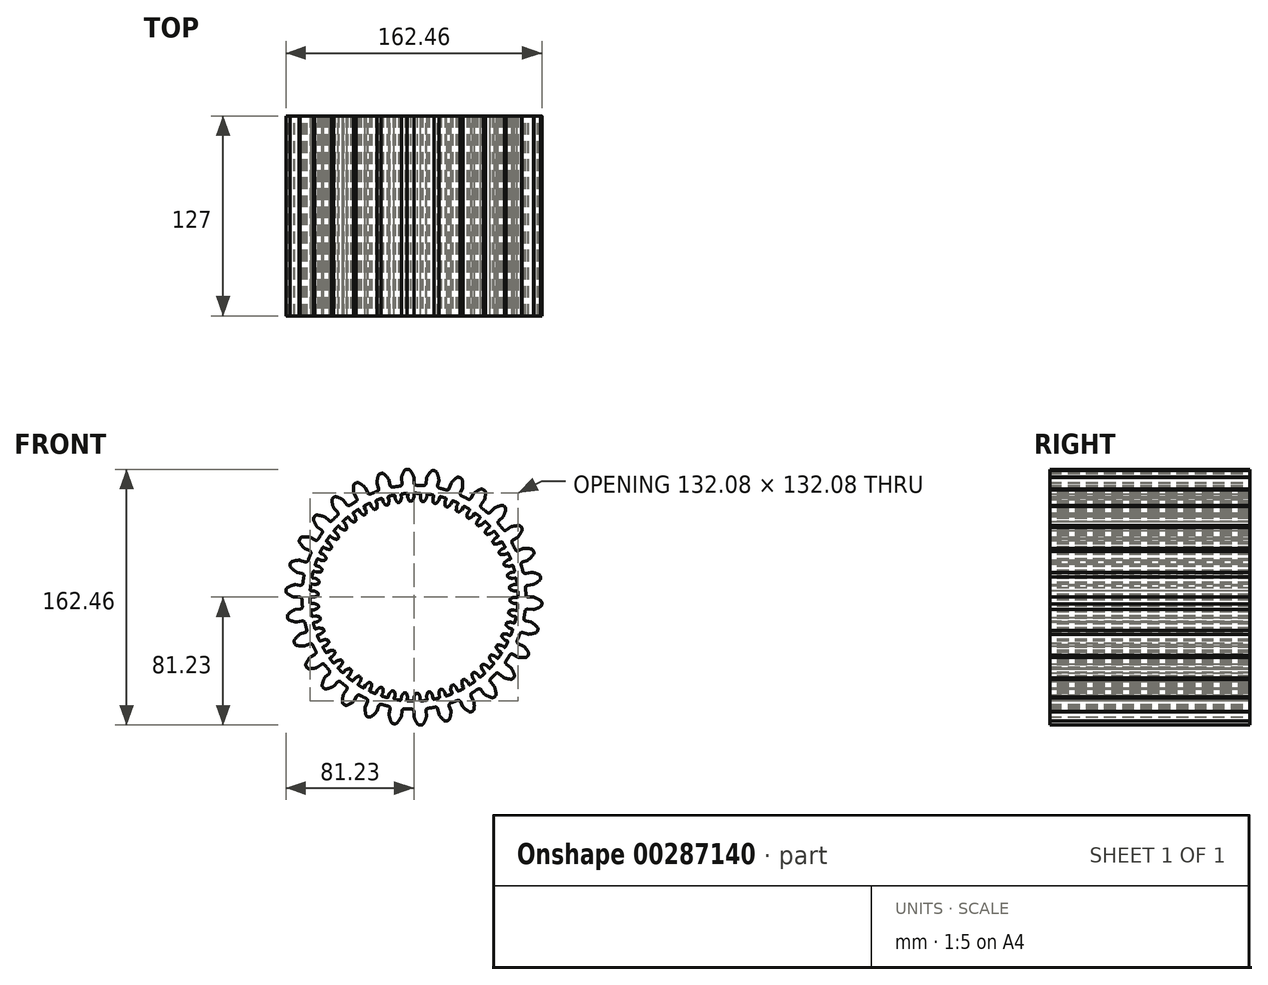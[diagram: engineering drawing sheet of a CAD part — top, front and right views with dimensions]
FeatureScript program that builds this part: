
annotation { "Feature Type Name" : "Feature", "Feature Type Description" : "" }
export const myFeature = defineFeature(function(context is Context, id is Id, definition is map)
    precondition{}
    {
        {
            var Q0;
            Q0=qCreatedBy(makeId("Front.planeOp"),FACE);
            var sketch = newSketch(context, id + "F0", { "sketchPlane" : qUnion([Q0])});
            skArc(sketch, "E0", {"start": v(-8.92, 70.56) * mm, "mid": v(-11.13, 70.24) * mm, "end": v(-13.32, 69.86) * mm});
            skPoint(sketch, "E1", {"position": v(0, 76.2) * mm});
            skArc(sketch, "E2.trimOffspring", {"start": v(-0.11, 76.48) * mm, "mid": v(-1.13, 78.61) * mm, "end": v(-2.4, 80.6) * mm});
            skLineSegment(sketch, "E3", {"start": v(-3.63, 81.23) * mm, "end": v(-4.26, 81.23) * mm});
            skLineSegment(sketch, "E4", {"start": v(0, 75.91) * mm, "end": v(0, 72.63) * mm});
            skLineSegment(sketch, "E5.MirrorCS", {"start": v(-4.88, 81.16) * mm, "end": v(-4.26, 81.23) * mm});
            skArc(sketch, "E6.MirrorCS", {"start": v(-7.88, 76.07) * mm, "mid": v(-7.1, 78.3) * mm, "end": v(-6.04, 80.41) * mm});
            skLineSegment(sketch, "E7.MirrorCS", {"start": v(-7.93, 75.5) * mm, "end": v(-7.6, 72.23) * mm});
            skPoint(sketch, "E8.orphan", {"position": v(0, 69.34) * mm});
            skPoint(sketch, "E9.visualSharp", {"position": v(-7.43, 70.73) * mm});
            skPoint(sketch, "E10.visualSharp", {"position": v(0, 71.12) * mm});
            skArc(sketch, "E10.filletArc", {"start": v(0, 72.63) * mm, "mid": v(0.44, 71.56) * mm, "end": v(1.5, 71.1) * mm});
            skArc(sketch, "E11.filletArc", {"start": v(-8.92, 70.56) * mm, "mid": v(-7.91, 71.12) * mm, "end": v(-7.6, 72.23) * mm});
            skPoint(sketch, "E12.visualSharp", {"position": v(-7.97, 75.78) * mm});
            skArc(sketch, "E12.filletArc", {"start": v(-7.88, 76.07) * mm, "mid": v(-7.94, 75.79) * mm, "end": v(-7.93, 75.5) * mm});
            skPoint(sketch, "E13.visualSharp", {"position": v(-5.63, 81.08) * mm});
            skArc(sketch, "E13.filletArc", {"start": v(-4.88, 81.16) * mm, "mid": v(-5.55, 80.93) * mm, "end": v(-6.04, 80.41) * mm});
            skPoint(sketch, "E14.visualSharp", {"position": v(-2.88, 81.23) * mm});
            skArc(sketch, "E14.filletArc", {"start": v(-2.4, 80.6) * mm, "mid": v(-2.94, 81.06) * mm, "end": v(-3.63, 81.23) * mm});
            skArc(sketch, "E15.filletArc", {"start": v(0, 75.91) * mm, "mid": v(-0.03, 76.2) * mm, "end": v(-0.11, 76.48) * mm});
            skArc(sketch, "E16.1.0", {"start": v(-23.4, 67.16) * mm, "mid": v(-22.53, 67.92) * mm, "end": v(-22.44, 69.07) * mm});
            skArc(sketch, "E16.1.1", {"start": v(-15.1, 71.04) * mm, "mid": v(-14.45, 70.09) * mm, "end": v(-13.32, 69.86) * mm});
            skLineSegment(sketch, "E16.1.2", {"start": v(-15.78, 74.25) * mm, "end": v(-15.1, 71.04) * mm});
            skLineSegment(sketch, "E16.1.3", {"start": v(-23.46, 72.2) * mm, "end": v(-22.44, 69.07) * mm});
            skLineSegment(sketch, "E16.1.4", {"start": v(-21.65, 78.38) * mm, "end": v(-21.05, 78.57) * mm});
            skPoint(sketch, "E16.1.5", {"position": v(-15.84, 74.53) * mm});
            skArc(sketch, "E16.1.6", {"start": v(-23.53, 72.77) * mm, "mid": v(-23.22, 75.11) * mm, "end": v(-22.62, 77.4) * mm});
            skArc(sketch, "E16.1.7", {"start": v(-16, 74.79) * mm, "mid": v(-17.45, 76.66) * mm, "end": v(-19.1, 78.34) * mm});
            skLineSegment(sketch, "E16.1.8", {"start": v(-20.44, 78.7) * mm, "end": v(-21.05, 78.57) * mm});
            skPoint(sketch, "E16.1.9", {"position": v(-19.7, 78.86) * mm});
            skArc(sketch, "E16.1.10", {"start": v(-19.1, 78.34) * mm, "mid": v(-19.73, 78.68) * mm, "end": v(-20.44, 78.7) * mm});
            skArc(sketch, "E16.1.11", {"start": v(-21.65, 78.38) * mm, "mid": v(-22.25, 78) * mm, "end": v(-22.62, 77.4) * mm});
            skPoint(sketch, "E16.1.12", {"position": v(-23.55, 72.47) * mm});
            skPoint(sketch, "E16.1.13", {"position": v(-22.36, 78.14) * mm});
            skArc(sketch, "E16.1.14", {"start": v(-23.53, 72.77) * mm, "mid": v(-23.52, 72.48) * mm, "end": v(-23.46, 72.2) * mm});
            skPoint(sketch, "E16.1.15", {"position": v(-15.84, 74.53) * mm});
            skArc(sketch, "E16.1.16", {"start": v(-15.78, 74.25) * mm, "mid": v(-15.87, 74.53) * mm, "end": v(-16, 74.79) * mm});
            skArc(sketch, "E16.2.0", {"start": v(-36.84, 60.83) * mm, "mid": v(-36.16, 61.76) * mm, "end": v(-36.31, 62.9) * mm});
            skArc(sketch, "E16.2.1", {"start": v(-29.54, 66.35) * mm, "mid": v(-28.7, 65.55) * mm, "end": v(-27.56, 65.56) * mm});
            skLineSegment(sketch, "E16.2.2", {"start": v(-30.88, 69.35) * mm, "end": v(-29.54, 66.35) * mm});
            skLineSegment(sketch, "E16.2.3", {"start": v(-37.96, 65.74) * mm, "end": v(-36.31, 62.9) * mm});
            skLineSegment(sketch, "E16.2.4", {"start": v(-37.47, 72.16) * mm, "end": v(-36.93, 72.47) * mm});
            skPoint(sketch, "E16.2.5", {"position": v(-31, 69.61) * mm});
            skArc(sketch, "E16.2.6", {"start": v(-38.14, 66.29) * mm, "mid": v(-38.33, 68.65) * mm, "end": v(-38.22, 71) * mm});
            skArc(sketch, "E16.2.7", {"start": v(-31.2, 69.82) * mm, "mid": v(-33, 71.36) * mm, "end": v(-34.98, 72.66) * mm});
            skLineSegment(sketch, "E16.2.8", {"start": v(-36.36, 72.73) * mm, "end": v(-36.93, 72.47) * mm});
            skPoint(sketch, "E16.2.9", {"position": v(-35.67, 73.04) * mm});
            skArc(sketch, "E16.2.10", {"start": v(-34.98, 72.66) * mm, "mid": v(-35.66, 72.86) * mm, "end": v(-36.36, 72.73) * mm});
            skArc(sketch, "E16.2.11", {"start": v(-37.47, 72.16) * mm, "mid": v(-37.98, 71.67) * mm, "end": v(-38.22, 71) * mm});
            skPoint(sketch, "E16.2.12", {"position": v(-38.1, 66) * mm});
            skPoint(sketch, "E16.2.13", {"position": v(-38.12, 71.79) * mm});
            skArc(sketch, "E16.2.14", {"start": v(-38.14, 66.29) * mm, "mid": v(-38.08, 66) * mm, "end": v(-37.96, 65.74) * mm});
            skPoint(sketch, "E16.2.15", {"position": v(-31, 69.61) * mm});
            skArc(sketch, "E16.2.16", {"start": v(-30.88, 69.35) * mm, "mid": v(-31.02, 69.6) * mm, "end": v(-31.2, 69.82) * mm});
            skArc(sketch, "E17.2.3.0", {"start": v(-48.69, 51.84) * mm, "mid": v(-48.2, 52.89) * mm, "end": v(-48.6, 53.97) * mm});
            skArc(sketch, "E17.4.3.0", {"start": v(-42.69, 58.76) * mm, "mid": v(-41.71, 58.15) * mm, "end": v(-40.59, 58.4) * mm});
            skLineSegment(sketch, "E17.8.3.0", {"start": v(-44.62, 61.41) * mm, "end": v(-42.69, 58.76) * mm});
            skLineSegment(sketch, "E17.11.3.0", {"start": v(-50.8, 56.41) * mm, "end": v(-48.6, 53.97) * mm});
            skLineSegment(sketch, "E17.14.3.0", {"start": v(-51.65, 62.8) * mm, "end": v(-51.19, 63.21) * mm});
            skPoint(sketch, "E17.17.3.0", {"position": v(-44.79, 61.65) * mm});
            skArc(sketch, "E17.18.3.0", {"start": v(-51.1, 56.9) * mm, "mid": v(-51.76, 59.18) * mm, "end": v(-52.15, 61.5) * mm});
            skArc(sketch, "E17.22.3.0", {"start": v(-45.04, 61.8) * mm, "mid": v(-47.12, 62.94) * mm, "end": v(-49.32, 63.8) * mm});
            skLineSegment(sketch, "E17.26.3.0", {"start": v(-50.68, 63.58) * mm, "end": v(-51.19, 63.21) * mm});
            skPoint(sketch, "E17.29.3.0", {"position": v(-50.07, 64.02) * mm});
            skArc(sketch, "E17.30.3.0", {"start": v(-49.32, 63.8) * mm, "mid": v(-50.03, 63.85) * mm, "end": v(-50.68, 63.58) * mm});
            skArc(sketch, "E17.34.3.0", {"start": v(-51.65, 62.8) * mm, "mid": v(-52.06, 62.21) * mm, "end": v(-52.15, 61.5) * mm});
            skPoint(sketch, "E17.38.3.0", {"position": v(-50.99, 56.63) * mm});
            skPoint(sketch, "E17.39.3.0", {"position": v(-52.21, 62.3) * mm});
            skArc(sketch, "E17.40.3.0", {"start": v(-51.1, 56.9) * mm, "mid": v(-50.97, 56.65) * mm, "end": v(-50.8, 56.41) * mm});
            skPoint(sketch, "E17.44.3.0", {"position": v(-44.79, 61.65) * mm});
            skArc(sketch, "E17.45.3.0", {"start": v(-44.62, 61.41) * mm, "mid": v(-44.81, 61.63) * mm, "end": v(-45.04, 61.8) * mm});
            skArc(sketch, "E17.2.4.0", {"start": v(-58.4, 40.59) * mm, "mid": v(-58.15, 41.71) * mm, "end": v(-58.76, 42.69) * mm});
            skArc(sketch, "E17.4.4.0", {"start": v(-53.97, 48.6) * mm, "mid": v(-52.89, 48.2) * mm, "end": v(-51.84, 48.69) * mm});
            skLineSegment(sketch, "E17.8.4.0", {"start": v(-56.41, 50.8) * mm, "end": v(-53.97, 48.6) * mm});
            skLineSegment(sketch, "E17.11.4.0", {"start": v(-61.41, 44.62) * mm, "end": v(-58.76, 42.69) * mm});
            skLineSegment(sketch, "E17.14.4.0", {"start": v(-63.58, 50.68) * mm, "end": v(-63.21, 51.19) * mm});
            skPoint(sketch, "E17.17.4.0", {"position": v(-56.63, 50.99) * mm});
            skArc(sketch, "E17.18.4.0", {"start": v(-61.8, 45.04) * mm, "mid": v(-62.94, 47.12) * mm, "end": v(-63.8, 49.32) * mm});
            skArc(sketch, "E17.22.4.0", {"start": v(-56.9, 51.1) * mm, "mid": v(-59.18, 51.76) * mm, "end": v(-61.5, 52.15) * mm});
            skLineSegment(sketch, "E17.26.4.0", {"start": v(-62.8, 51.65) * mm, "end": v(-63.21, 51.19) * mm});
            skPoint(sketch, "E17.29.4.0", {"position": v(-62.3, 52.21) * mm});
            skArc(sketch, "E17.30.4.0", {"start": v(-61.5, 52.15) * mm, "mid": v(-62.21, 52.06) * mm, "end": v(-62.8, 51.65) * mm});
            skArc(sketch, "E17.34.4.0", {"start": v(-63.58, 50.68) * mm, "mid": v(-63.85, 50.03) * mm, "end": v(-63.8, 49.32) * mm});
            skPoint(sketch, "E17.38.4.0", {"position": v(-61.65, 44.79) * mm});
            skPoint(sketch, "E17.39.4.0", {"position": v(-64.02, 50.07) * mm});
            skArc(sketch, "E17.40.4.0", {"start": v(-61.8, 45.04) * mm, "mid": v(-61.63, 44.81) * mm, "end": v(-61.41, 44.62) * mm});
            skPoint(sketch, "E17.44.4.0", {"position": v(-56.63, 50.99) * mm});
            skArc(sketch, "E17.45.4.0", {"start": v(-56.41, 50.8) * mm, "mid": v(-56.65, 50.97) * mm, "end": v(-56.9, 51.1) * mm});
            skArc(sketch, "E17.2.5.0", {"start": v(-65.56, 27.56) * mm, "mid": v(-65.55, 28.7) * mm, "end": v(-66.35, 29.54) * mm});
            skArc(sketch, "E17.4.5.0", {"start": v(-62.9, 36.31) * mm, "mid": v(-61.76, 36.16) * mm, "end": v(-60.83, 36.84) * mm});
            skLineSegment(sketch, "E17.8.5.0", {"start": v(-65.74, 37.96) * mm, "end": v(-62.9, 36.31) * mm});
            skLineSegment(sketch, "E17.11.5.0", {"start": v(-69.35, 30.88) * mm, "end": v(-66.35, 29.54) * mm});
            skLineSegment(sketch, "E17.14.5.0", {"start": v(-72.73, 36.36) * mm, "end": v(-72.47, 36.93) * mm});
            skPoint(sketch, "E17.17.5.0", {"position": v(-66, 38.1) * mm});
            skArc(sketch, "E17.18.5.0", {"start": v(-69.82, 31.2) * mm, "mid": v(-71.36, 33) * mm, "end": v(-72.66, 34.98) * mm});
            skArc(sketch, "E17.22.5.0", {"start": v(-66.29, 38.14) * mm, "mid": v(-68.65, 38.33) * mm, "end": v(-71, 38.22) * mm});
            skLineSegment(sketch, "E17.26.5.0", {"start": v(-72.16, 37.47) * mm, "end": v(-72.47, 36.93) * mm});
            skPoint(sketch, "E17.29.5.0", {"position": v(-71.79, 38.12) * mm});
            skArc(sketch, "E17.30.5.0", {"start": v(-71, 38.22) * mm, "mid": v(-71.67, 37.98) * mm, "end": v(-72.16, 37.47) * mm});
            skArc(sketch, "E17.34.5.0", {"start": v(-72.73, 36.36) * mm, "mid": v(-72.86, 35.66) * mm, "end": v(-72.66, 34.98) * mm});
            skPoint(sketch, "E17.38.5.0", {"position": v(-69.61, 31) * mm});
            skPoint(sketch, "E17.39.5.0", {"position": v(-73.04, 35.67) * mm});
            skArc(sketch, "E17.40.5.0", {"start": v(-69.82, 31.2) * mm, "mid": v(-69.6, 31.02) * mm, "end": v(-69.35, 30.88) * mm});
            skPoint(sketch, "E17.44.5.0", {"position": v(-66, 38.1) * mm});
            skArc(sketch, "E17.45.5.0", {"start": v(-65.74, 37.96) * mm, "mid": v(-66, 38.08) * mm, "end": v(-66.29, 38.14) * mm});
            skArc(sketch, "E17.2.6.0", {"start": v(-69.86, 13.32) * mm, "mid": v(-70.09, 14.45) * mm, "end": v(-71.04, 15.1) * mm});
            skArc(sketch, "E17.4.6.0", {"start": v(-69.07, 22.44) * mm, "mid": v(-67.92, 22.53) * mm, "end": v(-67.16, 23.4) * mm});
            skLineSegment(sketch, "E17.8.6.0", {"start": v(-72.2, 23.46) * mm, "end": v(-69.07, 22.44) * mm});
            skLineSegment(sketch, "E17.11.6.0", {"start": v(-74.25, 15.78) * mm, "end": v(-71.04, 15.1) * mm});
            skLineSegment(sketch, "E17.14.6.0", {"start": v(-78.7, 20.44) * mm, "end": v(-78.57, 21.05) * mm});
            skPoint(sketch, "E17.17.6.0", {"position": v(-72.47, 23.55) * mm});
            skArc(sketch, "E17.18.6.0", {"start": v(-74.79, 16) * mm, "mid": v(-76.66, 17.45) * mm, "end": v(-78.34, 19.1) * mm});
            skArc(sketch, "E17.22.6.0", {"start": v(-72.77, 23.53) * mm, "mid": v(-75.11, 23.22) * mm, "end": v(-77.4, 22.62) * mm});
            skLineSegment(sketch, "E17.26.6.0", {"start": v(-78.38, 21.65) * mm, "end": v(-78.57, 21.05) * mm});
            skPoint(sketch, "E17.29.6.0", {"position": v(-78.14, 22.36) * mm});
            skArc(sketch, "E17.30.6.0", {"start": v(-77.4, 22.62) * mm, "mid": v(-78, 22.25) * mm, "end": v(-78.38, 21.65) * mm});
            skArc(sketch, "E17.34.6.0", {"start": v(-78.7, 20.44) * mm, "mid": v(-78.68, 19.73) * mm, "end": v(-78.34, 19.1) * mm});
            skPoint(sketch, "E17.38.6.0", {"position": v(-74.53, 15.84) * mm});
            skPoint(sketch, "E17.39.6.0", {"position": v(-78.86, 19.7) * mm});
            skArc(sketch, "E17.40.6.0", {"start": v(-74.79, 16) * mm, "mid": v(-74.53, 15.87) * mm, "end": v(-74.25, 15.78) * mm});
            skPoint(sketch, "E17.44.6.0", {"position": v(-72.47, 23.55) * mm});
            skArc(sketch, "E17.45.6.0", {"start": v(-72.2, 23.46) * mm, "mid": v(-72.48, 23.52) * mm, "end": v(-72.77, 23.53) * mm});
            skArc(sketch, "E17.2.7.0", {"start": v(-71.1, -1.5) * mm, "mid": v(-71.56, -0.44) * mm, "end": v(-72.63, 0) * mm});
            skArc(sketch, "E17.4.7.0", {"start": v(-72.23, 7.6) * mm, "mid": v(-71.12, 7.91) * mm, "end": v(-70.56, 8.92) * mm});
            skLineSegment(sketch, "E17.8.7.0", {"start": v(-75.5, 7.93) * mm, "end": v(-72.23, 7.6) * mm});
            skLineSegment(sketch, "E17.11.7.0", {"start": v(-75.91, 0) * mm, "end": v(-72.63, 0) * mm});
            skLineSegment(sketch, "E17.14.7.0", {"start": v(-81.23, 3.63) * mm, "end": v(-81.23, 4.26) * mm});
            skPoint(sketch, "E17.17.7.0", {"position": v(-75.78, 7.97) * mm});
            skArc(sketch, "E17.18.7.0", {"start": v(-76.48, 0.11) * mm, "mid": v(-78.61, 1.13) * mm, "end": v(-80.6, 2.4) * mm});
            skArc(sketch, "E17.22.7.0", {"start": v(-76.07, 7.88) * mm, "mid": v(-78.3, 7.1) * mm, "end": v(-80.41, 6.04) * mm});
            skLineSegment(sketch, "E17.26.7.0", {"start": v(-81.16, 4.88) * mm, "end": v(-81.23, 4.26) * mm});
            skPoint(sketch, "E17.29.7.0", {"position": v(-81.08, 5.63) * mm});
            skArc(sketch, "E17.30.7.0", {"start": v(-80.41, 6.04) * mm, "mid": v(-80.93, 5.55) * mm, "end": v(-81.16, 4.88) * mm});
            skArc(sketch, "E17.34.7.0", {"start": v(-81.23, 3.63) * mm, "mid": v(-81.06, 2.94) * mm, "end": v(-80.6, 2.4) * mm});
            skPoint(sketch, "E17.38.7.0", {"position": v(-76.2, 0) * mm});
            skPoint(sketch, "E17.39.7.0", {"position": v(-81.23, 2.88) * mm});
            skArc(sketch, "E17.40.7.0", {"start": v(-76.48, 0.11) * mm, "mid": v(-76.2, 0.03) * mm, "end": v(-75.91, 0) * mm});
            skPoint(sketch, "E17.44.7.0", {"position": v(-75.78, 7.97) * mm});
            skArc(sketch, "E17.45.7.0", {"start": v(-75.5, 7.93) * mm, "mid": v(-75.79, 7.94) * mm, "end": v(-76.07, 7.88) * mm});
            skArc(sketch, "E17.2.8.0", {"start": v(-69.24, -16.24) * mm, "mid": v(-69.9, -15.3) * mm, "end": v(-71.04, -15.1) * mm});
            skArc(sketch, "E17.4.8.0", {"start": v(-72.23, -7.6) * mm, "mid": v(-71.22, -7.05) * mm, "end": v(-70.87, -5.95) * mm});
            skLineSegment(sketch, "E17.8.8.0", {"start": v(-75.5, -7.93) * mm, "end": v(-72.23, -7.6) * mm});
            skLineSegment(sketch, "E17.11.8.0", {"start": v(-74.25, -15.78) * mm, "end": v(-71.04, -15.1) * mm});
            skLineSegment(sketch, "E17.14.8.0", {"start": v(-80.2, -13.34) * mm, "end": v(-80.34, -12.72) * mm});
            skPoint(sketch, "E17.17.8.0", {"position": v(-75.78, -7.97) * mm});
            skArc(sketch, "E17.18.8.0", {"start": v(-74.83, -15.8) * mm, "mid": v(-77.13, -15.24) * mm, "end": v(-79.34, -14.4) * mm});
            skArc(sketch, "E17.22.8.0", {"start": v(-76.05, -8.1) * mm, "mid": v(-78.07, -9.34) * mm, "end": v(-79.91, -10.81) * mm});
            skLineSegment(sketch, "E17.26.8.0", {"start": v(-80.4, -12.1) * mm, "end": v(-80.34, -12.72) * mm});
            skPoint(sketch, "E17.29.8.0", {"position": v(-80.48, -11.35) * mm});
            skArc(sketch, "E17.30.8.0", {"start": v(-79.91, -10.81) * mm, "mid": v(-80.31, -11.4) * mm, "end": v(-80.4, -12.1) * mm});
            skArc(sketch, "E17.34.8.0", {"start": v(-80.2, -13.34) * mm, "mid": v(-79.9, -13.98) * mm, "end": v(-79.34, -14.4) * mm});
            skPoint(sketch, "E17.38.8.0", {"position": v(-74.53, -15.84) * mm});
            skPoint(sketch, "E17.39.8.0", {"position": v(-80.05, -14.07) * mm});
            skArc(sketch, "E17.40.8.0", {"start": v(-74.83, -15.8) * mm, "mid": v(-74.54, -15.82) * mm, "end": v(-74.25, -15.78) * mm});
            skPoint(sketch, "E17.44.8.0", {"position": v(-75.78, -7.97) * mm});
            skArc(sketch, "E17.45.8.0", {"start": v(-75.5, -7.93) * mm, "mid": v(-75.78, -8) * mm, "end": v(-76.05, -8.1) * mm});
            skArc(sketch, "E17.2.9.0", {"start": v(-64.35, -30.28) * mm, "mid": v(-65.2, -29.5) * mm, "end": v(-66.35, -29.54) * mm});
            skArc(sketch, "E17.4.9.0", {"start": v(-69.07, -22.44) * mm, "mid": v(-68.2, -21.7) * mm, "end": v(-68.09, -20.55) * mm});
            skLineSegment(sketch, "E17.8.9.0", {"start": v(-72.2, -23.46) * mm, "end": v(-69.07, -22.44) * mm});
            skLineSegment(sketch, "E17.11.9.0", {"start": v(-69.35, -30.88) * mm, "end": v(-66.35, -29.54) * mm});
            skLineSegment(sketch, "E17.14.9.0", {"start": v(-75.68, -29.72) * mm, "end": v(-75.94, -29.15) * mm});
            skPoint(sketch, "E17.17.9.0", {"position": v(-72.47, -23.55) * mm});
            skArc(sketch, "E17.18.9.0", {"start": v(-69.91, -31) * mm, "mid": v(-72.28, -30.94) * mm, "end": v(-74.61, -30.6) * mm});
            skArc(sketch, "E17.22.9.0", {"start": v(-72.7, -23.74) * mm, "mid": v(-74.42, -25.37) * mm, "end": v(-75.92, -27.2) * mm});
            skLineSegment(sketch, "E17.26.9.0", {"start": v(-76.13, -28.56) * mm, "end": v(-75.94, -29.15) * mm});
            skPoint(sketch, "E17.29.9.0", {"position": v(-76.36, -27.84) * mm});
            skArc(sketch, "E17.30.9.0", {"start": v(-75.92, -27.2) * mm, "mid": v(-76.19, -27.85) * mm, "end": v(-76.13, -28.56) * mm});
            skArc(sketch, "E17.34.9.0", {"start": v(-75.68, -29.72) * mm, "mid": v(-75.25, -30.28) * mm, "end": v(-74.61, -30.6) * mm});
            skPoint(sketch, "E17.38.9.0", {"position": v(-69.61, -31) * mm});
            skPoint(sketch, "E17.39.9.0", {"position": v(-75.38, -30.4) * mm});
            skArc(sketch, "E17.40.9.0", {"start": v(-69.91, -31) * mm, "mid": v(-69.62, -30.97) * mm, "end": v(-69.35, -30.88) * mm});
            skPoint(sketch, "E17.44.9.0", {"position": v(-72.47, -23.55) * mm});
            skArc(sketch, "E17.45.9.0", {"start": v(-72.2, -23.46) * mm, "mid": v(-72.46, -23.57) * mm, "end": v(-72.7, -23.74) * mm});
            skArc(sketch, "E17.2.10.0", {"start": v(-56.65, -43) * mm, "mid": v(-57.64, -42.41) * mm, "end": v(-58.76, -42.69) * mm});
            skArc(sketch, "E17.4.10.0", {"start": v(-62.9, -36.31) * mm, "mid": v(-62.2, -35.4) * mm, "end": v(-62.32, -34.26) * mm});
            skLineSegment(sketch, "E17.8.10.0", {"start": v(-65.74, -37.96) * mm, "end": v(-62.9, -36.31) * mm});
            skLineSegment(sketch, "E17.11.10.0", {"start": v(-61.41, -44.62) * mm, "end": v(-58.76, -42.69) * mm});
            skLineSegment(sketch, "E17.14.10.0", {"start": v(-67.85, -44.8) * mm, "end": v(-68.22, -44.3) * mm});
            skPoint(sketch, "E17.17.10.0", {"position": v(-66, -38.1) * mm});
            skArc(sketch, "E17.18.10.0", {"start": v(-61.94, -44.86) * mm, "mid": v(-64.26, -45.3) * mm, "end": v(-66.62, -45.44) * mm});
            skArc(sketch, "E17.22.10.0", {"start": v(-66.18, -38.34) * mm, "mid": v(-67.52, -40.28) * mm, "end": v(-68.6, -42.38) * mm});
            skLineSegment(sketch, "E17.26.10.0", {"start": v(-68.53, -43.76) * mm, "end": v(-68.22, -44.3) * mm});
            skPoint(sketch, "E17.29.10.0", {"position": v(-68.9, -43.1) * mm});
            skArc(sketch, "E17.30.10.0", {"start": v(-68.6, -42.38) * mm, "mid": v(-68.73, -43.08) * mm, "end": v(-68.53, -43.76) * mm});
            skArc(sketch, "E17.34.10.0", {"start": v(-67.85, -44.8) * mm, "mid": v(-67.31, -45.27) * mm, "end": v(-66.62, -45.44) * mm});
            skPoint(sketch, "E17.38.10.0", {"position": v(-61.65, -44.79) * mm});
            skPoint(sketch, "E17.39.10.0", {"position": v(-67.4, -45.42) * mm});
            skArc(sketch, "E17.40.10.0", {"start": v(-61.94, -44.86) * mm, "mid": v(-61.66, -44.77) * mm, "end": v(-61.41, -44.62) * mm});
            skPoint(sketch, "E17.44.10.0", {"position": v(-66, -38.1) * mm});
            skArc(sketch, "E17.45.10.0", {"start": v(-65.74, -37.96) * mm, "mid": v(-65.98, -38.12) * mm, "end": v(-66.18, -38.34) * mm});
            skArc(sketch, "E17.2.11.0", {"start": v(-46.47, -53.84) * mm, "mid": v(-47.56, -53.47) * mm, "end": v(-48.6, -53.97) * mm});
            skArc(sketch, "E17.4.11.0", {"start": v(-53.97, -48.6) * mm, "mid": v(-53.47, -47.56) * mm, "end": v(-53.84, -46.47) * mm});
            skLineSegment(sketch, "E17.8.11.0", {"start": v(-56.41, -50.8) * mm, "end": v(-53.97, -48.6) * mm});
            skLineSegment(sketch, "E17.11.11.0", {"start": v(-50.8, -56.41) * mm, "end": v(-48.6, -53.97) * mm});
            skLineSegment(sketch, "E17.14.11.0", {"start": v(-57.05, -57.93) * mm, "end": v(-57.52, -57.52) * mm});
            skPoint(sketch, "E17.17.11.0", {"position": v(-56.63, -50.99) * mm});
            skArc(sketch, "E17.18.11.0", {"start": v(-51.26, -56.76) * mm, "mid": v(-53.44, -57.67) * mm, "end": v(-55.72, -58.3) * mm});
            skArc(sketch, "E17.22.11.0", {"start": v(-56.76, -51.26) * mm, "mid": v(-57.67, -53.44) * mm, "end": v(-58.3, -55.72) * mm});
            skLineSegment(sketch, "E17.26.11.0", {"start": v(-57.93, -57.05) * mm, "end": v(-57.52, -57.52) * mm});
            skPoint(sketch, "E17.29.11.0", {"position": v(-58.44, -56.5) * mm});
            skArc(sketch, "E17.30.11.0", {"start": v(-58.3, -55.72) * mm, "mid": v(-58.27, -56.43) * mm, "end": v(-57.93, -57.05) * mm});
            skArc(sketch, "E17.34.11.0", {"start": v(-57.05, -57.93) * mm, "mid": v(-56.43, -58.27) * mm, "end": v(-55.72, -58.3) * mm});
            skPoint(sketch, "E17.38.11.0", {"position": v(-50.99, -56.63) * mm});
            skPoint(sketch, "E17.39.11.0", {"position": v(-56.5, -58.44) * mm});
            skArc(sketch, "E17.40.11.0", {"start": v(-51.26, -56.76) * mm, "mid": v(-51, -56.6) * mm, "end": v(-50.8, -56.41) * mm});
            skPoint(sketch, "E17.44.11.0", {"position": v(-56.63, -50.99) * mm});
            skArc(sketch, "E17.45.11.0", {"start": v(-56.41, -50.8) * mm, "mid": v(-56.6, -51) * mm, "end": v(-56.76, -51.26) * mm});
            skArc(sketch, "E17.2.12.0", {"start": v(-34.26, -62.32) * mm, "mid": v(-35.4, -62.2) * mm, "end": v(-36.31, -62.9) * mm});
            skArc(sketch, "E17.4.12.0", {"start": v(-42.69, -58.76) * mm, "mid": v(-42.41, -57.64) * mm, "end": v(-43, -56.65) * mm});
            skLineSegment(sketch, "E17.8.12.0", {"start": v(-44.62, -61.41) * mm, "end": v(-42.69, -58.76) * mm});
            skLineSegment(sketch, "E17.11.12.0", {"start": v(-37.96, -65.74) * mm, "end": v(-36.31, -62.9) * mm});
            skLineSegment(sketch, "E17.14.12.0", {"start": v(-43.76, -68.53) * mm, "end": v(-44.3, -68.22) * mm});
            skPoint(sketch, "E17.17.12.0", {"position": v(-44.79, -61.65) * mm});
            skArc(sketch, "E17.18.12.0", {"start": v(-38.34, -66.18) * mm, "mid": v(-40.28, -67.52) * mm, "end": v(-42.38, -68.6) * mm});
            skArc(sketch, "E17.22.12.0", {"start": v(-44.86, -61.94) * mm, "mid": v(-45.3, -64.26) * mm, "end": v(-45.44, -66.62) * mm});
            skLineSegment(sketch, "E17.26.12.0", {"start": v(-44.8, -67.85) * mm, "end": v(-44.3, -68.22) * mm});
            skPoint(sketch, "E17.29.12.0", {"position": v(-45.42, -67.4) * mm});
            skArc(sketch, "E17.30.12.0", {"start": v(-45.44, -66.62) * mm, "mid": v(-45.27, -67.31) * mm, "end": v(-44.8, -67.85) * mm});
            skArc(sketch, "E17.34.12.0", {"start": v(-43.76, -68.53) * mm, "mid": v(-43.08, -68.73) * mm, "end": v(-42.38, -68.6) * mm});
            skPoint(sketch, "E17.38.12.0", {"position": v(-38.1, -66) * mm});
            skPoint(sketch, "E17.39.12.0", {"position": v(-43.1, -68.9) * mm});
            skArc(sketch, "E17.40.12.0", {"start": v(-38.34, -66.18) * mm, "mid": v(-38.12, -65.98) * mm, "end": v(-37.96, -65.74) * mm});
            skPoint(sketch, "E17.44.12.0", {"position": v(-44.79, -61.65) * mm});
            skArc(sketch, "E17.45.12.0", {"start": v(-44.62, -61.41) * mm, "mid": v(-44.77, -61.66) * mm, "end": v(-44.86, -61.94) * mm});
            skArc(sketch, "E17.2.13.0", {"start": v(-20.55, -68.09) * mm, "mid": v(-21.7, -68.2) * mm, "end": v(-22.44, -69.07) * mm});
            skArc(sketch, "E17.4.13.0", {"start": v(-29.54, -66.35) * mm, "mid": v(-29.5, -65.2) * mm, "end": v(-30.28, -64.35) * mm});
            skLineSegment(sketch, "E17.8.13.0", {"start": v(-30.88, -69.35) * mm, "end": v(-29.54, -66.35) * mm});
            skLineSegment(sketch, "E17.11.13.0", {"start": v(-23.46, -72.2) * mm, "end": v(-22.44, -69.07) * mm});
            skLineSegment(sketch, "E17.14.13.0", {"start": v(-28.56, -76.13) * mm, "end": v(-29.15, -75.94) * mm});
            skPoint(sketch, "E17.17.13.0", {"position": v(-31, -69.61) * mm});
            skArc(sketch, "E17.18.13.0", {"start": v(-23.74, -72.7) * mm, "mid": v(-25.37, -74.42) * mm, "end": v(-27.2, -75.92) * mm});
            skArc(sketch, "E17.22.13.0", {"start": v(-31, -69.91) * mm, "mid": v(-30.94, -72.28) * mm, "end": v(-30.6, -74.61) * mm});
            skLineSegment(sketch, "E17.26.13.0", {"start": v(-29.72, -75.68) * mm, "end": v(-29.15, -75.94) * mm});
            skPoint(sketch, "E17.29.13.0", {"position": v(-30.4, -75.38) * mm});
            skArc(sketch, "E17.30.13.0", {"start": v(-30.6, -74.61) * mm, "mid": v(-30.28, -75.25) * mm, "end": v(-29.72, -75.68) * mm});
            skArc(sketch, "E17.34.13.0", {"start": v(-28.56, -76.13) * mm, "mid": v(-27.85, -76.19) * mm, "end": v(-27.2, -75.92) * mm});
            skPoint(sketch, "E17.38.13.0", {"position": v(-23.55, -72.47) * mm});
            skPoint(sketch, "E17.39.13.0", {"position": v(-27.84, -76.36) * mm});
            skArc(sketch, "E17.40.13.0", {"start": v(-23.74, -72.7) * mm, "mid": v(-23.57, -72.46) * mm, "end": v(-23.46, -72.2) * mm});
            skPoint(sketch, "E17.44.13.0", {"position": v(-31, -69.61) * mm});
            skArc(sketch, "E17.45.13.0", {"start": v(-30.88, -69.35) * mm, "mid": v(-30.97, -69.62) * mm, "end": v(-31, -69.91) * mm});
            skArc(sketch, "E17.2.14.0", {"start": v(-5.95, -70.87) * mm, "mid": v(-7.05, -71.22) * mm, "end": v(-7.6, -72.23) * mm});
            skArc(sketch, "E17.4.14.0", {"start": v(-15.1, -71.04) * mm, "mid": v(-15.3, -69.9) * mm, "end": v(-16.24, -69.24) * mm});
            skLineSegment(sketch, "E17.8.14.0", {"start": v(-15.78, -74.25) * mm, "end": v(-15.1, -71.04) * mm});
            skLineSegment(sketch, "E17.11.14.0", {"start": v(-7.93, -75.5) * mm, "end": v(-7.6, -72.23) * mm});
            skLineSegment(sketch, "E17.14.14.0", {"start": v(-12.1, -80.4) * mm, "end": v(-12.72, -80.34) * mm});
            skPoint(sketch, "E17.17.14.0", {"position": v(-15.84, -74.53) * mm});
            skArc(sketch, "E17.18.14.0", {"start": v(-8.1, -76.05) * mm, "mid": v(-9.34, -78.07) * mm, "end": v(-10.81, -79.91) * mm});
            skArc(sketch, "E17.22.14.0", {"start": v(-15.8, -74.83) * mm, "mid": v(-15.24, -77.13) * mm, "end": v(-14.4, -79.34) * mm});
            skLineSegment(sketch, "E17.26.14.0", {"start": v(-13.34, -80.2) * mm, "end": v(-12.72, -80.34) * mm});
            skPoint(sketch, "E17.29.14.0", {"position": v(-14.07, -80.05) * mm});
            skArc(sketch, "E17.30.14.0", {"start": v(-14.4, -79.34) * mm, "mid": v(-13.98, -79.9) * mm, "end": v(-13.34, -80.2) * mm});
            skArc(sketch, "E17.34.14.0", {"start": v(-12.1, -80.4) * mm, "mid": v(-11.4, -80.31) * mm, "end": v(-10.81, -79.91) * mm});
            skPoint(sketch, "E17.38.14.0", {"position": v(-7.97, -75.78) * mm});
            skPoint(sketch, "E17.39.14.0", {"position": v(-11.35, -80.48) * mm});
            skArc(sketch, "E17.40.14.0", {"start": v(-8.1, -76.05) * mm, "mid": v(-8, -75.78) * mm, "end": v(-7.93, -75.5) * mm});
            skPoint(sketch, "E17.44.14.0", {"position": v(-15.84, -74.53) * mm});
            skArc(sketch, "E17.45.14.0", {"start": v(-15.78, -74.25) * mm, "mid": v(-15.82, -74.54) * mm, "end": v(-15.8, -74.83) * mm});
            skArc(sketch, "E17.2.15.0", {"start": v(8.92, -70.56) * mm, "mid": v(7.91, -71.12) * mm, "end": v(7.6, -72.23) * mm});
            skArc(sketch, "E17.4.15.0", {"start": v(0, -72.63) * mm, "mid": v(-0.44, -71.56) * mm, "end": v(-1.5, -71.1) * mm});
            skLineSegment(sketch, "E17.8.15.0", {"start": v(0, -75.91) * mm, "end": v(0, -72.63) * mm});
            skLineSegment(sketch, "E17.11.15.0", {"start": v(7.93, -75.5) * mm, "end": v(7.6, -72.23) * mm});
            skLineSegment(sketch, "E17.14.15.0", {"start": v(4.88, -81.16) * mm, "end": v(4.26, -81.23) * mm});
            skPoint(sketch, "E17.17.15.0", {"position": v(0, -76.2) * mm});
            skArc(sketch, "E17.18.15.0", {"start": v(7.88, -76.07) * mm, "mid": v(7.1, -78.3) * mm, "end": v(6.04, -80.41) * mm});
            skArc(sketch, "E17.22.15.0", {"start": v(0.11, -76.48) * mm, "mid": v(1.13, -78.61) * mm, "end": v(2.4, -80.6) * mm});
            skLineSegment(sketch, "E17.26.15.0", {"start": v(3.63, -81.23) * mm, "end": v(4.26, -81.23) * mm});
            skPoint(sketch, "E17.29.15.0", {"position": v(2.88, -81.23) * mm});
            skArc(sketch, "E17.30.15.0", {"start": v(2.4, -80.6) * mm, "mid": v(2.94, -81.06) * mm, "end": v(3.63, -81.23) * mm});
            skArc(sketch, "E17.34.15.0", {"start": v(4.88, -81.16) * mm, "mid": v(5.55, -80.93) * mm, "end": v(6.04, -80.41) * mm});
            skPoint(sketch, "E17.38.15.0", {"position": v(7.97, -75.78) * mm});
            skPoint(sketch, "E17.39.15.0", {"position": v(5.63, -81.08) * mm});
            skArc(sketch, "E17.40.15.0", {"start": v(7.88, -76.07) * mm, "mid": v(7.94, -75.79) * mm, "end": v(7.93, -75.5) * mm});
            skPoint(sketch, "E17.44.15.0", {"position": v(0, -76.2) * mm});
            skArc(sketch, "E17.45.15.0", {"start": v(0, -75.91) * mm, "mid": v(0.03, -76.2) * mm, "end": v(0.11, -76.48) * mm});
            skArc(sketch, "E17.2.16.0", {"start": v(23.4, -67.16) * mm, "mid": v(22.53, -67.92) * mm, "end": v(22.44, -69.07) * mm});
            skArc(sketch, "E17.4.16.0", {"start": v(15.1, -71.04) * mm, "mid": v(14.45, -70.09) * mm, "end": v(13.32, -69.86) * mm});
            skLineSegment(sketch, "E17.8.16.0", {"start": v(15.78, -74.25) * mm, "end": v(15.1, -71.04) * mm});
            skLineSegment(sketch, "E17.11.16.0", {"start": v(23.46, -72.2) * mm, "end": v(22.44, -69.07) * mm});
            skLineSegment(sketch, "E17.14.16.0", {"start": v(21.65, -78.38) * mm, "end": v(21.05, -78.57) * mm});
            skPoint(sketch, "E17.17.16.0", {"position": v(15.84, -74.53) * mm});
            skArc(sketch, "E17.18.16.0", {"start": v(23.53, -72.77) * mm, "mid": v(23.22, -75.11) * mm, "end": v(22.62, -77.4) * mm});
            skArc(sketch, "E17.22.16.0", {"start": v(16, -74.79) * mm, "mid": v(17.45, -76.66) * mm, "end": v(19.1, -78.34) * mm});
            skLineSegment(sketch, "E17.26.16.0", {"start": v(20.44, -78.7) * mm, "end": v(21.05, -78.57) * mm});
            skPoint(sketch, "E17.29.16.0", {"position": v(19.7, -78.86) * mm});
            skArc(sketch, "E17.30.16.0", {"start": v(19.1, -78.34) * mm, "mid": v(19.73, -78.68) * mm, "end": v(20.44, -78.7) * mm});
            skArc(sketch, "E17.34.16.0", {"start": v(21.65, -78.38) * mm, "mid": v(22.25, -78) * mm, "end": v(22.62, -77.4) * mm});
            skPoint(sketch, "E17.38.16.0", {"position": v(23.55, -72.47) * mm});
            skPoint(sketch, "E17.39.16.0", {"position": v(22.36, -78.14) * mm});
            skArc(sketch, "E17.40.16.0", {"start": v(23.53, -72.77) * mm, "mid": v(23.52, -72.48) * mm, "end": v(23.46, -72.2) * mm});
            skPoint(sketch, "E17.44.16.0", {"position": v(15.84, -74.53) * mm});
            skArc(sketch, "E17.45.16.0", {"start": v(15.78, -74.25) * mm, "mid": v(15.87, -74.53) * mm, "end": v(16, -74.79) * mm});
            skArc(sketch, "E17.2.17.0", {"start": v(36.84, -60.83) * mm, "mid": v(36.16, -61.76) * mm, "end": v(36.31, -62.9) * mm});
            skArc(sketch, "E17.4.17.0", {"start": v(29.54, -66.35) * mm, "mid": v(28.7, -65.55) * mm, "end": v(27.56, -65.56) * mm});
            skLineSegment(sketch, "E17.8.17.0", {"start": v(30.88, -69.35) * mm, "end": v(29.54, -66.35) * mm});
            skLineSegment(sketch, "E17.11.17.0", {"start": v(37.96, -65.74) * mm, "end": v(36.31, -62.9) * mm});
            skLineSegment(sketch, "E17.14.17.0", {"start": v(37.47, -72.16) * mm, "end": v(36.93, -72.47) * mm});
            skPoint(sketch, "E17.17.17.0", {"position": v(31, -69.61) * mm});
            skArc(sketch, "E17.18.17.0", {"start": v(38.14, -66.29) * mm, "mid": v(38.33, -68.65) * mm, "end": v(38.22, -71) * mm});
            skArc(sketch, "E17.22.17.0", {"start": v(31.2, -69.82) * mm, "mid": v(33, -71.36) * mm, "end": v(34.98, -72.66) * mm});
            skLineSegment(sketch, "E17.26.17.0", {"start": v(36.36, -72.73) * mm, "end": v(36.93, -72.47) * mm});
            skPoint(sketch, "E17.29.17.0", {"position": v(35.67, -73.04) * mm});
            skArc(sketch, "E17.30.17.0", {"start": v(34.98, -72.66) * mm, "mid": v(35.66, -72.86) * mm, "end": v(36.36, -72.73) * mm});
            skArc(sketch, "E17.34.17.0", {"start": v(37.47, -72.16) * mm, "mid": v(37.98, -71.67) * mm, "end": v(38.22, -71) * mm});
            skPoint(sketch, "E17.38.17.0", {"position": v(38.1, -66) * mm});
            skPoint(sketch, "E17.39.17.0", {"position": v(38.12, -71.79) * mm});
            skArc(sketch, "E17.40.17.0", {"start": v(38.14, -66.29) * mm, "mid": v(38.08, -66) * mm, "end": v(37.96, -65.74) * mm});
            skPoint(sketch, "E17.44.17.0", {"position": v(31, -69.61) * mm});
            skArc(sketch, "E17.45.17.0", {"start": v(30.88, -69.35) * mm, "mid": v(31.02, -69.6) * mm, "end": v(31.2, -69.82) * mm});
            skArc(sketch, "E17.2.18.0", {"start": v(48.69, -51.84) * mm, "mid": v(48.2, -52.89) * mm, "end": v(48.6, -53.97) * mm});
            skArc(sketch, "E17.4.18.0", {"start": v(42.69, -58.76) * mm, "mid": v(41.71, -58.15) * mm, "end": v(40.59, -58.4) * mm});
            skLineSegment(sketch, "E17.8.18.0", {"start": v(44.62, -61.41) * mm, "end": v(42.69, -58.76) * mm});
            skLineSegment(sketch, "E17.11.18.0", {"start": v(50.8, -56.41) * mm, "end": v(48.6, -53.97) * mm});
            skLineSegment(sketch, "E17.14.18.0", {"start": v(51.65, -62.8) * mm, "end": v(51.19, -63.21) * mm});
            skPoint(sketch, "E17.17.18.0", {"position": v(44.79, -61.65) * mm});
            skArc(sketch, "E17.18.18.0", {"start": v(51.1, -56.9) * mm, "mid": v(51.76, -59.18) * mm, "end": v(52.15, -61.5) * mm});
            skArc(sketch, "E17.22.18.0", {"start": v(45.04, -61.8) * mm, "mid": v(47.12, -62.94) * mm, "end": v(49.32, -63.8) * mm});
            skLineSegment(sketch, "E17.26.18.0", {"start": v(50.68, -63.58) * mm, "end": v(51.19, -63.21) * mm});
            skPoint(sketch, "E17.29.18.0", {"position": v(50.07, -64.02) * mm});
            skArc(sketch, "E17.30.18.0", {"start": v(49.32, -63.8) * mm, "mid": v(50.03, -63.85) * mm, "end": v(50.68, -63.58) * mm});
            skArc(sketch, "E17.34.18.0", {"start": v(51.65, -62.8) * mm, "mid": v(52.06, -62.21) * mm, "end": v(52.15, -61.5) * mm});
            skPoint(sketch, "E17.38.18.0", {"position": v(50.99, -56.63) * mm});
            skPoint(sketch, "E17.39.18.0", {"position": v(52.21, -62.3) * mm});
            skArc(sketch, "E17.40.18.0", {"start": v(51.1, -56.9) * mm, "mid": v(50.97, -56.65) * mm, "end": v(50.8, -56.41) * mm});
            skPoint(sketch, "E17.44.18.0", {"position": v(44.79, -61.65) * mm});
            skArc(sketch, "E17.45.18.0", {"start": v(44.62, -61.41) * mm, "mid": v(44.81, -61.63) * mm, "end": v(45.04, -61.8) * mm});
            skArc(sketch, "E17.2.19.0", {"start": v(58.4, -40.59) * mm, "mid": v(58.15, -41.71) * mm, "end": v(58.76, -42.69) * mm});
            skArc(sketch, "E17.4.19.0", {"start": v(53.97, -48.6) * mm, "mid": v(52.89, -48.2) * mm, "end": v(51.84, -48.69) * mm});
            skLineSegment(sketch, "E17.8.19.0", {"start": v(56.41, -50.8) * mm, "end": v(53.97, -48.6) * mm});
            skLineSegment(sketch, "E17.11.19.0", {"start": v(61.41, -44.62) * mm, "end": v(58.76, -42.69) * mm});
            skLineSegment(sketch, "E17.14.19.0", {"start": v(63.58, -50.68) * mm, "end": v(63.21, -51.19) * mm});
            skPoint(sketch, "E17.17.19.0", {"position": v(56.63, -50.99) * mm});
            skArc(sketch, "E17.18.19.0", {"start": v(61.8, -45.04) * mm, "mid": v(62.94, -47.12) * mm, "end": v(63.8, -49.32) * mm});
            skArc(sketch, "E17.22.19.0", {"start": v(56.9, -51.1) * mm, "mid": v(59.18, -51.76) * mm, "end": v(61.5, -52.15) * mm});
            skLineSegment(sketch, "E17.26.19.0", {"start": v(62.8, -51.65) * mm, "end": v(63.21, -51.19) * mm});
            skPoint(sketch, "E17.29.19.0", {"position": v(62.3, -52.21) * mm});
            skArc(sketch, "E17.30.19.0", {"start": v(61.5, -52.15) * mm, "mid": v(62.21, -52.06) * mm, "end": v(62.8, -51.65) * mm});
            skArc(sketch, "E17.34.19.0", {"start": v(63.58, -50.68) * mm, "mid": v(63.85, -50.03) * mm, "end": v(63.8, -49.32) * mm});
            skPoint(sketch, "E17.38.19.0", {"position": v(61.65, -44.79) * mm});
            skPoint(sketch, "E17.39.19.0", {"position": v(64.02, -50.07) * mm});
            skArc(sketch, "E17.40.19.0", {"start": v(61.8, -45.04) * mm, "mid": v(61.63, -44.81) * mm, "end": v(61.41, -44.62) * mm});
            skPoint(sketch, "E17.44.19.0", {"position": v(56.63, -50.99) * mm});
            skArc(sketch, "E17.45.19.0", {"start": v(56.41, -50.8) * mm, "mid": v(56.65, -50.97) * mm, "end": v(56.9, -51.1) * mm});
            skArc(sketch, "E17.2.20.0", {"start": v(65.56, -27.56) * mm, "mid": v(65.55, -28.7) * mm, "end": v(66.35, -29.54) * mm});
            skArc(sketch, "E17.4.20.0", {"start": v(62.9, -36.31) * mm, "mid": v(61.76, -36.16) * mm, "end": v(60.83, -36.84) * mm});
            skLineSegment(sketch, "E17.8.20.0", {"start": v(65.74, -37.96) * mm, "end": v(62.9, -36.31) * mm});
            skLineSegment(sketch, "E17.11.20.0", {"start": v(69.35, -30.88) * mm, "end": v(66.35, -29.54) * mm});
            skLineSegment(sketch, "E17.14.20.0", {"start": v(72.73, -36.36) * mm, "end": v(72.47, -36.93) * mm});
            skPoint(sketch, "E17.17.20.0", {"position": v(66, -38.1) * mm});
            skArc(sketch, "E17.18.20.0", {"start": v(69.82, -31.2) * mm, "mid": v(71.36, -33) * mm, "end": v(72.66, -34.98) * mm});
            skArc(sketch, "E17.22.20.0", {"start": v(66.29, -38.14) * mm, "mid": v(68.65, -38.33) * mm, "end": v(71, -38.22) * mm});
            skLineSegment(sketch, "E17.26.20.0", {"start": v(72.16, -37.47) * mm, "end": v(72.47, -36.93) * mm});
            skPoint(sketch, "E17.29.20.0", {"position": v(71.79, -38.12) * mm});
            skArc(sketch, "E17.30.20.0", {"start": v(71, -38.22) * mm, "mid": v(71.67, -37.98) * mm, "end": v(72.16, -37.47) * mm});
            skArc(sketch, "E17.34.20.0", {"start": v(72.73, -36.36) * mm, "mid": v(72.86, -35.66) * mm, "end": v(72.66, -34.98) * mm});
            skPoint(sketch, "E17.38.20.0", {"position": v(69.61, -31) * mm});
            skPoint(sketch, "E17.39.20.0", {"position": v(73.04, -35.67) * mm});
            skArc(sketch, "E17.40.20.0", {"start": v(69.82, -31.2) * mm, "mid": v(69.6, -31.02) * mm, "end": v(69.35, -30.88) * mm});
            skPoint(sketch, "E17.44.20.0", {"position": v(66, -38.1) * mm});
            skArc(sketch, "E17.45.20.0", {"start": v(65.74, -37.96) * mm, "mid": v(66, -38.08) * mm, "end": v(66.29, -38.14) * mm});
            skArc(sketch, "E17.2.21.0", {"start": v(69.86, -13.32) * mm, "mid": v(70.09, -14.45) * mm, "end": v(71.04, -15.1) * mm});
            skArc(sketch, "E17.4.21.0", {"start": v(69.07, -22.44) * mm, "mid": v(67.92, -22.53) * mm, "end": v(67.16, -23.4) * mm});
            skLineSegment(sketch, "E17.8.21.0", {"start": v(72.2, -23.46) * mm, "end": v(69.07, -22.44) * mm});
            skLineSegment(sketch, "E17.11.21.0", {"start": v(74.25, -15.78) * mm, "end": v(71.04, -15.1) * mm});
            skLineSegment(sketch, "E17.14.21.0", {"start": v(78.7, -20.44) * mm, "end": v(78.57, -21.05) * mm});
            skPoint(sketch, "E17.17.21.0", {"position": v(72.47, -23.55) * mm});
            skArc(sketch, "E17.18.21.0", {"start": v(74.79, -16) * mm, "mid": v(76.66, -17.45) * mm, "end": v(78.34, -19.1) * mm});
            skArc(sketch, "E17.22.21.0", {"start": v(72.77, -23.53) * mm, "mid": v(75.11, -23.22) * mm, "end": v(77.4, -22.62) * mm});
            skLineSegment(sketch, "E17.26.21.0", {"start": v(78.38, -21.65) * mm, "end": v(78.57, -21.05) * mm});
            skPoint(sketch, "E17.29.21.0", {"position": v(78.14, -22.36) * mm});
            skArc(sketch, "E17.30.21.0", {"start": v(77.4, -22.62) * mm, "mid": v(78, -22.25) * mm, "end": v(78.38, -21.65) * mm});
            skArc(sketch, "E17.34.21.0", {"start": v(78.7, -20.44) * mm, "mid": v(78.68, -19.73) * mm, "end": v(78.34, -19.1) * mm});
            skPoint(sketch, "E17.38.21.0", {"position": v(74.53, -15.84) * mm});
            skPoint(sketch, "E17.39.21.0", {"position": v(78.86, -19.7) * mm});
            skArc(sketch, "E17.40.21.0", {"start": v(74.79, -16) * mm, "mid": v(74.53, -15.87) * mm, "end": v(74.25, -15.78) * mm});
            skPoint(sketch, "E17.44.21.0", {"position": v(72.47, -23.55) * mm});
            skArc(sketch, "E17.45.21.0", {"start": v(72.2, -23.46) * mm, "mid": v(72.48, -23.52) * mm, "end": v(72.77, -23.53) * mm});
            skArc(sketch, "E17.2.22.0", {"start": v(71.1, 1.5) * mm, "mid": v(71.56, 0.44) * mm, "end": v(72.63, 0) * mm});
            skArc(sketch, "E17.4.22.0", {"start": v(72.23, -7.6) * mm, "mid": v(71.12, -7.91) * mm, "end": v(70.56, -8.92) * mm});
            skLineSegment(sketch, "E17.8.22.0", {"start": v(75.5, -7.93) * mm, "end": v(72.23, -7.6) * mm});
            skLineSegment(sketch, "E17.11.22.0", {"start": v(75.91, 0) * mm, "end": v(72.63, 0) * mm});
            skLineSegment(sketch, "E17.14.22.0", {"start": v(81.23, -3.63) * mm, "end": v(81.23, -4.26) * mm});
            skPoint(sketch, "E17.17.22.0", {"position": v(75.78, -7.97) * mm});
            skArc(sketch, "E17.18.22.0", {"start": v(76.48, -0.11) * mm, "mid": v(78.61, -1.13) * mm, "end": v(80.6, -2.4) * mm});
            skArc(sketch, "E17.22.22.0", {"start": v(76.07, -7.88) * mm, "mid": v(78.3, -7.1) * mm, "end": v(80.41, -6.04) * mm});
            skLineSegment(sketch, "E17.26.22.0", {"start": v(81.16, -4.88) * mm, "end": v(81.23, -4.26) * mm});
            skPoint(sketch, "E17.29.22.0", {"position": v(81.08, -5.63) * mm});
            skArc(sketch, "E17.30.22.0", {"start": v(80.41, -6.04) * mm, "mid": v(80.93, -5.55) * mm, "end": v(81.16, -4.88) * mm});
            skArc(sketch, "E17.34.22.0", {"start": v(81.23, -3.63) * mm, "mid": v(81.06, -2.94) * mm, "end": v(80.6, -2.4) * mm});
            skPoint(sketch, "E17.38.22.0", {"position": v(76.2, 0) * mm});
            skPoint(sketch, "E17.39.22.0", {"position": v(81.23, -2.88) * mm});
            skArc(sketch, "E17.40.22.0", {"start": v(76.48, -0.11) * mm, "mid": v(76.2, -0.03) * mm, "end": v(75.91, 0) * mm});
            skPoint(sketch, "E17.44.22.0", {"position": v(75.78, -7.97) * mm});
            skArc(sketch, "E17.45.22.0", {"start": v(75.5, -7.93) * mm, "mid": v(75.79, -7.94) * mm, "end": v(76.07, -7.88) * mm});
            skArc(sketch, "E17.2.23.0", {"start": v(69.24, 16.24) * mm, "mid": v(69.9, 15.3) * mm, "end": v(71.04, 15.1) * mm});
            skArc(sketch, "E17.4.23.0", {"start": v(72.23, 7.6) * mm, "mid": v(71.22, 7.05) * mm, "end": v(70.87, 5.95) * mm});
            skLineSegment(sketch, "E17.8.23.0", {"start": v(75.5, 7.93) * mm, "end": v(72.23, 7.6) * mm});
            skLineSegment(sketch, "E17.11.23.0", {"start": v(74.25, 15.78) * mm, "end": v(71.04, 15.1) * mm});
            skLineSegment(sketch, "E17.14.23.0", {"start": v(80.2, 13.34) * mm, "end": v(80.34, 12.72) * mm});
            skPoint(sketch, "E17.17.23.0", {"position": v(75.78, 7.97) * mm});
            skArc(sketch, "E17.18.23.0", {"start": v(74.83, 15.8) * mm, "mid": v(77.13, 15.24) * mm, "end": v(79.34, 14.4) * mm});
            skArc(sketch, "E17.22.23.0", {"start": v(76.05, 8.1) * mm, "mid": v(78.07, 9.34) * mm, "end": v(79.91, 10.81) * mm});
            skLineSegment(sketch, "E17.26.23.0", {"start": v(80.4, 12.1) * mm, "end": v(80.34, 12.72) * mm});
            skPoint(sketch, "E17.29.23.0", {"position": v(80.48, 11.35) * mm});
            skArc(sketch, "E17.30.23.0", {"start": v(79.91, 10.81) * mm, "mid": v(80.31, 11.4) * mm, "end": v(80.4, 12.1) * mm});
            skArc(sketch, "E17.34.23.0", {"start": v(80.2, 13.34) * mm, "mid": v(79.9, 13.98) * mm, "end": v(79.34, 14.4) * mm});
            skPoint(sketch, "E17.38.23.0", {"position": v(74.53, 15.84) * mm});
            skPoint(sketch, "E17.39.23.0", {"position": v(80.05, 14.07) * mm});
            skArc(sketch, "E17.40.23.0", {"start": v(74.83, 15.8) * mm, "mid": v(74.54, 15.82) * mm, "end": v(74.25, 15.78) * mm});
            skPoint(sketch, "E17.44.23.0", {"position": v(75.78, 7.97) * mm});
            skArc(sketch, "E17.45.23.0", {"start": v(75.5, 7.93) * mm, "mid": v(75.78, 8) * mm, "end": v(76.05, 8.1) * mm});
            skArc(sketch, "E17.2.24.0", {"start": v(64.35, 30.28) * mm, "mid": v(65.2, 29.5) * mm, "end": v(66.35, 29.54) * mm});
            skArc(sketch, "E17.4.24.0", {"start": v(69.07, 22.44) * mm, "mid": v(68.2, 21.7) * mm, "end": v(68.09, 20.55) * mm});
            skLineSegment(sketch, "E17.8.24.0", {"start": v(72.2, 23.46) * mm, "end": v(69.07, 22.44) * mm});
            skLineSegment(sketch, "E17.11.24.0", {"start": v(69.35, 30.88) * mm, "end": v(66.35, 29.54) * mm});
            skLineSegment(sketch, "E17.14.24.0", {"start": v(75.68, 29.72) * mm, "end": v(75.94, 29.15) * mm});
            skPoint(sketch, "E17.17.24.0", {"position": v(72.47, 23.55) * mm});
            skArc(sketch, "E17.18.24.0", {"start": v(69.91, 31) * mm, "mid": v(72.28, 30.94) * mm, "end": v(74.61, 30.6) * mm});
            skArc(sketch, "E17.22.24.0", {"start": v(72.7, 23.74) * mm, "mid": v(74.42, 25.37) * mm, "end": v(75.92, 27.2) * mm});
            skLineSegment(sketch, "E17.26.24.0", {"start": v(76.13, 28.56) * mm, "end": v(75.94, 29.15) * mm});
            skPoint(sketch, "E17.29.24.0", {"position": v(76.36, 27.84) * mm});
            skArc(sketch, "E17.30.24.0", {"start": v(75.92, 27.2) * mm, "mid": v(76.19, 27.85) * mm, "end": v(76.13, 28.56) * mm});
            skArc(sketch, "E17.34.24.0", {"start": v(75.68, 29.72) * mm, "mid": v(75.25, 30.28) * mm, "end": v(74.61, 30.6) * mm});
            skPoint(sketch, "E17.38.24.0", {"position": v(69.61, 31) * mm});
            skPoint(sketch, "E17.39.24.0", {"position": v(75.38, 30.4) * mm});
            skArc(sketch, "E17.40.24.0", {"start": v(69.91, 31) * mm, "mid": v(69.62, 30.97) * mm, "end": v(69.35, 30.88) * mm});
            skPoint(sketch, "E17.44.24.0", {"position": v(72.47, 23.55) * mm});
            skArc(sketch, "E17.45.24.0", {"start": v(72.2, 23.46) * mm, "mid": v(72.46, 23.57) * mm, "end": v(72.7, 23.74) * mm});
            skArc(sketch, "E17.2.25.0", {"start": v(56.65, 43) * mm, "mid": v(57.64, 42.41) * mm, "end": v(58.76, 42.69) * mm});
            skArc(sketch, "E17.4.25.0", {"start": v(62.9, 36.31) * mm, "mid": v(62.2, 35.4) * mm, "end": v(62.32, 34.26) * mm});
            skLineSegment(sketch, "E17.8.25.0", {"start": v(65.74, 37.96) * mm, "end": v(62.9, 36.31) * mm});
            skLineSegment(sketch, "E17.11.25.0", {"start": v(61.41, 44.62) * mm, "end": v(58.76, 42.69) * mm});
            skLineSegment(sketch, "E17.14.25.0", {"start": v(67.85, 44.8) * mm, "end": v(68.22, 44.3) * mm});
            skPoint(sketch, "E17.17.25.0", {"position": v(66, 38.1) * mm});
            skArc(sketch, "E17.18.25.0", {"start": v(61.94, 44.86) * mm, "mid": v(64.26, 45.3) * mm, "end": v(66.62, 45.44) * mm});
            skArc(sketch, "E17.22.25.0", {"start": v(66.18, 38.34) * mm, "mid": v(67.52, 40.28) * mm, "end": v(68.6, 42.38) * mm});
            skLineSegment(sketch, "E17.26.25.0", {"start": v(68.53, 43.76) * mm, "end": v(68.22, 44.3) * mm});
            skPoint(sketch, "E17.29.25.0", {"position": v(68.9, 43.1) * mm});
            skArc(sketch, "E17.30.25.0", {"start": v(68.6, 42.38) * mm, "mid": v(68.73, 43.08) * mm, "end": v(68.53, 43.76) * mm});
            skArc(sketch, "E17.34.25.0", {"start": v(67.85, 44.8) * mm, "mid": v(67.31, 45.27) * mm, "end": v(66.62, 45.44) * mm});
            skPoint(sketch, "E17.38.25.0", {"position": v(61.65, 44.79) * mm});
            skPoint(sketch, "E17.39.25.0", {"position": v(67.4, 45.42) * mm});
            skArc(sketch, "E17.40.25.0", {"start": v(61.94, 44.86) * mm, "mid": v(61.66, 44.77) * mm, "end": v(61.41, 44.62) * mm});
            skPoint(sketch, "E17.44.25.0", {"position": v(66, 38.1) * mm});
            skArc(sketch, "E17.45.25.0", {"start": v(65.74, 37.96) * mm, "mid": v(65.98, 38.12) * mm, "end": v(66.18, 38.34) * mm});
            skArc(sketch, "E17.2.26.0", {"start": v(46.47, 53.84) * mm, "mid": v(47.56, 53.47) * mm, "end": v(48.6, 53.97) * mm});
            skArc(sketch, "E17.4.26.0", {"start": v(53.97, 48.6) * mm, "mid": v(53.47, 47.56) * mm, "end": v(53.84, 46.47) * mm});
            skLineSegment(sketch, "E17.8.26.0", {"start": v(56.41, 50.8) * mm, "end": v(53.97, 48.6) * mm});
            skLineSegment(sketch, "E17.11.26.0", {"start": v(50.8, 56.41) * mm, "end": v(48.6, 53.97) * mm});
            skLineSegment(sketch, "E17.14.26.0", {"start": v(57.05, 57.93) * mm, "end": v(57.52, 57.52) * mm});
            skPoint(sketch, "E17.17.26.0", {"position": v(56.63, 50.99) * mm});
            skArc(sketch, "E17.18.26.0", {"start": v(51.26, 56.76) * mm, "mid": v(53.44, 57.67) * mm, "end": v(55.72, 58.3) * mm});
            skArc(sketch, "E17.22.26.0", {"start": v(56.76, 51.26) * mm, "mid": v(57.67, 53.44) * mm, "end": v(58.3, 55.72) * mm});
            skLineSegment(sketch, "E17.26.26.0", {"start": v(57.93, 57.05) * mm, "end": v(57.52, 57.52) * mm});
            skPoint(sketch, "E17.29.26.0", {"position": v(58.44, 56.5) * mm});
            skArc(sketch, "E17.30.26.0", {"start": v(58.3, 55.72) * mm, "mid": v(58.27, 56.43) * mm, "end": v(57.93, 57.05) * mm});
            skArc(sketch, "E17.34.26.0", {"start": v(57.05, 57.93) * mm, "mid": v(56.43, 58.27) * mm, "end": v(55.72, 58.3) * mm});
            skPoint(sketch, "E17.38.26.0", {"position": v(50.99, 56.63) * mm});
            skPoint(sketch, "E17.39.26.0", {"position": v(56.5, 58.44) * mm});
            skArc(sketch, "E17.40.26.0", {"start": v(51.26, 56.76) * mm, "mid": v(51, 56.6) * mm, "end": v(50.8, 56.41) * mm});
            skPoint(sketch, "E17.44.26.0", {"position": v(56.63, 50.99) * mm});
            skArc(sketch, "E17.45.26.0", {"start": v(56.41, 50.8) * mm, "mid": v(56.6, 51) * mm, "end": v(56.76, 51.26) * mm});
            skArc(sketch, "E17.2.27.0", {"start": v(34.26, 62.32) * mm, "mid": v(35.4, 62.2) * mm, "end": v(36.31, 62.9) * mm});
            skArc(sketch, "E17.4.27.0", {"start": v(42.69, 58.76) * mm, "mid": v(42.41, 57.64) * mm, "end": v(43, 56.65) * mm});
            skLineSegment(sketch, "E17.8.27.0", {"start": v(44.62, 61.41) * mm, "end": v(42.69, 58.76) * mm});
            skLineSegment(sketch, "E17.11.27.0", {"start": v(37.96, 65.74) * mm, "end": v(36.31, 62.9) * mm});
            skLineSegment(sketch, "E17.14.27.0", {"start": v(43.76, 68.53) * mm, "end": v(44.3, 68.22) * mm});
            skPoint(sketch, "E17.17.27.0", {"position": v(44.79, 61.65) * mm});
            skArc(sketch, "E17.18.27.0", {"start": v(38.34, 66.18) * mm, "mid": v(40.28, 67.52) * mm, "end": v(42.38, 68.6) * mm});
            skArc(sketch, "E17.22.27.0", {"start": v(44.86, 61.94) * mm, "mid": v(45.3, 64.26) * mm, "end": v(45.44, 66.62) * mm});
            skLineSegment(sketch, "E17.26.27.0", {"start": v(44.8, 67.85) * mm, "end": v(44.3, 68.22) * mm});
            skPoint(sketch, "E17.29.27.0", {"position": v(45.42, 67.4) * mm});
            skArc(sketch, "E17.30.27.0", {"start": v(45.44, 66.62) * mm, "mid": v(45.27, 67.31) * mm, "end": v(44.8, 67.85) * mm});
            skArc(sketch, "E17.34.27.0", {"start": v(43.76, 68.53) * mm, "mid": v(43.08, 68.73) * mm, "end": v(42.38, 68.6) * mm});
            skPoint(sketch, "E17.38.27.0", {"position": v(38.1, 66) * mm});
            skPoint(sketch, "E17.39.27.0", {"position": v(43.1, 68.9) * mm});
            skArc(sketch, "E17.40.27.0", {"start": v(38.34, 66.18) * mm, "mid": v(38.12, 65.98) * mm, "end": v(37.96, 65.74) * mm});
            skPoint(sketch, "E17.44.27.0", {"position": v(44.79, 61.65) * mm});
            skArc(sketch, "E17.45.27.0", {"start": v(44.62, 61.41) * mm, "mid": v(44.77, 61.66) * mm, "end": v(44.86, 61.94) * mm});
            skArc(sketch, "E17.2.28.0", {"start": v(20.55, 68.09) * mm, "mid": v(21.7, 68.2) * mm, "end": v(22.44, 69.07) * mm});
            skArc(sketch, "E17.4.28.0", {"start": v(29.54, 66.35) * mm, "mid": v(29.5, 65.2) * mm, "end": v(30.28, 64.35) * mm});
            skLineSegment(sketch, "E17.8.28.0", {"start": v(30.88, 69.35) * mm, "end": v(29.54, 66.35) * mm});
            skLineSegment(sketch, "E17.11.28.0", {"start": v(23.46, 72.2) * mm, "end": v(22.44, 69.07) * mm});
            skLineSegment(sketch, "E17.14.28.0", {"start": v(28.56, 76.13) * mm, "end": v(29.15, 75.94) * mm});
            skPoint(sketch, "E17.17.28.0", {"position": v(31, 69.61) * mm});
            skArc(sketch, "E17.18.28.0", {"start": v(23.74, 72.7) * mm, "mid": v(25.37, 74.42) * mm, "end": v(27.2, 75.92) * mm});
            skArc(sketch, "E17.22.28.0", {"start": v(31, 69.91) * mm, "mid": v(30.94, 72.28) * mm, "end": v(30.6, 74.61) * mm});
            skLineSegment(sketch, "E17.26.28.0", {"start": v(29.72, 75.68) * mm, "end": v(29.15, 75.94) * mm});
            skPoint(sketch, "E17.29.28.0", {"position": v(30.4, 75.38) * mm});
            skArc(sketch, "E17.30.28.0", {"start": v(30.6, 74.61) * mm, "mid": v(30.28, 75.25) * mm, "end": v(29.72, 75.68) * mm});
            skArc(sketch, "E17.34.28.0", {"start": v(28.56, 76.13) * mm, "mid": v(27.85, 76.19) * mm, "end": v(27.2, 75.92) * mm});
            skPoint(sketch, "E17.38.28.0", {"position": v(23.55, 72.47) * mm});
            skPoint(sketch, "E17.39.28.0", {"position": v(27.84, 76.36) * mm});
            skArc(sketch, "E17.40.28.0", {"start": v(23.74, 72.7) * mm, "mid": v(23.57, 72.46) * mm, "end": v(23.46, 72.2) * mm});
            skPoint(sketch, "E17.44.28.0", {"position": v(31, 69.61) * mm});
            skArc(sketch, "E17.45.28.0", {"start": v(30.88, 69.35) * mm, "mid": v(30.97, 69.62) * mm, "end": v(31, 69.91) * mm});
            skArc(sketch, "E17.2.29.0", {"start": v(5.95, 70.87) * mm, "mid": v(7.05, 71.22) * mm, "end": v(7.6, 72.23) * mm});
            skArc(sketch, "E17.4.29.0", {"start": v(15.1, 71.04) * mm, "mid": v(15.3, 69.9) * mm, "end": v(16.24, 69.24) * mm});
            skLineSegment(sketch, "E17.8.29.0", {"start": v(15.78, 74.25) * mm, "end": v(15.1, 71.04) * mm});
            skLineSegment(sketch, "E17.11.29.0", {"start": v(7.93, 75.5) * mm, "end": v(7.6, 72.23) * mm});
            skLineSegment(sketch, "E17.14.29.0", {"start": v(12.1, 80.4) * mm, "end": v(12.72, 80.34) * mm});
            skPoint(sketch, "E17.17.29.0", {"position": v(15.84, 74.53) * mm});
            skArc(sketch, "E17.18.29.0", {"start": v(8.1, 76.05) * mm, "mid": v(9.34, 78.07) * mm, "end": v(10.81, 79.91) * mm});
            skArc(sketch, "E17.22.29.0", {"start": v(15.8, 74.83) * mm, "mid": v(15.24, 77.13) * mm, "end": v(14.4, 79.34) * mm});
            skLineSegment(sketch, "E17.26.29.0", {"start": v(13.34, 80.2) * mm, "end": v(12.72, 80.34) * mm});
            skPoint(sketch, "E17.29.29.0", {"position": v(14.07, 80.05) * mm});
            skArc(sketch, "E17.30.29.0", {"start": v(14.4, 79.34) * mm, "mid": v(13.98, 79.9) * mm, "end": v(13.34, 80.2) * mm});
            skArc(sketch, "E17.34.29.0", {"start": v(12.1, 80.4) * mm, "mid": v(11.4, 80.31) * mm, "end": v(10.81, 79.91) * mm});
            skPoint(sketch, "E17.38.29.0", {"position": v(7.97, 75.78) * mm});
            skPoint(sketch, "E17.39.29.0", {"position": v(11.35, 80.48) * mm});
            skArc(sketch, "E17.40.29.0", {"start": v(8.1, 76.05) * mm, "mid": v(8, 75.78) * mm, "end": v(7.93, 75.5) * mm});
            skPoint(sketch, "E17.44.29.0", {"position": v(15.84, 74.53) * mm});
            skArc(sketch, "E17.45.29.0", {"start": v(15.78, 74.25) * mm, "mid": v(15.82, 74.54) * mm, "end": v(15.8, 74.83) * mm});
            skArc(sketch, "E18.trimOffspring", {"start": v(-23.4, 67.16) * mm, "mid": v(-25.49, 66.4) * mm, "end": v(-27.56, 65.56) * mm});
            skArc(sketch, "E19.trimOffspring", {"start": v(5.95, 70.87) * mm, "mid": v(3.72, 71.02) * mm, "end": v(1.5, 71.1) * mm});
            skArc(sketch, "E20.trimOffspring", {"start": v(20.55, 68.09) * mm, "mid": v(18.4, 68.7) * mm, "end": v(16.24, 69.24) * mm});
            skArc(sketch, "E21.trimOffspring", {"start": v(34.26, 62.32) * mm, "mid": v(32.29, 63.37) * mm, "end": v(30.28, 64.35) * mm});
            skArc(sketch, "E22.trimOffspring", {"start": v(46.47, 53.84) * mm, "mid": v(44.76, 55.27) * mm, "end": v(43, 56.65) * mm});
            skArc(sketch, "E23.trimOffspring", {"start": v(-36.84, 60.83) * mm, "mid": v(-38.73, 59.65) * mm, "end": v(-40.59, 58.4) * mm});
            skArc(sketch, "E24.trimOffspring", {"start": v(-48.69, 51.84) * mm, "mid": v(-50.29, 50.29) * mm, "end": v(-51.84, 48.69) * mm});
            skArc(sketch, "E25.trimOffspring", {"start": v(-58.4, 40.59) * mm, "mid": v(-59.65, 38.73) * mm, "end": v(-60.83, 36.84) * mm});
            skArc(sketch, "E26.trimOffspring", {"start": v(56.65, 43) * mm, "mid": v(55.27, 44.76) * mm, "end": v(53.84, 46.47) * mm});
            skArc(sketch, "E27.trimOffspring", {"start": v(-65.56, 27.56) * mm, "mid": v(-66.4, 25.49) * mm, "end": v(-67.16, 23.4) * mm});
            skArc(sketch, "E28.trimOffspring", {"start": v(64.35, 30.28) * mm, "mid": v(63.37, 32.29) * mm, "end": v(62.32, 34.26) * mm});
            skArc(sketch, "E29.trimOffspring", {"start": v(69.24, 16.24) * mm, "mid": v(68.7, 18.4) * mm, "end": v(68.09, 20.55) * mm});
            skArc(sketch, "E30.trimOffspring", {"start": v(71.1, 1.5) * mm, "mid": v(71.02, 3.72) * mm, "end": v(70.87, 5.95) * mm});
            skArc(sketch, "E31.trimOffspring", {"start": v(-69.86, 13.32) * mm, "mid": v(-70.24, 11.13) * mm, "end": v(-70.56, 8.92) * mm});
            skArc(sketch, "E32.trimOffspring", {"start": v(-71.1, -1.5) * mm, "mid": v(-71.02, -3.72) * mm, "end": v(-70.87, -5.95) * mm});
            skArc(sketch, "E33.trimOffspring", {"start": v(69.86, -13.32) * mm, "mid": v(70.24, -11.13) * mm, "end": v(70.56, -8.92) * mm});
            skArc(sketch, "E34.trimOffspring", {"start": v(-69.24, -16.24) * mm, "mid": v(-68.7, -18.4) * mm, "end": v(-68.09, -20.55) * mm});
            skArc(sketch, "E35.trimOffspring", {"start": v(65.56, -27.56) * mm, "mid": v(66.4, -25.49) * mm, "end": v(67.16, -23.4) * mm});
            skArc(sketch, "E36.trimOffspring", {"start": v(58.4, -40.59) * mm, "mid": v(59.65, -38.73) * mm, "end": v(60.83, -36.84) * mm});
            skArc(sketch, "E37.trimOffspring", {"start": v(48.69, -51.84) * mm, "mid": v(50.29, -50.29) * mm, "end": v(51.84, -48.69) * mm});
            skArc(sketch, "E38.trimOffspring", {"start": v(36.84, -60.83) * mm, "mid": v(38.73, -59.65) * mm, "end": v(40.59, -58.4) * mm});
            skArc(sketch, "E39.trimOffspring", {"start": v(23.4, -67.16) * mm, "mid": v(25.49, -66.4) * mm, "end": v(27.56, -65.56) * mm});
            skArc(sketch, "E40.trimOffspring", {"start": v(-64.35, -30.28) * mm, "mid": v(-63.37, -32.29) * mm, "end": v(-62.32, -34.26) * mm});
            skArc(sketch, "E41.trimOffspring", {"start": v(-56.65, -43) * mm, "mid": v(-55.27, -44.76) * mm, "end": v(-53.84, -46.47) * mm});
            skArc(sketch, "E42.trimOffspring", {"start": v(8.92, -70.56) * mm, "mid": v(11.13, -70.24) * mm, "end": v(13.32, -69.86) * mm});
            skArc(sketch, "E43.trimOffspring", {"start": v(-20.55, -68.09) * mm, "mid": v(-18.4, -68.7) * mm, "end": v(-16.24, -69.24) * mm});
            skArc(sketch, "E44.trimOffspring", {"start": v(-5.95, -70.87) * mm, "mid": v(-3.72, -71.02) * mm, "end": v(-1.5, -71.1) * mm});
            skArc(sketch, "E45.trimOffspring", {"start": v(-34.26, -62.32) * mm, "mid": v(-32.29, -63.37) * mm, "end": v(-30.28, -64.35) * mm});
            skArc(sketch, "E46.trimOffspring", {"start": v(-46.47, -53.84) * mm, "mid": v(-44.76, -55.27) * mm, "end": v(-43, -56.65) * mm});
            skCircle(sketch, "E47", {"center": v(0, 0) * mm, "radius": 66.04 * mm});
            skSolve(sketch);
        }
        {
            var Q0;
            Q0=qSketchRegion(id+"F0",true);
            extrude(context, id + "F1", {"entities" : qUnion([Q0]), "depth" : 127 * mm});
        }
        {
            var Q0;
            Q0=makeQuery(id+"F1.opExtrude","CAP_FACE",FACE,{"disambiguationData":[OSD([sQuery(id+"F0.wireOp",EDGE,"E0"),sQuery(id+"F0.wireOp",EDGE,"E2.trimOffspring"),sQuery(id+"F0.wireOp",EDGE,"E3"),sQuery(id+"F0.wireOp",EDGE,"E4"),sQuery(id+"F0.wireOp",EDGE,"E5.MirrorCS"),sQuery(id+"F0.wireOp",EDGE,"E6.MirrorCS"),sQuery(id+"F0.wireOp",EDGE,"E7.MirrorCS"),sQuery(id+"F0.wireOp",EDGE,"E10.filletArc"),sQuery(id+"F0.wireOp",EDGE,"E11.filletArc"),sQuery(id+"F0.wireOp",EDGE,"E12.filletArc"),sQuery(id+"F0.wireOp",EDGE,"E13.filletArc"),sQuery(id+"F0.wireOp",EDGE,"E14.filletArc"),sQuery(id+"F0.wireOp",EDGE,"E15.filletArc"),sQuery(id+"F0.wireOp",EDGE,"E16.1.0"),sQuery(id+"F0.wireOp",EDGE,"E16.1.1"),sQuery(id+"F0.wireOp",EDGE,"E16.1.2"),sQuery(id+"F0.wireOp",EDGE,"E16.1.3"),sQuery(id+"F0.wireOp",EDGE,"E16.1.4"),sQuery(id+"F0.wireOp",EDGE,"E16.1.6"),sQuery(id+"F0.wireOp",EDGE,"E16.1.7"),sQuery(id+"F0.wireOp",EDGE,"E16.1.8"),sQuery(id+"F0.wireOp",EDGE,"E16.1.10"),sQuery(id+"F0.wireOp",EDGE,"E16.1.11"),sQuery(id+"F0.wireOp",EDGE,"E16.1.14"),sQuery(id+"F0.wireOp",EDGE,"E16.1.16"),sQuery(id+"F0.wireOp",EDGE,"E16.2.0"),sQuery(id+"F0.wireOp",EDGE,"E16.2.1"),sQuery(id+"F0.wireOp",EDGE,"E16.2.2"),sQuery(id+"F0.wireOp",EDGE,"E16.2.3"),sQuery(id+"F0.wireOp",EDGE,"E16.2.4"),sQuery(id+"F0.wireOp",EDGE,"E16.2.6"),sQuery(id+"F0.wireOp",EDGE,"E16.2.7"),sQuery(id+"F0.wireOp",EDGE,"E16.2.8"),sQuery(id+"F0.wireOp",EDGE,"E16.2.10"),sQuery(id+"F0.wireOp",EDGE,"E16.2.11"),sQuery(id+"F0.wireOp",EDGE,"E16.2.14"),sQuery(id+"F0.wireOp",EDGE,"E16.2.16"),sQuery(id+"F0.wireOp",EDGE,"E17.2.3.0"),sQuery(id+"F0.wireOp",EDGE,"E17.4.3.0"),sQuery(id+"F0.wireOp",EDGE,"E17.8.3.0"),sQuery(id+"F0.wireOp",EDGE,"E17.11.3.0"),sQuery(id+"F0.wireOp",EDGE,"E17.14.3.0"),sQuery(id+"F0.wireOp",EDGE,"E17.18.3.0"),sQuery(id+"F0.wireOp",EDGE,"E17.22.3.0"),sQuery(id+"F0.wireOp",EDGE,"E17.26.3.0"),sQuery(id+"F0.wireOp",EDGE,"E17.30.3.0"),sQuery(id+"F0.wireOp",EDGE,"E17.34.3.0"),sQuery(id+"F0.wireOp",EDGE,"E17.40.3.0"),sQuery(id+"F0.wireOp",EDGE,"E17.45.3.0"),sQuery(id+"F0.wireOp",EDGE,"E17.2.4.0"),sQuery(id+"F0.wireOp",EDGE,"E17.4.4.0"),sQuery(id+"F0.wireOp",EDGE,"E17.8.4.0"),sQuery(id+"F0.wireOp",EDGE,"E17.11.4.0"),sQuery(id+"F0.wireOp",EDGE,"E17.14.4.0"),sQuery(id+"F0.wireOp",EDGE,"E17.18.4.0"),sQuery(id+"F0.wireOp",EDGE,"E17.22.4.0"),sQuery(id+"F0.wireOp",EDGE,"E17.26.4.0"),sQuery(id+"F0.wireOp",EDGE,"E17.30.4.0"),sQuery(id+"F0.wireOp",EDGE,"E17.34.4.0"),sQuery(id+"F0.wireOp",EDGE,"E17.40.4.0"),sQuery(id+"F0.wireOp",EDGE,"E17.45.4.0"),sQuery(id+"F0.wireOp",EDGE,"E17.2.5.0"),sQuery(id+"F0.wireOp",EDGE,"E17.4.5.0"),sQuery(id+"F0.wireOp",EDGE,"E17.8.5.0"),sQuery(id+"F0.wireOp",EDGE,"E17.11.5.0"),sQuery(id+"F0.wireOp",EDGE,"E17.14.5.0"),sQuery(id+"F0.wireOp",EDGE,"E17.18.5.0"),sQuery(id+"F0.wireOp",EDGE,"E17.22.5.0"),sQuery(id+"F0.wireOp",EDGE,"E17.26.5.0"),sQuery(id+"F0.wireOp",EDGE,"E17.30.5.0"),sQuery(id+"F0.wireOp",EDGE,"E17.34.5.0"),sQuery(id+"F0.wireOp",EDGE,"E17.40.5.0"),sQuery(id+"F0.wireOp",EDGE,"E17.45.5.0"),sQuery(id+"F0.wireOp",EDGE,"E17.2.6.0"),sQuery(id+"F0.wireOp",EDGE,"E17.4.6.0"),sQuery(id+"F0.wireOp",EDGE,"E17.8.6.0"),sQuery(id+"F0.wireOp",EDGE,"E17.11.6.0"),sQuery(id+"F0.wireOp",EDGE,"E17.14.6.0"),sQuery(id+"F0.wireOp",EDGE,"E17.18.6.0"),sQuery(id+"F0.wireOp",EDGE,"E17.22.6.0"),sQuery(id+"F0.wireOp",EDGE,"E17.26.6.0"),sQuery(id+"F0.wireOp",EDGE,"E17.30.6.0"),sQuery(id+"F0.wireOp",EDGE,"E17.34.6.0"),sQuery(id+"F0.wireOp",EDGE,"E17.40.6.0"),sQuery(id+"F0.wireOp",EDGE,"E17.45.6.0"),sQuery(id+"F0.wireOp",EDGE,"E17.2.7.0"),sQuery(id+"F0.wireOp",EDGE,"E17.4.7.0"),sQuery(id+"F0.wireOp",EDGE,"E17.8.7.0"),sQuery(id+"F0.wireOp",EDGE,"E17.11.7.0"),sQuery(id+"F0.wireOp",EDGE,"E17.14.7.0"),sQuery(id+"F0.wireOp",EDGE,"E17.18.7.0"),sQuery(id+"F0.wireOp",EDGE,"E17.22.7.0"),sQuery(id+"F0.wireOp",EDGE,"E17.26.7.0"),sQuery(id+"F0.wireOp",EDGE,"E17.30.7.0"),sQuery(id+"F0.wireOp",EDGE,"E17.34.7.0"),sQuery(id+"F0.wireOp",EDGE,"E17.40.7.0"),sQuery(id+"F0.wireOp",EDGE,"E17.45.7.0"),sQuery(id+"F0.wireOp",EDGE,"E17.2.8.0"),sQuery(id+"F0.wireOp",EDGE,"E17.4.8.0"),sQuery(id+"F0.wireOp",EDGE,"E17.8.8.0"),sQuery(id+"F0.wireOp",EDGE,"E17.11.8.0"),sQuery(id+"F0.wireOp",EDGE,"E17.14.8.0"),sQuery(id+"F0.wireOp",EDGE,"E17.18.8.0"),sQuery(id+"F0.wireOp",EDGE,"E17.22.8.0"),sQuery(id+"F0.wireOp",EDGE,"E17.26.8.0"),sQuery(id+"F0.wireOp",EDGE,"E17.30.8.0"),sQuery(id+"F0.wireOp",EDGE,"E17.34.8.0"),sQuery(id+"F0.wireOp",EDGE,"E17.40.8.0"),sQuery(id+"F0.wireOp",EDGE,"E17.45.8.0"),sQuery(id+"F0.wireOp",EDGE,"E17.2.9.0"),sQuery(id+"F0.wireOp",EDGE,"E17.4.9.0"),sQuery(id+"F0.wireOp",EDGE,"E17.8.9.0"),sQuery(id+"F0.wireOp",EDGE,"E17.11.9.0"),sQuery(id+"F0.wireOp",EDGE,"E17.14.9.0"),sQuery(id+"F0.wireOp",EDGE,"E17.18.9.0"),sQuery(id+"F0.wireOp",EDGE,"E17.22.9.0"),sQuery(id+"F0.wireOp",EDGE,"E17.26.9.0"),sQuery(id+"F0.wireOp",EDGE,"E17.30.9.0"),sQuery(id+"F0.wireOp",EDGE,"E17.34.9.0"),sQuery(id+"F0.wireOp",EDGE,"E17.40.9.0"),sQuery(id+"F0.wireOp",EDGE,"E17.45.9.0"),sQuery(id+"F0.wireOp",EDGE,"E17.2.10.0"),sQuery(id+"F0.wireOp",EDGE,"E17.4.10.0"),sQuery(id+"F0.wireOp",EDGE,"E17.8.10.0"),sQuery(id+"F0.wireOp",EDGE,"E17.11.10.0"),sQuery(id+"F0.wireOp",EDGE,"E17.14.10.0"),sQuery(id+"F0.wireOp",EDGE,"E17.18.10.0"),sQuery(id+"F0.wireOp",EDGE,"E17.22.10.0"),sQuery(id+"F0.wireOp",EDGE,"E17.26.10.0"),sQuery(id+"F0.wireOp",EDGE,"E17.30.10.0"),sQuery(id+"F0.wireOp",EDGE,"E17.34.10.0"),sQuery(id+"F0.wireOp",EDGE,"E17.40.10.0"),sQuery(id+"F0.wireOp",EDGE,"E17.45.10.0"),sQuery(id+"F0.wireOp",EDGE,"E17.2.11.0"),sQuery(id+"F0.wireOp",EDGE,"E17.4.11.0"),sQuery(id+"F0.wireOp",EDGE,"E17.8.11.0"),sQuery(id+"F0.wireOp",EDGE,"E17.11.11.0"),sQuery(id+"F0.wireOp",EDGE,"E17.14.11.0"),sQuery(id+"F0.wireOp",EDGE,"E17.18.11.0"),sQuery(id+"F0.wireOp",EDGE,"E17.22.11.0"),sQuery(id+"F0.wireOp",EDGE,"E17.26.11.0"),sQuery(id+"F0.wireOp",EDGE,"E17.30.11.0"),sQuery(id+"F0.wireOp",EDGE,"E17.34.11.0"),sQuery(id+"F0.wireOp",EDGE,"E17.40.11.0"),sQuery(id+"F0.wireOp",EDGE,"E17.45.11.0"),sQuery(id+"F0.wireOp",EDGE,"E17.2.12.0"),sQuery(id+"F0.wireOp",EDGE,"E17.4.12.0"),sQuery(id+"F0.wireOp",EDGE,"E17.8.12.0"),sQuery(id+"F0.wireOp",EDGE,"E17.11.12.0"),sQuery(id+"F0.wireOp",EDGE,"E17.14.12.0"),sQuery(id+"F0.wireOp",EDGE,"E17.18.12.0"),sQuery(id+"F0.wireOp",EDGE,"E17.22.12.0"),sQuery(id+"F0.wireOp",EDGE,"E17.26.12.0"),sQuery(id+"F0.wireOp",EDGE,"E17.30.12.0"),sQuery(id+"F0.wireOp",EDGE,"E17.34.12.0"),sQuery(id+"F0.wireOp",EDGE,"E17.40.12.0"),sQuery(id+"F0.wireOp",EDGE,"E17.45.12.0"),sQuery(id+"F0.wireOp",EDGE,"E17.2.13.0"),sQuery(id+"F0.wireOp",EDGE,"E17.4.13.0"),sQuery(id+"F0.wireOp",EDGE,"E17.8.13.0"),sQuery(id+"F0.wireOp",EDGE,"E17.11.13.0"),sQuery(id+"F0.wireOp",EDGE,"E17.14.13.0"),sQuery(id+"F0.wireOp",EDGE,"E17.18.13.0"),sQuery(id+"F0.wireOp",EDGE,"E17.22.13.0"),sQuery(id+"F0.wireOp",EDGE,"E17.26.13.0"),sQuery(id+"F0.wireOp",EDGE,"E17.30.13.0"),sQuery(id+"F0.wireOp",EDGE,"E17.34.13.0"),sQuery(id+"F0.wireOp",EDGE,"E17.40.13.0"),sQuery(id+"F0.wireOp",EDGE,"E17.45.13.0"),sQuery(id+"F0.wireOp",EDGE,"E17.2.14.0"),sQuery(id+"F0.wireOp",EDGE,"E17.4.14.0"),sQuery(id+"F0.wireOp",EDGE,"E17.8.14.0"),sQuery(id+"F0.wireOp",EDGE,"E17.11.14.0"),sQuery(id+"F0.wireOp",EDGE,"E17.14.14.0"),sQuery(id+"F0.wireOp",EDGE,"E17.18.14.0"),sQuery(id+"F0.wireOp",EDGE,"E17.22.14.0"),sQuery(id+"F0.wireOp",EDGE,"E17.26.14.0"),sQuery(id+"F0.wireOp",EDGE,"E17.30.14.0"),sQuery(id+"F0.wireOp",EDGE,"E17.34.14.0"),sQuery(id+"F0.wireOp",EDGE,"E17.40.14.0"),sQuery(id+"F0.wireOp",EDGE,"E17.45.14.0"),sQuery(id+"F0.wireOp",EDGE,"E17.2.15.0"),sQuery(id+"F0.wireOp",EDGE,"E17.4.15.0"),sQuery(id+"F0.wireOp",EDGE,"E17.8.15.0"),sQuery(id+"F0.wireOp",EDGE,"E17.11.15.0"),sQuery(id+"F0.wireOp",EDGE,"E17.14.15.0"),sQuery(id+"F0.wireOp",EDGE,"E17.18.15.0"),sQuery(id+"F0.wireOp",EDGE,"E17.22.15.0"),sQuery(id+"F0.wireOp",EDGE,"E17.26.15.0"),sQuery(id+"F0.wireOp",EDGE,"E17.30.15.0"),sQuery(id+"F0.wireOp",EDGE,"E17.34.15.0"),sQuery(id+"F0.wireOp",EDGE,"E17.40.15.0"),sQuery(id+"F0.wireOp",EDGE,"E17.45.15.0"),sQuery(id+"F0.wireOp",EDGE,"E17.2.16.0"),sQuery(id+"F0.wireOp",EDGE,"E17.4.16.0"),sQuery(id+"F0.wireOp",EDGE,"E17.8.16.0"),sQuery(id+"F0.wireOp",EDGE,"E17.11.16.0"),sQuery(id+"F0.wireOp",EDGE,"E17.14.16.0"),sQuery(id+"F0.wireOp",EDGE,"E17.18.16.0"),sQuery(id+"F0.wireOp",EDGE,"E17.22.16.0"),sQuery(id+"F0.wireOp",EDGE,"E17.26.16.0"),sQuery(id+"F0.wireOp",EDGE,"E17.30.16.0"),sQuery(id+"F0.wireOp",EDGE,"E17.34.16.0"),sQuery(id+"F0.wireOp",EDGE,"E17.40.16.0"),sQuery(id+"F0.wireOp",EDGE,"E17.45.16.0"),sQuery(id+"F0.wireOp",EDGE,"E17.2.17.0"),sQuery(id+"F0.wireOp",EDGE,"E17.4.17.0"),sQuery(id+"F0.wireOp",EDGE,"E17.8.17.0"),sQuery(id+"F0.wireOp",EDGE,"E17.11.17.0"),sQuery(id+"F0.wireOp",EDGE,"E17.14.17.0"),sQuery(id+"F0.wireOp",EDGE,"E17.18.17.0"),sQuery(id+"F0.wireOp",EDGE,"E17.22.17.0"),sQuery(id+"F0.wireOp",EDGE,"E17.26.17.0"),sQuery(id+"F0.wireOp",EDGE,"E17.30.17.0"),sQuery(id+"F0.wireOp",EDGE,"E17.34.17.0"),sQuery(id+"F0.wireOp",EDGE,"E17.40.17.0"),sQuery(id+"F0.wireOp",EDGE,"E17.45.17.0"),sQuery(id+"F0.wireOp",EDGE,"E17.2.18.0"),sQuery(id+"F0.wireOp",EDGE,"E17.4.18.0"),sQuery(id+"F0.wireOp",EDGE,"E17.8.18.0"),sQuery(id+"F0.wireOp",EDGE,"E17.11.18.0"),sQuery(id+"F0.wireOp",EDGE,"E17.14.18.0"),sQuery(id+"F0.wireOp",EDGE,"E17.18.18.0"),sQuery(id+"F0.wireOp",EDGE,"E17.22.18.0"),sQuery(id+"F0.wireOp",EDGE,"E17.26.18.0"),sQuery(id+"F0.wireOp",EDGE,"E17.30.18.0"),sQuery(id+"F0.wireOp",EDGE,"E17.34.18.0"),sQuery(id+"F0.wireOp",EDGE,"E17.40.18.0"),sQuery(id+"F0.wireOp",EDGE,"E17.45.18.0"),sQuery(id+"F0.wireOp",EDGE,"E17.2.19.0"),sQuery(id+"F0.wireOp",EDGE,"E17.4.19.0"),sQuery(id+"F0.wireOp",EDGE,"E17.8.19.0"),sQuery(id+"F0.wireOp",EDGE,"E17.11.19.0"),sQuery(id+"F0.wireOp",EDGE,"E17.14.19.0"),sQuery(id+"F0.wireOp",EDGE,"E17.18.19.0"),sQuery(id+"F0.wireOp",EDGE,"E17.22.19.0"),sQuery(id+"F0.wireOp",EDGE,"E17.26.19.0"),sQuery(id+"F0.wireOp",EDGE,"E17.30.19.0"),sQuery(id+"F0.wireOp",EDGE,"E17.34.19.0"),sQuery(id+"F0.wireOp",EDGE,"E17.40.19.0"),sQuery(id+"F0.wireOp",EDGE,"E17.45.19.0"),sQuery(id+"F0.wireOp",EDGE,"E17.2.20.0"),sQuery(id+"F0.wireOp",EDGE,"E17.4.20.0"),sQuery(id+"F0.wireOp",EDGE,"E17.8.20.0"),sQuery(id+"F0.wireOp",EDGE,"E17.11.20.0"),sQuery(id+"F0.wireOp",EDGE,"E17.14.20.0"),sQuery(id+"F0.wireOp",EDGE,"E17.18.20.0"),sQuery(id+"F0.wireOp",EDGE,"E17.22.20.0"),sQuery(id+"F0.wireOp",EDGE,"E17.26.20.0"),sQuery(id+"F0.wireOp",EDGE,"E17.30.20.0"),sQuery(id+"F0.wireOp",EDGE,"E17.34.20.0"),sQuery(id+"F0.wireOp",EDGE,"E17.40.20.0"),sQuery(id+"F0.wireOp",EDGE,"E17.45.20.0"),sQuery(id+"F0.wireOp",EDGE,"E17.2.21.0"),sQuery(id+"F0.wireOp",EDGE,"E17.4.21.0"),sQuery(id+"F0.wireOp",EDGE,"E17.8.21.0"),sQuery(id+"F0.wireOp",EDGE,"E17.11.21.0"),sQuery(id+"F0.wireOp",EDGE,"E17.14.21.0"),sQuery(id+"F0.wireOp",EDGE,"E17.18.21.0"),sQuery(id+"F0.wireOp",EDGE,"E17.22.21.0"),sQuery(id+"F0.wireOp",EDGE,"E17.26.21.0"),sQuery(id+"F0.wireOp",EDGE,"E17.30.21.0"),sQuery(id+"F0.wireOp",EDGE,"E17.34.21.0"),sQuery(id+"F0.wireOp",EDGE,"E17.40.21.0"),sQuery(id+"F0.wireOp",EDGE,"E17.45.21.0"),sQuery(id+"F0.wireOp",EDGE,"E17.2.22.0"),sQuery(id+"F0.wireOp",EDGE,"E17.4.22.0"),sQuery(id+"F0.wireOp",EDGE,"E17.8.22.0"),sQuery(id+"F0.wireOp",EDGE,"E17.11.22.0"),sQuery(id+"F0.wireOp",EDGE,"E17.14.22.0"),sQuery(id+"F0.wireOp",EDGE,"E17.18.22.0"),sQuery(id+"F0.wireOp",EDGE,"E17.22.22.0"),sQuery(id+"F0.wireOp",EDGE,"E17.26.22.0"),sQuery(id+"F0.wireOp",EDGE,"E17.30.22.0"),sQuery(id+"F0.wireOp",EDGE,"E17.34.22.0"),sQuery(id+"F0.wireOp",EDGE,"E17.40.22.0"),sQuery(id+"F0.wireOp",EDGE,"E17.45.22.0"),sQuery(id+"F0.wireOp",EDGE,"E17.2.23.0"),sQuery(id+"F0.wireOp",EDGE,"E17.4.23.0"),sQuery(id+"F0.wireOp",EDGE,"E17.8.23.0"),sQuery(id+"F0.wireOp",EDGE,"E17.11.23.0"),sQuery(id+"F0.wireOp",EDGE,"E17.14.23.0"),sQuery(id+"F0.wireOp",EDGE,"E17.18.23.0"),sQuery(id+"F0.wireOp",EDGE,"E17.22.23.0"),sQuery(id+"F0.wireOp",EDGE,"E17.26.23.0"),sQuery(id+"F0.wireOp",EDGE,"E17.30.23.0"),sQuery(id+"F0.wireOp",EDGE,"E17.34.23.0"),sQuery(id+"F0.wireOp",EDGE,"E17.40.23.0"),sQuery(id+"F0.wireOp",EDGE,"E17.45.23.0"),sQuery(id+"F0.wireOp",EDGE,"E17.2.24.0"),sQuery(id+"F0.wireOp",EDGE,"E17.4.24.0"),sQuery(id+"F0.wireOp",EDGE,"E17.8.24.0"),sQuery(id+"F0.wireOp",EDGE,"E17.11.24.0"),sQuery(id+"F0.wireOp",EDGE,"E17.14.24.0"),sQuery(id+"F0.wireOp",EDGE,"E17.18.24.0"),sQuery(id+"F0.wireOp",EDGE,"E17.22.24.0"),sQuery(id+"F0.wireOp",EDGE,"E17.26.24.0"),sQuery(id+"F0.wireOp",EDGE,"E17.30.24.0"),sQuery(id+"F0.wireOp",EDGE,"E17.34.24.0"),sQuery(id+"F0.wireOp",EDGE,"E17.40.24.0"),sQuery(id+"F0.wireOp",EDGE,"E17.45.24.0"),sQuery(id+"F0.wireOp",EDGE,"E17.2.25.0"),sQuery(id+"F0.wireOp",EDGE,"E17.4.25.0"),sQuery(id+"F0.wireOp",EDGE,"E17.8.25.0"),sQuery(id+"F0.wireOp",EDGE,"E17.11.25.0"),sQuery(id+"F0.wireOp",EDGE,"E17.14.25.0"),sQuery(id+"F0.wireOp",EDGE,"E17.18.25.0"),sQuery(id+"F0.wireOp",EDGE,"E17.22.25.0"),sQuery(id+"F0.wireOp",EDGE,"E17.26.25.0"),sQuery(id+"F0.wireOp",EDGE,"E17.30.25.0"),sQuery(id+"F0.wireOp",EDGE,"E17.34.25.0"),sQuery(id+"F0.wireOp",EDGE,"E17.40.25.0"),sQuery(id+"F0.wireOp",EDGE,"E17.45.25.0"),sQuery(id+"F0.wireOp",EDGE,"E17.2.26.0"),sQuery(id+"F0.wireOp",EDGE,"E17.4.26.0"),sQuery(id+"F0.wireOp",EDGE,"E17.8.26.0"),sQuery(id+"F0.wireOp",EDGE,"E17.11.26.0"),sQuery(id+"F0.wireOp",EDGE,"E17.14.26.0"),sQuery(id+"F0.wireOp",EDGE,"E17.18.26.0"),sQuery(id+"F0.wireOp",EDGE,"E17.22.26.0"),sQuery(id+"F0.wireOp",EDGE,"E17.26.26.0"),sQuery(id+"F0.wireOp",EDGE,"E17.30.26.0"),sQuery(id+"F0.wireOp",EDGE,"E17.34.26.0"),sQuery(id+"F0.wireOp",EDGE,"E17.40.26.0"),sQuery(id+"F0.wireOp",EDGE,"E17.45.26.0"),sQuery(id+"F0.wireOp",EDGE,"E17.2.27.0"),sQuery(id+"F0.wireOp",EDGE,"E17.4.27.0"),sQuery(id+"F0.wireOp",EDGE,"E17.8.27.0"),sQuery(id+"F0.wireOp",EDGE,"E17.11.27.0"),sQuery(id+"F0.wireOp",EDGE,"E17.14.27.0"),sQuery(id+"F0.wireOp",EDGE,"E17.18.27.0"),sQuery(id+"F0.wireOp",EDGE,"E17.22.27.0"),sQuery(id+"F0.wireOp",EDGE,"E17.26.27.0"),sQuery(id+"F0.wireOp",EDGE,"E17.30.27.0"),sQuery(id+"F0.wireOp",EDGE,"E17.34.27.0"),sQuery(id+"F0.wireOp",EDGE,"E17.40.27.0"),sQuery(id+"F0.wireOp",EDGE,"E17.45.27.0"),sQuery(id+"F0.wireOp",EDGE,"E17.2.28.0"),sQuery(id+"F0.wireOp",EDGE,"E17.4.28.0"),sQuery(id+"F0.wireOp",EDGE,"E17.8.28.0"),sQuery(id+"F0.wireOp",EDGE,"E17.11.28.0"),sQuery(id+"F0.wireOp",EDGE,"E17.14.28.0"),sQuery(id+"F0.wireOp",EDGE,"E17.18.28.0"),sQuery(id+"F0.wireOp",EDGE,"E17.22.28.0"),sQuery(id+"F0.wireOp",EDGE,"E17.26.28.0"),sQuery(id+"F0.wireOp",EDGE,"E17.30.28.0"),sQuery(id+"F0.wireOp",EDGE,"E17.34.28.0"),sQuery(id+"F0.wireOp",EDGE,"E17.40.28.0"),sQuery(id+"F0.wireOp",EDGE,"E17.45.28.0"),sQuery(id+"F0.wireOp",EDGE,"E17.2.29.0"),sQuery(id+"F0.wireOp",EDGE,"E17.4.29.0"),sQuery(id+"F0.wireOp",EDGE,"E17.8.29.0"),sQuery(id+"F0.wireOp",EDGE,"E17.11.29.0"),sQuery(id+"F0.wireOp",EDGE,"E17.14.29.0"),sQuery(id+"F0.wireOp",EDGE,"E17.18.29.0"),sQuery(id+"F0.wireOp",EDGE,"E17.22.29.0"),sQuery(id+"F0.wireOp",EDGE,"E17.26.29.0"),sQuery(id+"F0.wireOp",EDGE,"E17.30.29.0"),sQuery(id+"F0.wireOp",EDGE,"E17.34.29.0"),sQuery(id+"F0.wireOp",EDGE,"E17.40.29.0"),sQuery(id+"F0.wireOp",EDGE,"E17.45.29.0"),sQuery(id+"F0.wireOp",EDGE,"E18.trimOffspring"),sQuery(id+"F0.wireOp",EDGE,"E19.trimOffspring"),sQuery(id+"F0.wireOp",EDGE,"E20.trimOffspring"),sQuery(id+"F0.wireOp",EDGE,"E21.trimOffspring"),sQuery(id+"F0.wireOp",EDGE,"E22.trimOffspring"),sQuery(id+"F0.wireOp",EDGE,"E23.trimOffspring"),sQuery(id+"F0.wireOp",EDGE,"E24.trimOffspring"),sQuery(id+"F0.wireOp",EDGE,"E25.trimOffspring"),sQuery(id+"F0.wireOp",EDGE,"E26.trimOffspring"),sQuery(id+"F0.wireOp",EDGE,"E27.trimOffspring"),sQuery(id+"F0.wireOp",EDGE,"E28.trimOffspring"),sQuery(id+"F0.wireOp",EDGE,"E29.trimOffspring"),sQuery(id+"F0.wireOp",EDGE,"E30.trimOffspring"),sQuery(id+"F0.wireOp",EDGE,"E31.trimOffspring"),sQuery(id+"F0.wireOp",EDGE,"E32.trimOffspring"),sQuery(id+"F0.wireOp",EDGE,"E33.trimOffspring"),sQuery(id+"F0.wireOp",EDGE,"E34.trimOffspring"),sQuery(id+"F0.wireOp",EDGE,"E35.trimOffspring"),sQuery(id+"F0.wireOp",EDGE,"E36.trimOffspring"),sQuery(id+"F0.wireOp",EDGE,"E37.trimOffspring"),sQuery(id+"F0.wireOp",EDGE,"E38.trimOffspring"),sQuery(id+"F0.wireOp",EDGE,"E39.trimOffspring"),sQuery(id+"F0.wireOp",EDGE,"E40.trimOffspring"),sQuery(id+"F0.wireOp",EDGE,"E41.trimOffspring"),sQuery(id+"F0.wireOp",EDGE,"E42.trimOffspring"),sQuery(id+"F0.wireOp",EDGE,"E43.trimOffspring"),sQuery(id+"F0.wireOp",EDGE,"E44.trimOffspring"),sQuery(id+"F0.wireOp",EDGE,"E45.trimOffspring"),sQuery(id+"F0.wireOp",EDGE,"E46.trimOffspring"),sQuery(id+"F0.wireOp",EDGE,"E47")])],"isStart":false});
            var sketch = newSketch(context, id + "F2", { "sketchPlane" : qUnion([Q0])});
            skLineSegment(sketch, "E48.MirrorCS", {"start": v(-3.99, 63.74) * mm, "end": v(-3.89, 65.35) * mm});
            skLineSegment(sketch, "E49.MirrorCS", {"start": v(0, 63.6) * mm, "end": v(0, 65.53) * mm});
            skArc(sketch, "E50.MirrorCS", {"start": v(-3.96, 63.55) * mm, "mid": v(-3.55, 62.4) * mm, "end": v(-3.05, 61.3) * mm});
            skArc(sketch, "E51.MirrorCS", {"start": v(-0.03, 63.4) * mm, "mid": v(-0.52, 62.3) * mm, "end": v(-1.09, 61.23) * mm});
            skLineSegment(sketch, "E52.MirrorCS", {"start": v(-1.54, 60.98) * mm, "end": v(-2.07, 60.99) * mm});
            skLineSegment(sketch, "E53.MirrorCS", {"start": v(-2.61, 61.01) * mm, "end": v(-2.07, 60.99) * mm});
            skPoint(sketch, "E54.visualSharp", {"position": v(-3.85, 65.93) * mm});
            skArc(sketch, "E54.filletArc", {"start": v(-3.89, 65.35) * mm, "mid": v(-4.04, 65.74) * mm, "end": v(-4.43, 65.9) * mm});
            skPoint(sketch, "E55.visualSharp", {"position": v(0, 66.04) * mm});
            skArc(sketch, "E55.filletArc", {"start": v(0.51, 66.04) * mm, "mid": v(0.15, 65.9) * mm, "end": v(0, 65.53) * mm});
            skPoint(sketch, "E56.visualSharp", {"position": v(0, 63.5) * mm});
            skArc(sketch, "E56.filletArc", {"start": v(-0.03, 63.4) * mm, "mid": v(0, 63.5) * mm, "end": v(0, 63.6) * mm});
            skPoint(sketch, "E57.visualSharp", {"position": v(-1.24, 60.97) * mm});
            skArc(sketch, "E57.filletArc", {"start": v(-1.54, 60.98) * mm, "mid": v(-1.28, 61.04) * mm, "end": v(-1.09, 61.23) * mm});
            skPoint(sketch, "E58.visualSharp", {"position": v(-2.9, 61.02) * mm});
            skArc(sketch, "E58.filletArc", {"start": v(-3.05, 61.3) * mm, "mid": v(-2.87, 61.1) * mm, "end": v(-2.61, 61.01) * mm});
            skArc(sketch, "E59.filletArc", {"start": v(-3.99, 63.74) * mm, "mid": v(-3.99, 63.65) * mm, "end": v(-3.96, 63.55) * mm});
            skArc(sketch, "E60", {"start": v(-3.85, 65.93) * mm, "mid": v(-6.07, 65.76) * mm, "end": v(-8.28, 65.52) * mm});
            skPoint(sketch, "E61.1.0", {"position": v(-12.08, 64.93) * mm});
            skArc(sketch, "E61.1.1", {"start": v(-11.9, 62.56) * mm, "mid": v(-11.34, 61.47) * mm, "end": v(-10.7, 60.43) * mm});
            skLineSegment(sketch, "E61.1.2", {"start": v(-7.97, 63.1) * mm, "end": v(-8.21, 65.01) * mm});
            skArc(sketch, "E61.1.3", {"start": v(-7.98, 62.9) * mm, "mid": v(-8.32, 61.74) * mm, "end": v(-8.75, 60.61) * mm});
            skLineSegment(sketch, "E61.1.4", {"start": v(-11.95, 62.74) * mm, "end": v(-12.05, 64.35) * mm});
            skPoint(sketch, "E61.1.5", {"position": v(-10.53, 60.18) * mm});
            skPoint(sketch, "E61.1.6", {"position": v(-7.96, 63) * mm});
            skPoint(sketch, "E61.1.7", {"position": v(-8.87, 60.34) * mm});
            skPoint(sketch, "E61.1.8", {"position": v(-8.28, 65.52) * mm});
            skLineSegment(sketch, "E61.1.9", {"start": v(-9.17, 60.3) * mm, "end": v(-9.7, 60.25) * mm});
            skLineSegment(sketch, "E61.1.10", {"start": v(-10.24, 60.2) * mm, "end": v(-9.7, 60.25) * mm});
            skArc(sketch, "E61.1.11", {"start": v(-10.7, 60.43) * mm, "mid": v(-10.5, 60.25) * mm, "end": v(-10.24, 60.2) * mm});
            skArc(sketch, "E61.1.12", {"start": v(-7.77, 65.58) * mm, "mid": v(-8.1, 65.39) * mm, "end": v(-8.21, 65.01) * mm});
            skArc(sketch, "E61.1.13", {"start": v(-12.05, 64.35) * mm, "mid": v(-12.24, 64.72) * mm, "end": v(-12.65, 64.82) * mm});
            skArc(sketch, "E61.1.14", {"start": v(-7.98, 62.9) * mm, "mid": v(-7.97, 63) * mm, "end": v(-7.97, 63.1) * mm});
            skArc(sketch, "E61.1.15", {"start": v(-9.17, 60.3) * mm, "mid": v(-8.92, 60.4) * mm, "end": v(-8.75, 60.61) * mm});
            skArc(sketch, "E61.1.16", {"start": v(-11.95, 62.74) * mm, "mid": v(-11.93, 62.65) * mm, "end": v(-11.9, 62.56) * mm});
            skPoint(sketch, "E61.2.0", {"position": v(-20.12, 62.9) * mm});
            skArc(sketch, "E61.2.1", {"start": v(-19.65, 60.57) * mm, "mid": v(-18.96, 59.56) * mm, "end": v(-18.2, 58.6) * mm});
            skLineSegment(sketch, "E61.2.2", {"start": v(-15.82, 61.6) * mm, "end": v(-16.3, 63.47) * mm});
            skArc(sketch, "E61.2.3", {"start": v(-15.8, 61.4) * mm, "mid": v(-16, 60.21) * mm, "end": v(-16.28, 59.04) * mm});
            skLineSegment(sketch, "E61.2.4", {"start": v(-19.71, 60.75) * mm, "end": v(-20.02, 62.33) * mm});
            skPoint(sketch, "E61.2.5", {"position": v(-18, 58.38) * mm});
            skPoint(sketch, "E61.2.6", {"position": v(-15.8, 61.5) * mm});
            skPoint(sketch, "E61.2.7", {"position": v(-16.36, 58.75) * mm});
            skPoint(sketch, "E61.2.8", {"position": v(-16.42, 63.97) * mm});
            skLineSegment(sketch, "E61.2.9", {"start": v(-16.65, 58.68) * mm, "end": v(-17.18, 58.56) * mm});
            skLineSegment(sketch, "E61.2.10", {"start": v(-17.7, 58.44) * mm, "end": v(-17.18, 58.56) * mm});
            skArc(sketch, "E61.2.11", {"start": v(-18.2, 58.6) * mm, "mid": v(-17.97, 58.46) * mm, "end": v(-17.7, 58.44) * mm});
            skArc(sketch, "E61.2.12", {"start": v(-15.93, 64.1) * mm, "mid": v(-16.24, 63.86) * mm, "end": v(-16.3, 63.47) * mm});
            skArc(sketch, "E61.2.13", {"start": v(-20.02, 62.33) * mm, "mid": v(-20.26, 62.68) * mm, "end": v(-20.68, 62.72) * mm});
            skArc(sketch, "E61.2.14", {"start": v(-15.8, 61.4) * mm, "mid": v(-15.8, 61.5) * mm, "end": v(-15.82, 61.6) * mm});
            skArc(sketch, "E61.2.15", {"start": v(-16.65, 58.68) * mm, "mid": v(-16.42, 58.8) * mm, "end": v(-16.28, 59.04) * mm});
            skArc(sketch, "E61.2.16", {"start": v(-19.71, 60.75) * mm, "mid": v(-19.69, 60.66) * mm, "end": v(-19.65, 60.57) * mm});
            skArc(sketch, "E62.1.3.0", {"start": v(-27.08, 57.63) * mm, "mid": v(-26.27, 56.72) * mm, "end": v(-25.4, 55.87) * mm});
            skLineSegment(sketch, "E62.5.3.0", {"start": v(-23.41, 59.13) * mm, "end": v(-24.12, 60.93) * mm});
            skArc(sketch, "E62.8.3.0", {"start": v(-23.38, 58.94) * mm, "mid": v(-23.42, 57.73) * mm, "end": v(-23.55, 56.53) * mm});
            skPoint(sketch, "E62.9.3.0", {"position": v(-27.85, 59.88) * mm});
            skLineSegment(sketch, "E62.12.3.0", {"start": v(-27.17, 57.8) * mm, "end": v(-27.67, 59.33) * mm});
            skPoint(sketch, "E62.15.3.0", {"position": v(-25.17, 55.67) * mm});
            skPoint(sketch, "E62.16.3.0", {"position": v(-23.38, 59.04) * mm});
            skPoint(sketch, "E62.17.3.0", {"position": v(-23.6, 56.23) * mm});
            skPoint(sketch, "E62.18.3.0", {"position": v(-24.31, 61.4) * mm});
            skLineSegment(sketch, "E62.19.3.0", {"start": v(-23.87, 56.13) * mm, "end": v(-24.38, 55.94) * mm});
            skLineSegment(sketch, "E62.22.3.0", {"start": v(-24.89, 55.76) * mm, "end": v(-24.38, 55.94) * mm});
            skArc(sketch, "E62.25.3.0", {"start": v(-25.4, 55.87) * mm, "mid": v(-25.16, 55.75) * mm, "end": v(-24.89, 55.76) * mm});
            skArc(sketch, "E62.29.3.0", {"start": v(-23.83, 61.59) * mm, "mid": v(-24.12, 61.32) * mm, "end": v(-24.12, 60.93) * mm});
            skArc(sketch, "E62.33.3.0", {"start": v(-27.67, 59.33) * mm, "mid": v(-27.95, 59.64) * mm, "end": v(-28.37, 59.63) * mm});
            skArc(sketch, "E62.37.3.0", {"start": v(-23.38, 58.94) * mm, "mid": v(-23.38, 59.04) * mm, "end": v(-23.41, 59.13) * mm});
            skArc(sketch, "E62.41.3.0", {"start": v(-23.87, 56.13) * mm, "mid": v(-23.66, 56.29) * mm, "end": v(-23.55, 56.53) * mm});
            skArc(sketch, "E62.45.3.0", {"start": v(-27.17, 57.8) * mm, "mid": v(-27.14, 57.71) * mm, "end": v(-27.08, 57.63) * mm});
            skArc(sketch, "E62.1.4.0", {"start": v(-34.1, 53.78) * mm, "mid": v(-33.17, 52.98) * mm, "end": v(-32.2, 52.24) * mm});
            skLineSegment(sketch, "E62.5.4.0", {"start": v(-30.64, 55.73) * mm, "end": v(-31.57, 57.42) * mm});
            skArc(sketch, "E62.8.4.0", {"start": v(-30.58, 55.55) * mm, "mid": v(-30.47, 54.34) * mm, "end": v(-30.45, 53.13) * mm});
            skPoint(sketch, "E62.9.4.0", {"position": v(-35.14, 55.92) * mm});
            skLineSegment(sketch, "E62.12.4.0", {"start": v(-34.2, 53.94) * mm, "end": v(-34.89, 55.4) * mm});
            skPoint(sketch, "E62.15.4.0", {"position": v(-31.95, 52.07) * mm});
            skPoint(sketch, "E62.16.4.0", {"position": v(-30.6, 55.65) * mm});
            skPoint(sketch, "E62.17.4.0", {"position": v(-30.46, 52.83) * mm});
            skPoint(sketch, "E62.18.4.0", {"position": v(-31.82, 57.87) * mm});
            skLineSegment(sketch, "E62.19.4.0", {"start": v(-30.72, 52.7) * mm, "end": v(-31.2, 52.44) * mm});
            skLineSegment(sketch, "E62.22.4.0", {"start": v(-31.68, 52.2) * mm, "end": v(-31.2, 52.44) * mm});
            skArc(sketch, "E62.25.4.0", {"start": v(-32.2, 52.24) * mm, "mid": v(-31.94, 52.15) * mm, "end": v(-31.68, 52.2) * mm});
            skArc(sketch, "E62.29.4.0", {"start": v(-31.37, 58.12) * mm, "mid": v(-31.61, 57.81) * mm, "end": v(-31.57, 57.42) * mm});
            skArc(sketch, "E62.33.4.0", {"start": v(-34.89, 55.4) * mm, "mid": v(-35.2, 55.67) * mm, "end": v(-35.62, 55.6) * mm});
            skArc(sketch, "E62.37.4.0", {"start": v(-30.58, 55.55) * mm, "mid": v(-30.6, 55.64) * mm, "end": v(-30.64, 55.73) * mm});
            skArc(sketch, "E62.41.4.0", {"start": v(-30.72, 52.7) * mm, "mid": v(-30.53, 52.88) * mm, "end": v(-30.45, 53.13) * mm});
            skArc(sketch, "E62.45.4.0", {"start": v(-34.2, 53.94) * mm, "mid": v(-34.15, 53.85) * mm, "end": v(-34.1, 53.78) * mm});
            skArc(sketch, "E62.1.5.0", {"start": v(-40.56, 49.09) * mm, "mid": v(-39.55, 48.4) * mm, "end": v(-38.49, 47.8) * mm});
            skLineSegment(sketch, "E62.5.5.0", {"start": v(-37.38, 51.45) * mm, "end": v(-38.52, 53.01) * mm});
            skArc(sketch, "E62.8.5.0", {"start": v(-37.3, 51.28) * mm, "mid": v(-37.04, 50.1) * mm, "end": v(-36.87, 48.9) * mm});
            skPoint(sketch, "E62.9.5.0", {"position": v(-41.87, 51.07) * mm});
            skLineSegment(sketch, "E62.12.5.0", {"start": v(-40.7, 49.22) * mm, "end": v(-41.56, 50.59) * mm});
            skPoint(sketch, "E62.15.5.0", {"position": v(-38.22, 47.66) * mm});
            skPoint(sketch, "E62.16.5.0", {"position": v(-37.32, 51.37) * mm});
            skPoint(sketch, "E62.17.5.0", {"position": v(-36.84, 48.6) * mm});
            skPoint(sketch, "E62.18.5.0", {"position": v(-38.82, 53.43) * mm});
            skLineSegment(sketch, "E62.19.5.0", {"start": v(-37.08, 48.43) * mm, "end": v(-37.53, 48.12) * mm});
            skLineSegment(sketch, "E62.22.5.0", {"start": v(-37.98, 47.82) * mm, "end": v(-37.53, 48.12) * mm});
            skArc(sketch, "E62.25.5.0", {"start": v(-38.49, 47.8) * mm, "mid": v(-38.23, 47.74) * mm, "end": v(-37.98, 47.82) * mm});
            skArc(sketch, "E62.29.5.0", {"start": v(-38.4, 53.73) * mm, "mid": v(-38.6, 53.4) * mm, "end": v(-38.52, 53.01) * mm});
            skArc(sketch, "E62.33.5.0", {"start": v(-41.56, 50.59) * mm, "mid": v(-41.9, 50.82) * mm, "end": v(-42.31, 50.7) * mm});
            skArc(sketch, "E62.37.5.0", {"start": v(-37.3, 51.28) * mm, "mid": v(-37.33, 51.37) * mm, "end": v(-37.38, 51.45) * mm});
            skArc(sketch, "E62.41.5.0", {"start": v(-37.08, 48.43) * mm, "mid": v(-36.91, 48.63) * mm, "end": v(-36.87, 48.9) * mm});
            skArc(sketch, "E62.45.5.0", {"start": v(-40.7, 49.22) * mm, "mid": v(-40.63, 49.15) * mm, "end": v(-40.56, 49.09) * mm});
            skArc(sketch, "E62.1.6.0", {"start": v(-46.4, 43.62) * mm, "mid": v(-45.3, 43.06) * mm, "end": v(-44.18, 42.6) * mm});
            skLineSegment(sketch, "E62.5.6.0", {"start": v(-43.53, 46.36) * mm, "end": v(-44.86, 47.77) * mm});
            skArc(sketch, "E62.8.6.0", {"start": v(-43.43, 46.2) * mm, "mid": v(-43.03, 45.06) * mm, "end": v(-42.7, 43.9) * mm});
            skPoint(sketch, "E62.9.6.0", {"position": v(-47.94, 45.42) * mm});
            skLineSegment(sketch, "E62.12.6.0", {"start": v(-46.54, 43.74) * mm, "end": v(-47.57, 44.98) * mm});
            skPoint(sketch, "E62.15.6.0", {"position": v(-43.9, 42.5) * mm});
            skPoint(sketch, "E62.16.6.0", {"position": v(-43.47, 46.29) * mm});
            skPoint(sketch, "E62.17.6.0", {"position": v(-42.64, 43.6) * mm});
            skPoint(sketch, "E62.18.6.0", {"position": v(-45.2, 48.14) * mm});
            skLineSegment(sketch, "E62.19.6.0", {"start": v(-42.86, 43.4) * mm, "end": v(-43.26, 43.04) * mm});
            skLineSegment(sketch, "E62.22.6.0", {"start": v(-43.67, 42.69) * mm, "end": v(-43.26, 43.04) * mm});
            skArc(sketch, "E62.25.6.0", {"start": v(-44.18, 42.6) * mm, "mid": v(-43.91, 42.57) * mm, "end": v(-43.67, 42.69) * mm});
            skArc(sketch, "E62.29.6.0", {"start": v(-44.83, 48.5) * mm, "mid": v(-45, 48.14) * mm, "end": v(-44.86, 47.77) * mm});
            skArc(sketch, "E62.33.6.0", {"start": v(-47.57, 44.98) * mm, "mid": v(-47.95, 45.16) * mm, "end": v(-48.33, 45) * mm});
            skArc(sketch, "E62.37.6.0", {"start": v(-43.43, 46.2) * mm, "mid": v(-43.48, 46.28) * mm, "end": v(-43.53, 46.36) * mm});
            skArc(sketch, "E62.41.6.0", {"start": v(-42.86, 43.4) * mm, "mid": v(-42.72, 43.62) * mm, "end": v(-42.7, 43.9) * mm});
            skArc(sketch, "E62.45.6.0", {"start": v(-46.54, 43.74) * mm, "mid": v(-46.47, 43.67) * mm, "end": v(-46.4, 43.62) * mm});
            skArc(sketch, "E62.1.7.0", {"start": v(-51.5, 37.46) * mm, "mid": v(-50.35, 37.04) * mm, "end": v(-49.17, 36.72) * mm});
            skLineSegment(sketch, "E62.5.7.0", {"start": v(-49, 40.54) * mm, "end": v(-50.5, 41.77) * mm});
            skArc(sketch, "E62.8.7.0", {"start": v(-48.88, 40.4) * mm, "mid": v(-48.33, 39.31) * mm, "end": v(-47.87, 38.2) * mm});
            skPoint(sketch, "E62.9.7.0", {"position": v(-53.25, 39.06) * mm});
            skLineSegment(sketch, "E62.12.7.0", {"start": v(-51.66, 37.56) * mm, "end": v(-52.83, 38.66) * mm});
            skPoint(sketch, "E62.15.7.0", {"position": v(-48.87, 36.66) * mm});
            skPoint(sketch, "E62.16.7.0", {"position": v(-48.93, 40.48) * mm});
            skPoint(sketch, "E62.17.7.0", {"position": v(-47.77, 37.9) * mm});
            skPoint(sketch, "E62.18.7.0", {"position": v(-50.88, 42.1) * mm});
            skLineSegment(sketch, "E62.19.7.0", {"start": v(-47.96, 37.69) * mm, "end": v(-48.31, 37.28) * mm});
            skLineSegment(sketch, "E62.22.7.0", {"start": v(-48.68, 36.88) * mm, "end": v(-48.31, 37.28) * mm});
            skArc(sketch, "E62.25.7.0", {"start": v(-49.17, 36.72) * mm, "mid": v(-48.9, 36.73) * mm, "end": v(-48.68, 36.88) * mm});
            skArc(sketch, "E62.29.7.0", {"start": v(-50.56, 42.49) * mm, "mid": v(-50.67, 42.12) * mm, "end": v(-50.5, 41.77) * mm});
            skArc(sketch, "E62.33.7.0", {"start": v(-52.83, 38.66) * mm, "mid": v(-53.23, 38.8) * mm, "end": v(-53.6, 38.59) * mm});
            skArc(sketch, "E62.37.7.0", {"start": v(-48.88, 40.4) * mm, "mid": v(-48.93, 40.47) * mm, "end": v(-49, 40.54) * mm});
            skArc(sketch, "E62.41.7.0", {"start": v(-47.96, 37.69) * mm, "mid": v(-47.85, 37.93) * mm, "end": v(-47.87, 38.2) * mm});
            skArc(sketch, "E62.45.7.0", {"start": v(-51.66, 37.56) * mm, "mid": v(-51.58, 37.5) * mm, "end": v(-51.5, 37.46) * mm});
            skArc(sketch, "E62.1.8.0", {"start": v(-55.79, 30.7) * mm, "mid": v(-54.6, 30.44) * mm, "end": v(-53.38, 30.27) * mm});
            skLineSegment(sketch, "E62.5.8.0", {"start": v(-53.7, 34.08) * mm, "end": v(-55.33, 35.11) * mm});
            skArc(sketch, "E62.8.8.0", {"start": v(-53.56, 33.95) * mm, "mid": v(-52.88, 32.94) * mm, "end": v(-52.28, 31.9) * mm});
            skPoint(sketch, "E62.9.8.0", {"position": v(-57.73, 32.07) * mm});
            skLineSegment(sketch, "E62.12.8.0", {"start": v(-55.96, 30.79) * mm, "end": v(-57.26, 31.74) * mm});
            skPoint(sketch, "E62.15.8.0", {"position": v(-53.08, 30.24) * mm});
            skPoint(sketch, "E62.16.8.0", {"position": v(-53.61, 34.03) * mm});
            skPoint(sketch, "E62.17.8.0", {"position": v(-52.14, 31.62) * mm});
            skPoint(sketch, "E62.18.8.0", {"position": v(-55.76, 35.39) * mm});
            skLineSegment(sketch, "E62.19.8.0", {"start": v(-52.3, 31.38) * mm, "end": v(-52.6, 30.93) * mm});
            skLineSegment(sketch, "E62.22.8.0", {"start": v(-52.91, 30.49) * mm, "end": v(-52.6, 30.93) * mm});
            skArc(sketch, "E62.25.8.0", {"start": v(-53.38, 30.27) * mm, "mid": v(-53.12, 30.31) * mm, "end": v(-52.91, 30.49) * mm});
            skArc(sketch, "E62.29.8.0", {"start": v(-55.48, 35.82) * mm, "mid": v(-55.55, 35.43) * mm, "end": v(-55.33, 35.11) * mm});
            skArc(sketch, "E62.33.8.0", {"start": v(-57.26, 31.74) * mm, "mid": v(-57.67, 31.82) * mm, "end": v(-58, 31.57) * mm});
            skArc(sketch, "E62.37.8.0", {"start": v(-53.56, 33.95) * mm, "mid": v(-53.62, 34.02) * mm, "end": v(-53.7, 34.08) * mm});
            skArc(sketch, "E62.41.8.0", {"start": v(-52.3, 31.38) * mm, "mid": v(-52.22, 31.63) * mm, "end": v(-52.28, 31.9) * mm});
            skArc(sketch, "E62.45.8.0", {"start": v(-55.96, 30.79) * mm, "mid": v(-55.87, 30.74) * mm, "end": v(-55.79, 30.7) * mm});
            skArc(sketch, "E62.1.9.0", {"start": v(-59.2, 23.47) * mm, "mid": v(-57.98, 23.36) * mm, "end": v(-56.75, 23.34) * mm});
            skLineSegment(sketch, "E62.5.9.0", {"start": v(-57.54, 27.08) * mm, "end": v(-59.3, 27.9) * mm});
            skArc(sketch, "E62.8.9.0", {"start": v(-57.39, 26.97) * mm, "mid": v(-56.6, 26.06) * mm, "end": v(-55.87, 25.09) * mm});
            skPoint(sketch, "E62.9.9.0", {"position": v(-61.3, 24.59) * mm});
            skLineSegment(sketch, "E62.12.9.0", {"start": v(-59.37, 23.53) * mm, "end": v(-60.79, 24.3) * mm});
            skPoint(sketch, "E62.15.9.0", {"position": v(-56.45, 23.35) * mm});
            skPoint(sketch, "E62.16.9.0", {"position": v(-57.46, 27.04) * mm});
            skPoint(sketch, "E62.17.9.0", {"position": v(-55.7, 24.84) * mm});
            skPoint(sketch, "E62.18.9.0", {"position": v(-59.75, 28.12) * mm});
            skLineSegment(sketch, "E62.19.9.0", {"start": v(-55.83, 24.57) * mm, "end": v(-56.07, 24.1) * mm});
            skLineSegment(sketch, "E62.22.9.0", {"start": v(-56.32, 23.61) * mm, "end": v(-56.07, 24.1) * mm});
            skArc(sketch, "E62.25.9.0", {"start": v(-56.75, 23.34) * mm, "mid": v(-56.5, 23.42) * mm, "end": v(-56.32, 23.61) * mm});
            skArc(sketch, "E62.29.9.0", {"start": v(-59.54, 28.58) * mm, "mid": v(-59.56, 28.2) * mm, "end": v(-59.3, 27.9) * mm});
            skArc(sketch, "E62.33.9.0", {"start": v(-60.79, 24.3) * mm, "mid": v(-61.2, 24.34) * mm, "end": v(-61.5, 24.05) * mm});
            skArc(sketch, "E62.37.9.0", {"start": v(-57.39, 26.97) * mm, "mid": v(-57.46, 27.03) * mm, "end": v(-57.54, 27.08) * mm});
            skArc(sketch, "E62.41.9.0", {"start": v(-55.83, 24.57) * mm, "mid": v(-55.78, 24.84) * mm, "end": v(-55.87, 25.09) * mm});
            skArc(sketch, "E62.45.9.0", {"start": v(-59.37, 23.53) * mm, "mid": v(-59.29, 23.5) * mm, "end": v(-59.2, 23.47) * mm});
            skArc(sketch, "E62.1.10.0", {"start": v(-61.67, 15.87) * mm, "mid": v(-60.45, 15.9) * mm, "end": v(-59.23, 16.04) * mm});
            skLineSegment(sketch, "E62.5.10.0", {"start": v(-60.48, 19.65) * mm, "end": v(-62.32, 20.25) * mm});
            skArc(sketch, "E62.8.10.0", {"start": v(-60.32, 19.56) * mm, "mid": v(-59.41, 18.76) * mm, "end": v(-58.57, 17.89) * mm});
            skPoint(sketch, "E62.9.10.0", {"position": v(-63.9, 16.71) * mm});
            skLineSegment(sketch, "E62.12.10.0", {"start": v(-61.85, 15.9) * mm, "end": v(-63.36, 16.5) * mm});
            skPoint(sketch, "E62.15.10.0", {"position": v(-58.94, 16.1) * mm});
            skPoint(sketch, "E62.16.10.0", {"position": v(-60.4, 19.62) * mm});
            skPoint(sketch, "E62.17.10.0", {"position": v(-58.37, 17.66) * mm});
            skPoint(sketch, "E62.18.10.0", {"position": v(-62.8, 20.4) * mm});
            skLineSegment(sketch, "E62.19.10.0", {"start": v(-58.47, 17.38) * mm, "end": v(-58.64, 16.87) * mm});
            skLineSegment(sketch, "E62.22.10.0", {"start": v(-58.83, 16.37) * mm, "end": v(-58.64, 16.87) * mm});
            skArc(sketch, "E62.25.10.0", {"start": v(-59.23, 16.04) * mm, "mid": v(-58.99, 16.15) * mm, "end": v(-58.83, 16.37) * mm});
            skArc(sketch, "E62.29.10.0", {"start": v(-62.65, 20.9) * mm, "mid": v(-62.62, 20.5) * mm, "end": v(-62.32, 20.25) * mm});
            skArc(sketch, "E62.33.10.0", {"start": v(-63.36, 16.5) * mm, "mid": v(-63.77, 16.48) * mm, "end": v(-64.03, 16.15) * mm});
            skArc(sketch, "E62.37.10.0", {"start": v(-60.32, 19.56) * mm, "mid": v(-60.4, 19.61) * mm, "end": v(-60.48, 19.65) * mm});
            skArc(sketch, "E62.41.10.0", {"start": v(-58.47, 17.38) * mm, "mid": v(-58.45, 17.65) * mm, "end": v(-58.57, 17.89) * mm});
            skArc(sketch, "E62.45.10.0", {"start": v(-61.85, 15.9) * mm, "mid": v(-61.76, 15.88) * mm, "end": v(-61.67, 15.87) * mm});
            skArc(sketch, "E62.1.11.0", {"start": v(-63.17, 8.01) * mm, "mid": v(-61.97, 8.2) * mm, "end": v(-60.78, 8.5) * mm});
            skLineSegment(sketch, "E62.5.11.0", {"start": v(-62.47, 11.92) * mm, "end": v(-64.37, 12.28) * mm});
            skArc(sketch, "E62.8.11.0", {"start": v(-62.3, 11.85) * mm, "mid": v(-61.3, 11.16) * mm, "end": v(-60.35, 10.4) * mm});
            skPoint(sketch, "E62.9.11.0", {"position": v(-65.48, 8.57) * mm});
            skLineSegment(sketch, "E62.12.11.0", {"start": v(-63.36, 8.03) * mm, "end": v(-64.92, 8.43) * mm});
            skPoint(sketch, "E62.15.11.0", {"position": v(-60.49, 8.58) * mm});
            skPoint(sketch, "E62.16.11.0", {"position": v(-62.38, 11.9) * mm});
            skPoint(sketch, "E62.17.11.0", {"position": v(-60.12, 10.2) * mm});
            skPoint(sketch, "E62.18.11.0", {"position": v(-64.87, 12.37) * mm});
            skLineSegment(sketch, "E62.19.11.0", {"start": v(-60.18, 9.92) * mm, "end": v(-60.3, 9.4) * mm});
            skLineSegment(sketch, "E62.22.11.0", {"start": v(-60.42, 8.87) * mm, "end": v(-60.3, 9.4) * mm});
            skArc(sketch, "E62.25.11.0", {"start": v(-60.78, 8.5) * mm, "mid": v(-60.55, 8.63) * mm, "end": v(-60.42, 8.87) * mm});
            skArc(sketch, "E62.29.11.0", {"start": v(-64.77, 12.88) * mm, "mid": v(-64.7, 12.5) * mm, "end": v(-64.37, 12.28) * mm});
            skArc(sketch, "E62.33.11.0", {"start": v(-64.92, 8.43) * mm, "mid": v(-65.34, 8.36) * mm, "end": v(-65.55, 8) * mm});
            skArc(sketch, "E62.37.11.0", {"start": v(-62.3, 11.85) * mm, "mid": v(-62.38, 11.9) * mm, "end": v(-62.47, 11.92) * mm});
            skArc(sketch, "E62.41.11.0", {"start": v(-60.18, 9.92) * mm, "mid": v(-60.2, 10.18) * mm, "end": v(-60.35, 10.4) * mm});
            skArc(sketch, "E62.45.11.0", {"start": v(-63.36, 8.03) * mm, "mid": v(-63.27, 8.01) * mm, "end": v(-63.17, 8.01) * mm});
            skArc(sketch, "E62.1.12.0", {"start": v(-63.68, 0.03) * mm, "mid": v(-62.5, 0.38) * mm, "end": v(-61.36, 0.8) * mm});
            skLineSegment(sketch, "E62.5.12.0", {"start": v(-63.47, 4) * mm, "end": v(-65.4, 4.11) * mm});
            skArc(sketch, "E62.8.12.0", {"start": v(-63.29, 3.95) * mm, "mid": v(-62.2, 3.4) * mm, "end": v(-61.18, 2.76) * mm});
            skPoint(sketch, "E62.9.12.0", {"position": v(-66.04, 0.3) * mm});
            skLineSegment(sketch, "E62.12.12.0", {"start": v(-63.87, 0.02) * mm, "end": v(-65.47, 0.22) * mm});
            skPoint(sketch, "E62.15.12.0", {"position": v(-61.09, 0.93) * mm});
            skPoint(sketch, "E62.16.12.0", {"position": v(-63.37, 3.99) * mm});
            skPoint(sketch, "E62.17.12.0", {"position": v(-60.93, 2.6) * mm});
            skPoint(sketch, "E62.18.12.0", {"position": v(-65.9, 4.15) * mm});
            skLineSegment(sketch, "E62.19.12.0", {"start": v(-60.95, 2.3) * mm, "end": v(-61, 1.76) * mm});
            skLineSegment(sketch, "E62.22.12.0", {"start": v(-61.05, 1.22) * mm, "end": v(-61, 1.76) * mm});
            skArc(sketch, "E62.25.12.0", {"start": v(-61.36, 0.8) * mm, "mid": v(-61.15, 0.97) * mm, "end": v(-61.05, 1.22) * mm});
            skArc(sketch, "E62.29.12.0", {"start": v(-65.88, 4.66) * mm, "mid": v(-65.75, 4.29) * mm, "end": v(-65.4, 4.11) * mm});
            skArc(sketch, "E62.33.12.0", {"start": v(-65.47, 0.22) * mm, "mid": v(-65.87, 0.1) * mm, "end": v(-66.04, -0.28) * mm});
            skArc(sketch, "E62.37.12.0", {"start": v(-63.29, 3.95) * mm, "mid": v(-63.38, 3.98) * mm, "end": v(-63.47, 4) * mm});
            skArc(sketch, "E62.41.12.0", {"start": v(-60.95, 2.3) * mm, "mid": v(-61, 2.56) * mm, "end": v(-61.18, 2.76) * mm});
            skArc(sketch, "E62.45.12.0", {"start": v(-63.87, 0.02) * mm, "mid": v(-63.77, 0.02) * mm, "end": v(-63.68, 0.03) * mm});
            skArc(sketch, "E62.1.13.0", {"start": v(-63.18, -7.95) * mm, "mid": v(-62.06, -7.46) * mm, "end": v(-60.98, -6.89) * mm});
            skLineSegment(sketch, "E62.5.13.0", {"start": v(-63.47, -4) * mm, "end": v(-65.4, -4.11) * mm});
            skArc(sketch, "E62.8.13.0", {"start": v(-63.28, -4.02) * mm, "mid": v(-62.14, -4.43) * mm, "end": v(-61.04, -4.93) * mm});
            skPoint(sketch, "E62.9.13.0", {"position": v(-65.56, -7.98) * mm});
            skLineSegment(sketch, "E62.12.13.0", {"start": v(-63.37, -7.98) * mm, "end": v(-64.98, -7.98) * mm});
            skPoint(sketch, "E62.15.13.0", {"position": v(-60.72, -6.73) * mm});
            skPoint(sketch, "E62.16.13.0", {"position": v(-63.37, -3.99) * mm});
            skPoint(sketch, "E62.17.13.0", {"position": v(-60.77, -5.07) * mm});
            skPoint(sketch, "E62.18.13.0", {"position": v(-65.9, -4.15) * mm});
            skLineSegment(sketch, "E62.19.13.0", {"start": v(-60.76, -5.36) * mm, "end": v(-60.74, -5.9) * mm});
            skLineSegment(sketch, "E62.22.13.0", {"start": v(-60.73, -6.44) * mm, "end": v(-60.74, -5.9) * mm});
            skArc(sketch, "E62.25.13.0", {"start": v(-60.98, -6.89) * mm, "mid": v(-60.8, -6.7) * mm, "end": v(-60.73, -6.44) * mm});
            skArc(sketch, "E62.29.13.0", {"start": v(-65.94, -3.64) * mm, "mid": v(-65.77, -3.99) * mm, "end": v(-65.4, -4.11) * mm});
            skArc(sketch, "E62.33.13.0", {"start": v(-64.98, -7.98) * mm, "mid": v(-65.36, -8.16) * mm, "end": v(-65.48, -8.56) * mm});
            skArc(sketch, "E62.37.13.0", {"start": v(-63.28, -4.02) * mm, "mid": v(-63.37, -4) * mm, "end": v(-63.47, -4) * mm});
            skArc(sketch, "E62.41.13.0", {"start": v(-60.76, -5.36) * mm, "mid": v(-60.84, -5.1) * mm, "end": v(-61.04, -4.93) * mm});
            skArc(sketch, "E62.45.13.0", {"start": v(-63.37, -7.98) * mm, "mid": v(-63.27, -7.97) * mm, "end": v(-63.18, -7.95) * mm});
            skArc(sketch, "E62.1.14.0", {"start": v(-61.69, -15.8) * mm, "mid": v(-60.64, -15.18) * mm, "end": v(-59.64, -14.48) * mm});
            skLineSegment(sketch, "E62.5.14.0", {"start": v(-62.47, -11.92) * mm, "end": v(-64.37, -12.28) * mm});
            skArc(sketch, "E62.8.14.0", {"start": v(-62.28, -11.92) * mm, "mid": v(-61.1, -12.18) * mm, "end": v(-59.94, -12.54) * mm});
            skPoint(sketch, "E62.9.14.0", {"position": v(-64.04, -16.14) * mm});
            skLineSegment(sketch, "E62.12.14.0", {"start": v(-61.86, -15.86) * mm, "end": v(-63.47, -16.06) * mm});
            skPoint(sketch, "E62.15.14.0", {"position": v(-59.4, -14.3) * mm});
            skPoint(sketch, "E62.16.14.0", {"position": v(-62.38, -11.9) * mm});
            skPoint(sketch, "E62.17.14.0", {"position": v(-59.66, -12.64) * mm});
            skPoint(sketch, "E62.18.14.0", {"position": v(-64.87, -12.37) * mm});
            skLineSegment(sketch, "E62.19.14.0", {"start": v(-59.6, -12.93) * mm, "end": v(-59.52, -13.47) * mm});
            skLineSegment(sketch, "E62.22.14.0", {"start": v(-59.44, -14) * mm, "end": v(-59.52, -13.47) * mm});
            skArc(sketch, "E62.25.14.0", {"start": v(-59.64, -14.48) * mm, "mid": v(-59.47, -14.26) * mm, "end": v(-59.44, -14) * mm});
            skArc(sketch, "E62.29.14.0", {"start": v(-64.96, -11.87) * mm, "mid": v(-64.75, -12.2) * mm, "end": v(-64.37, -12.28) * mm});
            skArc(sketch, "E62.33.14.0", {"start": v(-63.47, -16.06) * mm, "mid": v(-63.82, -16.28) * mm, "end": v(-63.9, -16.7) * mm});
            skArc(sketch, "E62.37.14.0", {"start": v(-62.28, -11.92) * mm, "mid": v(-62.37, -11.9) * mm, "end": v(-62.47, -11.92) * mm});
            skArc(sketch, "E62.41.14.0", {"start": v(-59.6, -12.93) * mm, "mid": v(-59.72, -12.7) * mm, "end": v(-59.94, -12.54) * mm});
            skArc(sketch, "E62.45.14.0", {"start": v(-61.86, -15.86) * mm, "mid": v(-61.77, -15.84) * mm, "end": v(-61.69, -15.8) * mm});
            skArc(sketch, "E62.1.15.0", {"start": v(-59.22, -23.41) * mm, "mid": v(-58.25, -22.66) * mm, "end": v(-57.35, -21.84) * mm});
            skLineSegment(sketch, "E62.5.15.0", {"start": v(-60.48, -19.65) * mm, "end": v(-62.32, -20.25) * mm});
            skArc(sketch, "E62.8.15.0", {"start": v(-60.3, -19.63) * mm, "mid": v(-59.1, -19.75) * mm, "end": v(-57.9, -19.95) * mm});
            skPoint(sketch, "E62.9.15.0", {"position": v(-61.51, -24.03) * mm});
            skLineSegment(sketch, "E62.12.15.0", {"start": v(-59.39, -23.49) * mm, "end": v(-60.95, -23.9) * mm});
            skPoint(sketch, "E62.15.15.0", {"position": v(-57.14, -21.62) * mm});
            skPoint(sketch, "E62.16.15.0", {"position": v(-60.4, -19.62) * mm});
            skPoint(sketch, "E62.17.15.0", {"position": v(-57.6, -20.02) * mm});
            skPoint(sketch, "E62.18.15.0", {"position": v(-62.8, -20.4) * mm});
            skLineSegment(sketch, "E62.19.15.0", {"start": v(-57.52, -20.3) * mm, "end": v(-57.36, -20.82) * mm});
            skLineSegment(sketch, "E62.22.15.0", {"start": v(-57.22, -21.34) * mm, "end": v(-57.36, -20.82) * mm});
            skArc(sketch, "E62.25.15.0", {"start": v(-57.35, -21.84) * mm, "mid": v(-57.22, -21.6) * mm, "end": v(-57.22, -21.34) * mm});
            skArc(sketch, "E62.29.15.0", {"start": v(-62.96, -19.92) * mm, "mid": v(-62.71, -20.22) * mm, "end": v(-62.32, -20.25) * mm});
            skArc(sketch, "E62.33.15.0", {"start": v(-60.95, -23.9) * mm, "mid": v(-61.28, -24.15) * mm, "end": v(-61.3, -24.57) * mm});
            skArc(sketch, "E62.37.15.0", {"start": v(-60.3, -19.63) * mm, "mid": v(-60.4, -19.63) * mm, "end": v(-60.48, -19.65) * mm});
            skArc(sketch, "E62.41.15.0", {"start": v(-57.52, -20.3) * mm, "mid": v(-57.66, -20.08) * mm, "end": v(-57.9, -19.95) * mm});
            skArc(sketch, "E62.45.15.0", {"start": v(-59.39, -23.49) * mm, "mid": v(-59.3, -23.46) * mm, "end": v(-59.22, -23.41) * mm});
            skArc(sketch, "E62.1.16.0", {"start": v(-55.82, -30.65) * mm, "mid": v(-54.96, -29.78) * mm, "end": v(-54.16, -28.85) * mm});
            skLineSegment(sketch, "E62.5.16.0", {"start": v(-57.54, -27.08) * mm, "end": v(-59.3, -27.9) * mm});
            skArc(sketch, "E62.8.16.0", {"start": v(-57.36, -27.03) * mm, "mid": v(-56.15, -27) * mm, "end": v(-54.94, -27.05) * mm});
            skPoint(sketch, "E62.9.16.0", {"position": v(-58.01, -31.55) * mm});
            skLineSegment(sketch, "E62.12.16.0", {"start": v(-55.98, -30.75) * mm, "end": v(-57.48, -31.34) * mm});
            skPoint(sketch, "E62.15.16.0", {"position": v(-53.98, -28.61) * mm});
            skPoint(sketch, "E62.16.16.0", {"position": v(-57.46, -27.04) * mm});
            skPoint(sketch, "E62.17.16.0", {"position": v(-54.64, -27.08) * mm});
            skPoint(sketch, "E62.18.16.0", {"position": v(-59.75, -28.12) * mm});
            skLineSegment(sketch, "E62.19.16.0", {"start": v(-54.52, -27.35) * mm, "end": v(-54.3, -27.84) * mm});
            skLineSegment(sketch, "E62.22.16.0", {"start": v(-54.1, -28.34) * mm, "end": v(-54.3, -27.84) * mm});
            skArc(sketch, "E62.25.16.0", {"start": v(-54.16, -28.85) * mm, "mid": v(-54.06, -28.6) * mm, "end": v(-54.1, -28.34) * mm});
            skArc(sketch, "E62.29.16.0", {"start": v(-59.97, -27.65) * mm, "mid": v(-59.68, -27.92) * mm, "end": v(-59.3, -27.9) * mm});
            skArc(sketch, "E62.33.16.0", {"start": v(-57.48, -31.34) * mm, "mid": v(-57.77, -31.64) * mm, "end": v(-57.74, -32.06) * mm});
            skArc(sketch, "E62.37.16.0", {"start": v(-57.36, -27.03) * mm, "mid": v(-57.45, -27.05) * mm, "end": v(-57.54, -27.08) * mm});
            skArc(sketch, "E62.41.16.0", {"start": v(-54.52, -27.35) * mm, "mid": v(-54.69, -27.15) * mm, "end": v(-54.94, -27.05) * mm});
            skArc(sketch, "E62.45.16.0", {"start": v(-55.98, -30.75) * mm, "mid": v(-55.9, -30.7) * mm, "end": v(-55.82, -30.65) * mm});
            skArc(sketch, "E62.1.17.0", {"start": v(-51.54, -37.4) * mm, "mid": v(-50.79, -36.43) * mm, "end": v(-50.12, -35.41) * mm});
            skLineSegment(sketch, "E62.5.17.0", {"start": v(-53.7, -34.08) * mm, "end": v(-55.33, -35.11) * mm});
            skArc(sketch, "E62.8.17.0", {"start": v(-53.52, -34) * mm, "mid": v(-52.32, -33.82) * mm, "end": v(-51.12, -33.73) * mm});
            skPoint(sketch, "E62.9.17.0", {"position": v(-53.6, -38.58) * mm});
            skLineSegment(sketch, "E62.12.17.0", {"start": v(-51.68, -37.52) * mm, "end": v(-53.1, -38.3) * mm});
            skPoint(sketch, "E62.15.17.0", {"position": v(-49.97, -35.15) * mm});
            skPoint(sketch, "E62.16.17.0", {"position": v(-53.61, -34.03) * mm});
            skPoint(sketch, "E62.17.17.0", {"position": v(-50.82, -33.72) * mm});
            skPoint(sketch, "E62.18.17.0", {"position": v(-55.76, -35.39) * mm});
            skLineSegment(sketch, "E62.19.17.0", {"start": v(-50.66, -33.97) * mm, "end": v(-50.38, -34.43) * mm});
            skLineSegment(sketch, "E62.22.17.0", {"start": v(-50.11, -34.9) * mm, "end": v(-50.38, -34.43) * mm});
            skArc(sketch, "E62.25.17.0", {"start": v(-50.12, -35.41) * mm, "mid": v(-50.05, -35.16) * mm, "end": v(-50.11, -34.9) * mm});
            skArc(sketch, "E62.29.17.0", {"start": v(-56.03, -34.95) * mm, "mid": v(-55.71, -35.18) * mm, "end": v(-55.33, -35.11) * mm});
            skArc(sketch, "E62.33.17.0", {"start": v(-53.1, -38.3) * mm, "mid": v(-53.35, -38.63) * mm, "end": v(-53.26, -39.04) * mm});
            skArc(sketch, "E62.37.17.0", {"start": v(-53.52, -34) * mm, "mid": v(-53.61, -34.03) * mm, "end": v(-53.7, -34.08) * mm});
            skArc(sketch, "E62.41.17.0", {"start": v(-50.66, -33.97) * mm, "mid": v(-50.86, -33.79) * mm, "end": v(-51.12, -33.73) * mm});
            skArc(sketch, "E62.45.17.0", {"start": v(-51.68, -37.52) * mm, "mid": v(-51.6, -37.47) * mm, "end": v(-51.54, -37.4) * mm});
            skArc(sketch, "E62.1.18.0", {"start": v(-46.44, -43.57) * mm, "mid": v(-45.82, -42.51) * mm, "end": v(-45.28, -41.42) * mm});
            skLineSegment(sketch, "E62.5.18.0", {"start": v(-49, -40.54) * mm, "end": v(-50.5, -41.77) * mm});
            skArc(sketch, "E62.8.18.0", {"start": v(-48.84, -40.45) * mm, "mid": v(-47.67, -40.11) * mm, "end": v(-46.49, -39.87) * mm});
            skPoint(sketch, "E62.9.18.0", {"position": v(-48.34, -45) * mm});
            skLineSegment(sketch, "E62.12.18.0", {"start": v(-46.57, -43.7) * mm, "end": v(-47.88, -44.65) * mm});
            skPoint(sketch, "E62.15.18.0", {"position": v(-45.17, -41.14) * mm});
            skPoint(sketch, "E62.16.18.0", {"position": v(-48.93, -40.48) * mm});
            skPoint(sketch, "E62.17.18.0", {"position": v(-46.19, -39.82) * mm});
            skPoint(sketch, "E62.18.18.0", {"position": v(-50.88, -42.1) * mm});
            skLineSegment(sketch, "E62.19.18.0", {"start": v(-46, -40.05) * mm, "end": v(-45.67, -40.47) * mm});
            skLineSegment(sketch, "E62.22.18.0", {"start": v(-45.34, -40.9) * mm, "end": v(-45.67, -40.47) * mm});
            skArc(sketch, "E62.25.18.0", {"start": v(-45.28, -41.42) * mm, "mid": v(-45.24, -41.15) * mm, "end": v(-45.34, -40.9) * mm});
            skArc(sketch, "E62.29.18.0", {"start": v(-51.2, -41.7) * mm, "mid": v(-50.87, -41.88) * mm, "end": v(-50.5, -41.77) * mm});
            skArc(sketch, "E62.33.18.0", {"start": v(-47.88, -44.65) * mm, "mid": v(-48.08, -45.02) * mm, "end": v(-47.95, -45.41) * mm});
            skArc(sketch, "E62.37.18.0", {"start": v(-48.84, -40.45) * mm, "mid": v(-48.92, -40.48) * mm, "end": v(-49, -40.54) * mm});
            skArc(sketch, "E62.41.18.0", {"start": v(-46, -40.05) * mm, "mid": v(-46.22, -39.9) * mm, "end": v(-46.49, -39.87) * mm});
            skArc(sketch, "E62.45.18.0", {"start": v(-46.57, -43.7) * mm, "mid": v(-46.5, -43.64) * mm, "end": v(-46.44, -43.57) * mm});
            skArc(sketch, "E62.1.19.0", {"start": v(-40.62, -49.04) * mm, "mid": v(-40.13, -47.92) * mm, "end": v(-39.74, -46.76) * mm});
            skLineSegment(sketch, "E62.5.19.0", {"start": v(-43.53, -46.36) * mm, "end": v(-44.86, -47.77) * mm});
            skArc(sketch, "E62.8.19.0", {"start": v(-43.38, -46.25) * mm, "mid": v(-42.27, -45.77) * mm, "end": v(-41.12, -45.38) * mm});
            skPoint(sketch, "E62.9.19.0", {"position": v(-42.32, -50.7) * mm});
            skLineSegment(sketch, "E62.12.19.0", {"start": v(-40.73, -49.2) * mm, "end": v(-41.9, -50.3) * mm});
            skPoint(sketch, "E62.15.19.0", {"position": v(-39.65, -46.48) * mm});
            skPoint(sketch, "E62.16.19.0", {"position": v(-43.47, -46.29) * mm});
            skPoint(sketch, "E62.17.19.0", {"position": v(-40.83, -45.3) * mm});
            skPoint(sketch, "E62.18.19.0", {"position": v(-45.2, -48.14) * mm});
            skLineSegment(sketch, "E62.19.19.0", {"start": v(-40.62, -45.5) * mm, "end": v(-40.24, -45.88) * mm});
            skLineSegment(sketch, "E62.22.19.0", {"start": v(-39.86, -46.26) * mm, "end": v(-40.24, -45.88) * mm});
            skArc(sketch, "E62.25.19.0", {"start": v(-39.74, -46.76) * mm, "mid": v(-39.73, -46.5) * mm, "end": v(-39.86, -46.26) * mm});
            skArc(sketch, "E62.29.19.0", {"start": v(-45.58, -47.79) * mm, "mid": v(-45.21, -47.93) * mm, "end": v(-44.86, -47.77) * mm});
            skArc(sketch, "E62.33.19.0", {"start": v(-41.9, -50.3) * mm, "mid": v(-42.06, -50.69) * mm, "end": v(-41.88, -51.06) * mm});
            skArc(sketch, "E62.37.19.0", {"start": v(-43.38, -46.25) * mm, "mid": v(-43.46, -46.3) * mm, "end": v(-43.53, -46.36) * mm});
            skArc(sketch, "E62.41.19.0", {"start": v(-40.62, -45.5) * mm, "mid": v(-40.86, -45.37) * mm, "end": v(-41.12, -45.38) * mm});
            skArc(sketch, "E62.45.19.0", {"start": v(-40.73, -49.2) * mm, "mid": v(-40.66, -49.12) * mm, "end": v(-40.62, -49.04) * mm});
            skArc(sketch, "E62.1.20.0", {"start": v(-34.15, -53.75) * mm, "mid": v(-33.81, -52.57) * mm, "end": v(-33.56, -51.38) * mm});
            skLineSegment(sketch, "E62.5.20.0", {"start": v(-37.38, -51.45) * mm, "end": v(-38.52, -53.01) * mm});
            skArc(sketch, "E62.8.20.0", {"start": v(-37.24, -51.32) * mm, "mid": v(-36.2, -50.7) * mm, "end": v(-35.11, -50.17) * mm});
            skPoint(sketch, "E62.9.20.0", {"position": v(-35.64, -55.6) * mm});
            skLineSegment(sketch, "E62.12.20.0", {"start": v(-34.24, -53.91) * mm, "end": v(-35.27, -55.16) * mm});
            skPoint(sketch, "E62.15.20.0", {"position": v(-33.52, -51.08) * mm});
            skPoint(sketch, "E62.16.20.0", {"position": v(-37.32, -51.37) * mm});
            skPoint(sketch, "E62.17.20.0", {"position": v(-34.84, -50.06) * mm});
            skPoint(sketch, "E62.18.20.0", {"position": v(-38.82, -53.43) * mm});
            skLineSegment(sketch, "E62.19.20.0", {"start": v(-34.6, -50.23) * mm, "end": v(-34.17, -50.56) * mm});
            skLineSegment(sketch, "E62.22.20.0", {"start": v(-33.75, -50.9) * mm, "end": v(-34.17, -50.56) * mm});
            skArc(sketch, "E62.25.20.0", {"start": v(-33.56, -51.38) * mm, "mid": v(-33.59, -51.11) * mm, "end": v(-33.75, -50.9) * mm});
            skArc(sketch, "E62.29.20.0", {"start": v(-39.23, -53.12) * mm, "mid": v(-38.85, -53.22) * mm, "end": v(-38.52, -53.01) * mm});
            skArc(sketch, "E62.33.20.0", {"start": v(-35.27, -55.16) * mm, "mid": v(-35.38, -55.56) * mm, "end": v(-35.15, -55.9) * mm});
            skArc(sketch, "E62.37.20.0", {"start": v(-37.24, -51.32) * mm, "mid": v(-37.32, -51.38) * mm, "end": v(-37.38, -51.45) * mm});
            skArc(sketch, "E62.41.20.0", {"start": v(-34.6, -50.23) * mm, "mid": v(-34.85, -50.13) * mm, "end": v(-35.11, -50.17) * mm});
            skArc(sketch, "E62.45.20.0", {"start": v(-34.24, -53.91) * mm, "mid": v(-34.19, -53.83) * mm, "end": v(-34.15, -53.75) * mm});
            skArc(sketch, "E62.1.21.0", {"start": v(-27.14, -57.6) * mm, "mid": v(-26.95, -56.4) * mm, "end": v(-26.86, -55.18) * mm});
            skLineSegment(sketch, "E62.5.21.0", {"start": v(-30.64, -55.73) * mm, "end": v(-31.57, -57.42) * mm});
            skArc(sketch, "E62.8.21.0", {"start": v(-30.52, -55.58) * mm, "mid": v(-29.56, -54.84) * mm, "end": v(-28.55, -54.18) * mm});
            skPoint(sketch, "E62.9.21.0", {"position": v(-28.39, -59.63) * mm});
            skLineSegment(sketch, "E62.12.21.0", {"start": v(-27.21, -57.78) * mm, "end": v(-28.08, -59.14) * mm});
            skPoint(sketch, "E62.15.21.0", {"position": v(-26.85, -54.88) * mm});
            skPoint(sketch, "E62.16.21.0", {"position": v(-30.6, -55.65) * mm});
            skPoint(sketch, "E62.17.21.0", {"position": v(-28.29, -54.03) * mm});
            skPoint(sketch, "E62.18.21.0", {"position": v(-31.82, -57.87) * mm});
            skLineSegment(sketch, "E62.19.21.0", {"start": v(-28.03, -54.17) * mm, "end": v(-27.56, -54.44) * mm});
            skLineSegment(sketch, "E62.22.21.0", {"start": v(-27.1, -54.72) * mm, "end": v(-27.56, -54.44) * mm});
            skArc(sketch, "E62.25.21.0", {"start": v(-26.86, -55.18) * mm, "mid": v(-26.92, -54.92) * mm, "end": v(-27.1, -54.72) * mm});
            skArc(sketch, "E62.29.21.0", {"start": v(-32.26, -57.62) * mm, "mid": v(-31.87, -57.67) * mm, "end": v(-31.57, -57.42) * mm});
            skArc(sketch, "E62.33.21.0", {"start": v(-28.08, -59.14) * mm, "mid": v(-28.14, -59.56) * mm, "end": v(-27.86, -59.87) * mm});
            skArc(sketch, "E62.37.21.0", {"start": v(-30.52, -55.58) * mm, "mid": v(-30.58, -55.65) * mm, "end": v(-30.64, -55.73) * mm});
            skArc(sketch, "E62.41.21.0", {"start": v(-28.03, -54.17) * mm, "mid": v(-28.29, -54.1) * mm, "end": v(-28.55, -54.18) * mm});
            skArc(sketch, "E62.45.21.0", {"start": v(-27.21, -57.78) * mm, "mid": v(-27.17, -57.7) * mm, "end": v(-27.14, -57.6) * mm});
            skArc(sketch, "E62.1.22.0", {"start": v(-19.7, -60.55) * mm, "mid": v(-19.67, -59.33) * mm, "end": v(-19.73, -58.1) * mm});
            skLineSegment(sketch, "E62.5.22.0", {"start": v(-23.41, -59.13) * mm, "end": v(-24.12, -60.93) * mm});
            skArc(sketch, "E62.8.22.0", {"start": v(-23.31, -58.97) * mm, "mid": v(-22.45, -58.12) * mm, "end": v(-21.53, -57.33) * mm});
            skPoint(sketch, "E62.9.22.0", {"position": v(-20.69, -62.72) * mm});
            skLineSegment(sketch, "E62.12.22.0", {"start": v(-19.76, -60.73) * mm, "end": v(-20.44, -62.2) * mm});
            skPoint(sketch, "E62.15.22.0", {"position": v(-19.76, -57.8) * mm});
            skPoint(sketch, "E62.16.22.0", {"position": v(-23.38, -59.04) * mm});
            skPoint(sketch, "E62.17.22.0", {"position": v(-21.3, -57.15) * mm});
            skPoint(sketch, "E62.18.22.0", {"position": v(-24.31, -61.4) * mm});
            skLineSegment(sketch, "E62.19.22.0", {"start": v(-21.02, -57.26) * mm, "end": v(-20.52, -57.47) * mm});
            skLineSegment(sketch, "E62.22.22.0", {"start": v(-20.03, -57.69) * mm, "end": v(-20.52, -57.47) * mm});
            skArc(sketch, "E62.25.22.0", {"start": v(-19.73, -58.1) * mm, "mid": v(-19.82, -57.86) * mm, "end": v(-20.03, -57.69) * mm});
            skArc(sketch, "E62.29.22.0", {"start": v(-24.79, -61.21) * mm, "mid": v(-24.4, -61.2) * mm, "end": v(-24.12, -60.93) * mm});
            skArc(sketch, "E62.33.22.0", {"start": v(-20.44, -62.2) * mm, "mid": v(-20.45, -62.61) * mm, "end": v(-20.14, -62.9) * mm});
            skArc(sketch, "E62.37.22.0", {"start": v(-23.31, -58.97) * mm, "mid": v(-23.37, -59.04) * mm, "end": v(-23.41, -59.13) * mm});
            skArc(sketch, "E62.41.22.0", {"start": v(-21.02, -57.26) * mm, "mid": v(-21.28, -57.23) * mm, "end": v(-21.53, -57.33) * mm});
            skArc(sketch, "E62.45.22.0", {"start": v(-19.76, -60.73) * mm, "mid": v(-19.72, -60.64) * mm, "end": v(-19.7, -60.55) * mm});
            skArc(sketch, "E62.1.23.0", {"start": v(-11.97, -62.54) * mm, "mid": v(-12.08, -61.33) * mm, "end": v(-12.3, -60.12) * mm});
            skLineSegment(sketch, "E62.5.23.0", {"start": v(-15.82, -61.6) * mm, "end": v(-16.3, -63.47) * mm});
            skArc(sketch, "E62.8.23.0", {"start": v(-15.74, -61.43) * mm, "mid": v(-15, -60.47) * mm, "end": v(-14.17, -59.58) * mm});
            skPoint(sketch, "E62.9.23.0", {"position": v(-12.67, -64.81) * mm});
            skLineSegment(sketch, "E62.12.23.0", {"start": v(-11.99, -62.73) * mm, "end": v(-12.49, -64.27) * mm});
            skPoint(sketch, "E62.15.23.0", {"position": v(-12.36, -59.83) * mm});
            skPoint(sketch, "E62.16.23.0", {"position": v(-15.8, -61.5) * mm});
            skPoint(sketch, "E62.17.23.0", {"position": v(-13.96, -59.36) * mm});
            skPoint(sketch, "E62.18.23.0", {"position": v(-16.42, -63.97) * mm});
            skLineSegment(sketch, "E62.19.23.0", {"start": v(-13.68, -59.44) * mm, "end": v(-13.16, -59.59) * mm});
            skLineSegment(sketch, "E62.22.23.0", {"start": v(-12.64, -59.74) * mm, "end": v(-13.16, -59.59) * mm});
            skArc(sketch, "E62.25.23.0", {"start": v(-12.3, -60.12) * mm, "mid": v(-12.42, -59.89) * mm, "end": v(-12.64, -59.74) * mm});
            skArc(sketch, "E62.29.23.0", {"start": v(-16.92, -63.84) * mm, "mid": v(-16.53, -63.78) * mm, "end": v(-16.3, -63.47) * mm});
            skArc(sketch, "E62.33.23.0", {"start": v(-12.49, -64.27) * mm, "mid": v(-12.44, -64.68) * mm, "end": v(-12.1, -64.92) * mm});
            skArc(sketch, "E62.37.23.0", {"start": v(-15.74, -61.43) * mm, "mid": v(-15.78, -61.5) * mm, "end": v(-15.82, -61.6) * mm});
            skArc(sketch, "E62.41.23.0", {"start": v(-13.68, -59.44) * mm, "mid": v(-13.94, -59.44) * mm, "end": v(-14.17, -59.58) * mm});
            skArc(sketch, "E62.45.23.0", {"start": v(-11.99, -62.73) * mm, "mid": v(-11.97, -62.64) * mm, "end": v(-11.97, -62.54) * mm});
            skArc(sketch, "E62.1.24.0", {"start": v(-4.03, -63.55) * mm, "mid": v(-4.3, -62.36) * mm, "end": v(-4.66, -61.2) * mm});
            skLineSegment(sketch, "E62.5.24.0", {"start": v(-7.97, -63.1) * mm, "end": v(-8.21, -65.01) * mm});
            skArc(sketch, "E62.8.24.0", {"start": v(-7.91, -62.91) * mm, "mid": v(-7.3, -61.87) * mm, "end": v(-6.6, -60.88) * mm});
            skPoint(sketch, "E62.9.24.0", {"position": v(-4.44, -65.9) * mm});
            skLineSegment(sketch, "E62.12.24.0", {"start": v(-4.03, -63.74) * mm, "end": v(-4.33, -65.32) * mm});
            skPoint(sketch, "E62.15.24.0", {"position": v(-4.76, -60.9) * mm});
            skPoint(sketch, "E62.16.24.0", {"position": v(-7.96, -63) * mm});
            skPoint(sketch, "E62.17.24.0", {"position": v(-6.41, -60.65) * mm});
            skPoint(sketch, "E62.18.24.0", {"position": v(-8.28, -65.52) * mm});
            skLineSegment(sketch, "E62.19.24.0", {"start": v(-6.12, -60.69) * mm, "end": v(-5.59, -60.77) * mm});
            skLineSegment(sketch, "E62.22.24.0", {"start": v(-5.05, -60.86) * mm, "end": v(-5.59, -60.77) * mm});
            skArc(sketch, "E62.25.24.0", {"start": v(-4.66, -61.2) * mm, "mid": v(-4.81, -60.97) * mm, "end": v(-5.05, -60.86) * mm});
            skArc(sketch, "E62.29.24.0", {"start": v(-8.78, -65.45) * mm, "mid": v(-8.4, -65.35) * mm, "end": v(-8.21, -65.01) * mm});
            skArc(sketch, "E62.33.24.0", {"start": v(-4.33, -65.32) * mm, "mid": v(-4.24, -65.73) * mm, "end": v(-3.87, -65.93) * mm});
            skArc(sketch, "E62.37.24.0", {"start": v(-7.91, -62.91) * mm, "mid": v(-7.95, -63) * mm, "end": v(-7.97, -63.1) * mm});
            skArc(sketch, "E62.41.24.0", {"start": v(-6.12, -60.69) * mm, "mid": v(-6.38, -60.72) * mm, "end": v(-6.6, -60.88) * mm});
            skArc(sketch, "E62.45.24.0", {"start": v(-4.03, -63.74) * mm, "mid": v(-4.02, -63.64) * mm, "end": v(-4.03, -63.55) * mm});
            skArc(sketch, "E62.1.25.0", {"start": v(3.96, -63.55) * mm, "mid": v(3.55, -62.4) * mm, "end": v(3.05, -61.3) * mm});
            skLineSegment(sketch, "E62.5.25.0", {"start": v(0, -63.6) * mm, "end": v(0, -65.53) * mm});
            skArc(sketch, "E62.8.25.0", {"start": v(0.03, -63.4) * mm, "mid": v(0.52, -62.3) * mm, "end": v(1.09, -61.23) * mm});
            skPoint(sketch, "E62.9.25.0", {"position": v(3.85, -65.93) * mm});
            skLineSegment(sketch, "E62.12.25.0", {"start": v(3.99, -63.74) * mm, "end": v(3.89, -65.35) * mm});
            skPoint(sketch, "E62.15.25.0", {"position": v(2.9, -61.02) * mm});
            skPoint(sketch, "E62.16.25.0", {"position": v(0, -63.5) * mm});
            skPoint(sketch, "E62.17.25.0", {"position": v(1.24, -60.97) * mm});
            skPoint(sketch, "E62.18.25.0", {"position": v(0, -66.04) * mm});
            skLineSegment(sketch, "E62.19.25.0", {"start": v(1.54, -60.98) * mm, "end": v(2.07, -60.99) * mm});
            skLineSegment(sketch, "E62.22.25.0", {"start": v(2.61, -61.01) * mm, "end": v(2.07, -60.99) * mm});
            skArc(sketch, "E62.25.25.0", {"start": v(3.05, -61.3) * mm, "mid": v(2.87, -61.1) * mm, "end": v(2.61, -61.01) * mm});
            skArc(sketch, "E62.29.25.0", {"start": v(-0.51, -66.04) * mm, "mid": v(-0.15, -65.9) * mm, "end": v(0, -65.53) * mm});
            skArc(sketch, "E62.33.25.0", {"start": v(3.89, -65.35) * mm, "mid": v(4.04, -65.74) * mm, "end": v(4.43, -65.9) * mm});
            skArc(sketch, "E62.37.25.0", {"start": v(0.03, -63.4) * mm, "mid": v(0, -63.5) * mm, "end": v(0, -63.6) * mm});
            skArc(sketch, "E62.41.25.0", {"start": v(1.54, -60.98) * mm, "mid": v(1.28, -61.04) * mm, "end": v(1.09, -61.23) * mm});
            skArc(sketch, "E62.45.25.0", {"start": v(3.99, -63.74) * mm, "mid": v(3.99, -63.65) * mm, "end": v(3.96, -63.55) * mm});
            skArc(sketch, "E62.1.26.0", {"start": v(11.9, -62.56) * mm, "mid": v(11.34, -61.47) * mm, "end": v(10.7, -60.43) * mm});
            skLineSegment(sketch, "E62.5.26.0", {"start": v(7.97, -63.1) * mm, "end": v(8.21, -65.01) * mm});
            skArc(sketch, "E62.8.26.0", {"start": v(7.98, -62.9) * mm, "mid": v(8.32, -61.74) * mm, "end": v(8.75, -60.61) * mm});
            skPoint(sketch, "E62.9.26.0", {"position": v(12.08, -64.93) * mm});
            skLineSegment(sketch, "E62.12.26.0", {"start": v(11.95, -62.74) * mm, "end": v(12.05, -64.35) * mm});
            skPoint(sketch, "E62.15.26.0", {"position": v(10.53, -60.18) * mm});
            skPoint(sketch, "E62.16.26.0", {"position": v(7.96, -63) * mm});
            skPoint(sketch, "E62.17.26.0", {"position": v(8.87, -60.34) * mm});
            skPoint(sketch, "E62.18.26.0", {"position": v(8.28, -65.52) * mm});
            skLineSegment(sketch, "E62.19.26.0", {"start": v(9.17, -60.3) * mm, "end": v(9.7, -60.25) * mm});
            skLineSegment(sketch, "E62.22.26.0", {"start": v(10.24, -60.2) * mm, "end": v(9.7, -60.25) * mm});
            skArc(sketch, "E62.25.26.0", {"start": v(10.7, -60.43) * mm, "mid": v(10.5, -60.25) * mm, "end": v(10.24, -60.2) * mm});
            skArc(sketch, "E62.29.26.0", {"start": v(7.77, -65.58) * mm, "mid": v(8.1, -65.39) * mm, "end": v(8.21, -65.01) * mm});
            skArc(sketch, "E62.33.26.0", {"start": v(12.05, -64.35) * mm, "mid": v(12.24, -64.72) * mm, "end": v(12.65, -64.82) * mm});
            skArc(sketch, "E62.37.26.0", {"start": v(7.98, -62.9) * mm, "mid": v(7.97, -63) * mm, "end": v(7.97, -63.1) * mm});
            skArc(sketch, "E62.41.26.0", {"start": v(9.17, -60.3) * mm, "mid": v(8.92, -60.4) * mm, "end": v(8.75, -60.61) * mm});
            skArc(sketch, "E62.45.26.0", {"start": v(11.95, -62.74) * mm, "mid": v(11.93, -62.65) * mm, "end": v(11.9, -62.56) * mm});
            skArc(sketch, "E62.1.27.0", {"start": v(19.65, -60.57) * mm, "mid": v(18.96, -59.56) * mm, "end": v(18.2, -58.6) * mm});
            skLineSegment(sketch, "E62.5.27.0", {"start": v(15.82, -61.6) * mm, "end": v(16.3, -63.47) * mm});
            skArc(sketch, "E62.8.27.0", {"start": v(15.8, -61.4) * mm, "mid": v(16, -60.21) * mm, "end": v(16.28, -59.04) * mm});
            skPoint(sketch, "E62.9.27.0", {"position": v(20.12, -62.9) * mm});
            skLineSegment(sketch, "E62.12.27.0", {"start": v(19.71, -60.75) * mm, "end": v(20.02, -62.33) * mm});
            skPoint(sketch, "E62.15.27.0", {"position": v(18, -58.38) * mm});
            skPoint(sketch, "E62.16.27.0", {"position": v(15.8, -61.5) * mm});
            skPoint(sketch, "E62.17.27.0", {"position": v(16.36, -58.75) * mm});
            skPoint(sketch, "E62.18.27.0", {"position": v(16.42, -63.97) * mm});
            skLineSegment(sketch, "E62.19.27.0", {"start": v(16.65, -58.68) * mm, "end": v(17.18, -58.56) * mm});
            skLineSegment(sketch, "E62.22.27.0", {"start": v(17.7, -58.44) * mm, "end": v(17.18, -58.56) * mm});
            skArc(sketch, "E62.25.27.0", {"start": v(18.2, -58.6) * mm, "mid": v(17.97, -58.46) * mm, "end": v(17.7, -58.44) * mm});
            skArc(sketch, "E62.29.27.0", {"start": v(15.93, -64.1) * mm, "mid": v(16.24, -63.86) * mm, "end": v(16.3, -63.47) * mm});
            skArc(sketch, "E62.33.27.0", {"start": v(20.02, -62.33) * mm, "mid": v(20.26, -62.68) * mm, "end": v(20.68, -62.72) * mm});
            skArc(sketch, "E62.37.27.0", {"start": v(15.8, -61.4) * mm, "mid": v(15.8, -61.5) * mm, "end": v(15.82, -61.6) * mm});
            skArc(sketch, "E62.41.27.0", {"start": v(16.65, -58.68) * mm, "mid": v(16.42, -58.8) * mm, "end": v(16.28, -59.04) * mm});
            skArc(sketch, "E62.45.27.0", {"start": v(19.71, -60.75) * mm, "mid": v(19.69, -60.66) * mm, "end": v(19.65, -60.57) * mm});
            skArc(sketch, "E62.1.28.0", {"start": v(27.08, -57.63) * mm, "mid": v(26.27, -56.72) * mm, "end": v(25.4, -55.87) * mm});
            skLineSegment(sketch, "E62.5.28.0", {"start": v(23.41, -59.13) * mm, "end": v(24.12, -60.93) * mm});
            skArc(sketch, "E62.8.28.0", {"start": v(23.38, -58.94) * mm, "mid": v(23.42, -57.73) * mm, "end": v(23.55, -56.53) * mm});
            skPoint(sketch, "E62.9.28.0", {"position": v(27.85, -59.88) * mm});
            skLineSegment(sketch, "E62.12.28.0", {"start": v(27.17, -57.8) * mm, "end": v(27.67, -59.33) * mm});
            skPoint(sketch, "E62.15.28.0", {"position": v(25.17, -55.67) * mm});
            skPoint(sketch, "E62.16.28.0", {"position": v(23.38, -59.04) * mm});
            skPoint(sketch, "E62.17.28.0", {"position": v(23.6, -56.23) * mm});
            skPoint(sketch, "E62.18.28.0", {"position": v(24.31, -61.4) * mm});
            skLineSegment(sketch, "E62.19.28.0", {"start": v(23.87, -56.13) * mm, "end": v(24.38, -55.94) * mm});
            skLineSegment(sketch, "E62.22.28.0", {"start": v(24.89, -55.76) * mm, "end": v(24.38, -55.94) * mm});
            skArc(sketch, "E62.25.28.0", {"start": v(25.4, -55.87) * mm, "mid": v(25.16, -55.75) * mm, "end": v(24.89, -55.76) * mm});
            skArc(sketch, "E62.29.28.0", {"start": v(23.83, -61.59) * mm, "mid": v(24.12, -61.32) * mm, "end": v(24.12, -60.93) * mm});
            skArc(sketch, "E62.33.28.0", {"start": v(27.67, -59.33) * mm, "mid": v(27.95, -59.64) * mm, "end": v(28.37, -59.63) * mm});
            skArc(sketch, "E62.37.28.0", {"start": v(23.38, -58.94) * mm, "mid": v(23.38, -59.04) * mm, "end": v(23.41, -59.13) * mm});
            skArc(sketch, "E62.41.28.0", {"start": v(23.87, -56.13) * mm, "mid": v(23.66, -56.29) * mm, "end": v(23.55, -56.53) * mm});
            skArc(sketch, "E62.45.28.0", {"start": v(27.17, -57.8) * mm, "mid": v(27.14, -57.71) * mm, "end": v(27.08, -57.63) * mm});
            skArc(sketch, "E62.1.29.0", {"start": v(34.1, -53.78) * mm, "mid": v(33.17, -52.98) * mm, "end": v(32.2, -52.24) * mm});
            skLineSegment(sketch, "E62.5.29.0", {"start": v(30.64, -55.73) * mm, "end": v(31.57, -57.42) * mm});
            skArc(sketch, "E62.8.29.0", {"start": v(30.58, -55.55) * mm, "mid": v(30.47, -54.34) * mm, "end": v(30.45, -53.13) * mm});
            skPoint(sketch, "E62.9.29.0", {"position": v(35.14, -55.92) * mm});
            skLineSegment(sketch, "E62.12.29.0", {"start": v(34.2, -53.94) * mm, "end": v(34.89, -55.4) * mm});
            skPoint(sketch, "E62.15.29.0", {"position": v(31.95, -52.07) * mm});
            skPoint(sketch, "E62.16.29.0", {"position": v(30.6, -55.65) * mm});
            skPoint(sketch, "E62.17.29.0", {"position": v(30.46, -52.83) * mm});
            skPoint(sketch, "E62.18.29.0", {"position": v(31.82, -57.87) * mm});
            skLineSegment(sketch, "E62.19.29.0", {"start": v(30.72, -52.7) * mm, "end": v(31.2, -52.44) * mm});
            skLineSegment(sketch, "E62.22.29.0", {"start": v(31.68, -52.2) * mm, "end": v(31.2, -52.44) * mm});
            skArc(sketch, "E62.25.29.0", {"start": v(32.2, -52.24) * mm, "mid": v(31.94, -52.15) * mm, "end": v(31.68, -52.2) * mm});
            skArc(sketch, "E62.29.29.0", {"start": v(31.37, -58.12) * mm, "mid": v(31.61, -57.81) * mm, "end": v(31.57, -57.42) * mm});
            skArc(sketch, "E62.33.29.0", {"start": v(34.89, -55.4) * mm, "mid": v(35.2, -55.67) * mm, "end": v(35.62, -55.6) * mm});
            skArc(sketch, "E62.37.29.0", {"start": v(30.58, -55.55) * mm, "mid": v(30.6, -55.64) * mm, "end": v(30.64, -55.73) * mm});
            skArc(sketch, "E62.41.29.0", {"start": v(30.72, -52.7) * mm, "mid": v(30.53, -52.88) * mm, "end": v(30.45, -53.13) * mm});
            skArc(sketch, "E62.45.29.0", {"start": v(34.2, -53.94) * mm, "mid": v(34.15, -53.85) * mm, "end": v(34.1, -53.78) * mm});
            skArc(sketch, "E62.1.30.0", {"start": v(40.56, -49.09) * mm, "mid": v(39.55, -48.4) * mm, "end": v(38.49, -47.8) * mm});
            skLineSegment(sketch, "E62.5.30.0", {"start": v(37.38, -51.45) * mm, "end": v(38.52, -53.01) * mm});
            skArc(sketch, "E62.8.30.0", {"start": v(37.3, -51.28) * mm, "mid": v(37.04, -50.1) * mm, "end": v(36.87, -48.9) * mm});
            skPoint(sketch, "E62.9.30.0", {"position": v(41.87, -51.07) * mm});
            skLineSegment(sketch, "E62.12.30.0", {"start": v(40.7, -49.22) * mm, "end": v(41.56, -50.59) * mm});
            skPoint(sketch, "E62.15.30.0", {"position": v(38.22, -47.66) * mm});
            skPoint(sketch, "E62.16.30.0", {"position": v(37.32, -51.37) * mm});
            skPoint(sketch, "E62.17.30.0", {"position": v(36.84, -48.6) * mm});
            skPoint(sketch, "E62.18.30.0", {"position": v(38.82, -53.43) * mm});
            skLineSegment(sketch, "E62.19.30.0", {"start": v(37.08, -48.43) * mm, "end": v(37.53, -48.12) * mm});
            skLineSegment(sketch, "E62.22.30.0", {"start": v(37.98, -47.82) * mm, "end": v(37.53, -48.12) * mm});
            skArc(sketch, "E62.25.30.0", {"start": v(38.49, -47.8) * mm, "mid": v(38.23, -47.74) * mm, "end": v(37.98, -47.82) * mm});
            skArc(sketch, "E62.29.30.0", {"start": v(38.4, -53.73) * mm, "mid": v(38.6, -53.4) * mm, "end": v(38.52, -53.01) * mm});
            skArc(sketch, "E62.33.30.0", {"start": v(41.56, -50.59) * mm, "mid": v(41.9, -50.82) * mm, "end": v(42.31, -50.7) * mm});
            skArc(sketch, "E62.37.30.0", {"start": v(37.3, -51.28) * mm, "mid": v(37.33, -51.37) * mm, "end": v(37.38, -51.45) * mm});
            skArc(sketch, "E62.41.30.0", {"start": v(37.08, -48.43) * mm, "mid": v(36.91, -48.63) * mm, "end": v(36.87, -48.9) * mm});
            skArc(sketch, "E62.45.30.0", {"start": v(40.7, -49.22) * mm, "mid": v(40.63, -49.15) * mm, "end": v(40.56, -49.09) * mm});
            skArc(sketch, "E62.1.31.0", {"start": v(46.4, -43.62) * mm, "mid": v(45.3, -43.06) * mm, "end": v(44.18, -42.6) * mm});
            skLineSegment(sketch, "E62.5.31.0", {"start": v(43.53, -46.36) * mm, "end": v(44.86, -47.77) * mm});
            skArc(sketch, "E62.8.31.0", {"start": v(43.43, -46.2) * mm, "mid": v(43.03, -45.06) * mm, "end": v(42.7, -43.9) * mm});
            skPoint(sketch, "E62.9.31.0", {"position": v(47.94, -45.42) * mm});
            skLineSegment(sketch, "E62.12.31.0", {"start": v(46.54, -43.74) * mm, "end": v(47.57, -44.98) * mm});
            skPoint(sketch, "E62.15.31.0", {"position": v(43.9, -42.5) * mm});
            skPoint(sketch, "E62.16.31.0", {"position": v(43.47, -46.29) * mm});
            skPoint(sketch, "E62.17.31.0", {"position": v(42.64, -43.6) * mm});
            skPoint(sketch, "E62.18.31.0", {"position": v(45.2, -48.14) * mm});
            skLineSegment(sketch, "E62.19.31.0", {"start": v(42.86, -43.4) * mm, "end": v(43.26, -43.04) * mm});
            skLineSegment(sketch, "E62.22.31.0", {"start": v(43.67, -42.69) * mm, "end": v(43.26, -43.04) * mm});
            skArc(sketch, "E62.25.31.0", {"start": v(44.18, -42.6) * mm, "mid": v(43.91, -42.57) * mm, "end": v(43.67, -42.69) * mm});
            skArc(sketch, "E62.29.31.0", {"start": v(44.83, -48.5) * mm, "mid": v(45, -48.14) * mm, "end": v(44.86, -47.77) * mm});
            skArc(sketch, "E62.33.31.0", {"start": v(47.57, -44.98) * mm, "mid": v(47.95, -45.16) * mm, "end": v(48.33, -45) * mm});
            skArc(sketch, "E62.37.31.0", {"start": v(43.43, -46.2) * mm, "mid": v(43.48, -46.28) * mm, "end": v(43.53, -46.36) * mm});
            skArc(sketch, "E62.41.31.0", {"start": v(42.86, -43.4) * mm, "mid": v(42.72, -43.62) * mm, "end": v(42.7, -43.9) * mm});
            skArc(sketch, "E62.45.31.0", {"start": v(46.54, -43.74) * mm, "mid": v(46.47, -43.67) * mm, "end": v(46.4, -43.62) * mm});
            skArc(sketch, "E62.1.32.0", {"start": v(51.5, -37.46) * mm, "mid": v(50.35, -37.04) * mm, "end": v(49.17, -36.72) * mm});
            skLineSegment(sketch, "E62.5.32.0", {"start": v(49, -40.54) * mm, "end": v(50.5, -41.77) * mm});
            skArc(sketch, "E62.8.32.0", {"start": v(48.88, -40.4) * mm, "mid": v(48.33, -39.31) * mm, "end": v(47.87, -38.2) * mm});
            skPoint(sketch, "E62.9.32.0", {"position": v(53.25, -39.06) * mm});
            skLineSegment(sketch, "E62.12.32.0", {"start": v(51.66, -37.56) * mm, "end": v(52.83, -38.66) * mm});
            skPoint(sketch, "E62.15.32.0", {"position": v(48.87, -36.66) * mm});
            skPoint(sketch, "E62.16.32.0", {"position": v(48.93, -40.48) * mm});
            skPoint(sketch, "E62.17.32.0", {"position": v(47.77, -37.9) * mm});
            skPoint(sketch, "E62.18.32.0", {"position": v(50.88, -42.1) * mm});
            skLineSegment(sketch, "E62.19.32.0", {"start": v(47.96, -37.69) * mm, "end": v(48.31, -37.28) * mm});
            skLineSegment(sketch, "E62.22.32.0", {"start": v(48.68, -36.88) * mm, "end": v(48.31, -37.28) * mm});
            skArc(sketch, "E62.25.32.0", {"start": v(49.17, -36.72) * mm, "mid": v(48.9, -36.73) * mm, "end": v(48.68, -36.88) * mm});
            skArc(sketch, "E62.29.32.0", {"start": v(50.56, -42.49) * mm, "mid": v(50.67, -42.12) * mm, "end": v(50.5, -41.77) * mm});
            skArc(sketch, "E62.33.32.0", {"start": v(52.83, -38.66) * mm, "mid": v(53.23, -38.8) * mm, "end": v(53.6, -38.59) * mm});
            skArc(sketch, "E62.37.32.0", {"start": v(48.88, -40.4) * mm, "mid": v(48.93, -40.47) * mm, "end": v(49, -40.54) * mm});
            skArc(sketch, "E62.41.32.0", {"start": v(47.96, -37.69) * mm, "mid": v(47.85, -37.93) * mm, "end": v(47.87, -38.2) * mm});
            skArc(sketch, "E62.45.32.0", {"start": v(51.66, -37.56) * mm, "mid": v(51.58, -37.5) * mm, "end": v(51.5, -37.46) * mm});
            skArc(sketch, "E62.1.33.0", {"start": v(55.79, -30.7) * mm, "mid": v(54.6, -30.44) * mm, "end": v(53.38, -30.27) * mm});
            skLineSegment(sketch, "E62.5.33.0", {"start": v(53.7, -34.08) * mm, "end": v(55.33, -35.11) * mm});
            skArc(sketch, "E62.8.33.0", {"start": v(53.56, -33.95) * mm, "mid": v(52.88, -32.94) * mm, "end": v(52.28, -31.9) * mm});
            skPoint(sketch, "E62.9.33.0", {"position": v(57.73, -32.07) * mm});
            skLineSegment(sketch, "E62.12.33.0", {"start": v(55.96, -30.79) * mm, "end": v(57.26, -31.74) * mm});
            skPoint(sketch, "E62.15.33.0", {"position": v(53.08, -30.24) * mm});
            skPoint(sketch, "E62.16.33.0", {"position": v(53.61, -34.03) * mm});
            skPoint(sketch, "E62.17.33.0", {"position": v(52.14, -31.62) * mm});
            skPoint(sketch, "E62.18.33.0", {"position": v(55.76, -35.39) * mm});
            skLineSegment(sketch, "E62.19.33.0", {"start": v(52.3, -31.38) * mm, "end": v(52.6, -30.93) * mm});
            skLineSegment(sketch, "E62.22.33.0", {"start": v(52.91, -30.49) * mm, "end": v(52.6, -30.93) * mm});
            skArc(sketch, "E62.25.33.0", {"start": v(53.38, -30.27) * mm, "mid": v(53.12, -30.31) * mm, "end": v(52.91, -30.49) * mm});
            skArc(sketch, "E62.29.33.0", {"start": v(55.48, -35.82) * mm, "mid": v(55.55, -35.43) * mm, "end": v(55.33, -35.11) * mm});
            skArc(sketch, "E62.33.33.0", {"start": v(57.26, -31.74) * mm, "mid": v(57.67, -31.82) * mm, "end": v(58, -31.57) * mm});
            skArc(sketch, "E62.37.33.0", {"start": v(53.56, -33.95) * mm, "mid": v(53.62, -34.02) * mm, "end": v(53.7, -34.08) * mm});
            skArc(sketch, "E62.41.33.0", {"start": v(52.3, -31.38) * mm, "mid": v(52.22, -31.63) * mm, "end": v(52.28, -31.9) * mm});
            skArc(sketch, "E62.45.33.0", {"start": v(55.96, -30.79) * mm, "mid": v(55.87, -30.74) * mm, "end": v(55.79, -30.7) * mm});
            skArc(sketch, "E62.1.34.0", {"start": v(59.2, -23.47) * mm, "mid": v(57.98, -23.36) * mm, "end": v(56.75, -23.34) * mm});
            skLineSegment(sketch, "E62.5.34.0", {"start": v(57.54, -27.08) * mm, "end": v(59.3, -27.9) * mm});
            skArc(sketch, "E62.8.34.0", {"start": v(57.39, -26.97) * mm, "mid": v(56.6, -26.06) * mm, "end": v(55.87, -25.09) * mm});
            skPoint(sketch, "E62.9.34.0", {"position": v(61.3, -24.59) * mm});
            skLineSegment(sketch, "E62.12.34.0", {"start": v(59.37, -23.53) * mm, "end": v(60.79, -24.3) * mm});
            skPoint(sketch, "E62.15.34.0", {"position": v(56.45, -23.35) * mm});
            skPoint(sketch, "E62.16.34.0", {"position": v(57.46, -27.04) * mm});
            skPoint(sketch, "E62.17.34.0", {"position": v(55.7, -24.84) * mm});
            skPoint(sketch, "E62.18.34.0", {"position": v(59.75, -28.12) * mm});
            skLineSegment(sketch, "E62.19.34.0", {"start": v(55.83, -24.57) * mm, "end": v(56.07, -24.1) * mm});
            skLineSegment(sketch, "E62.22.34.0", {"start": v(56.32, -23.61) * mm, "end": v(56.07, -24.1) * mm});
            skArc(sketch, "E62.25.34.0", {"start": v(56.75, -23.34) * mm, "mid": v(56.5, -23.42) * mm, "end": v(56.32, -23.61) * mm});
            skArc(sketch, "E62.29.34.0", {"start": v(59.54, -28.58) * mm, "mid": v(59.56, -28.2) * mm, "end": v(59.3, -27.9) * mm});
            skArc(sketch, "E62.33.34.0", {"start": v(60.79, -24.3) * mm, "mid": v(61.2, -24.34) * mm, "end": v(61.5, -24.05) * mm});
            skArc(sketch, "E62.37.34.0", {"start": v(57.39, -26.97) * mm, "mid": v(57.46, -27.03) * mm, "end": v(57.54, -27.08) * mm});
            skArc(sketch, "E62.41.34.0", {"start": v(55.83, -24.57) * mm, "mid": v(55.78, -24.84) * mm, "end": v(55.87, -25.09) * mm});
            skArc(sketch, "E62.45.34.0", {"start": v(59.37, -23.53) * mm, "mid": v(59.29, -23.5) * mm, "end": v(59.2, -23.47) * mm});
            skArc(sketch, "E62.1.35.0", {"start": v(61.67, -15.87) * mm, "mid": v(60.45, -15.9) * mm, "end": v(59.23, -16.04) * mm});
            skLineSegment(sketch, "E62.5.35.0", {"start": v(60.48, -19.65) * mm, "end": v(62.32, -20.25) * mm});
            skArc(sketch, "E62.8.35.0", {"start": v(60.32, -19.56) * mm, "mid": v(59.41, -18.76) * mm, "end": v(58.57, -17.89) * mm});
            skPoint(sketch, "E62.9.35.0", {"position": v(63.9, -16.71) * mm});
            skLineSegment(sketch, "E62.12.35.0", {"start": v(61.85, -15.9) * mm, "end": v(63.36, -16.5) * mm});
            skPoint(sketch, "E62.15.35.0", {"position": v(58.94, -16.1) * mm});
            skPoint(sketch, "E62.16.35.0", {"position": v(60.4, -19.62) * mm});
            skPoint(sketch, "E62.17.35.0", {"position": v(58.37, -17.66) * mm});
            skPoint(sketch, "E62.18.35.0", {"position": v(62.8, -20.4) * mm});
            skLineSegment(sketch, "E62.19.35.0", {"start": v(58.47, -17.38) * mm, "end": v(58.64, -16.87) * mm});
            skLineSegment(sketch, "E62.22.35.0", {"start": v(58.83, -16.37) * mm, "end": v(58.64, -16.87) * mm});
            skArc(sketch, "E62.25.35.0", {"start": v(59.23, -16.04) * mm, "mid": v(58.99, -16.15) * mm, "end": v(58.83, -16.37) * mm});
            skArc(sketch, "E62.29.35.0", {"start": v(62.65, -20.9) * mm, "mid": v(62.62, -20.5) * mm, "end": v(62.32, -20.25) * mm});
            skArc(sketch, "E62.33.35.0", {"start": v(63.36, -16.5) * mm, "mid": v(63.77, -16.48) * mm, "end": v(64.03, -16.15) * mm});
            skArc(sketch, "E62.37.35.0", {"start": v(60.32, -19.56) * mm, "mid": v(60.4, -19.61) * mm, "end": v(60.48, -19.65) * mm});
            skArc(sketch, "E62.41.35.0", {"start": v(58.47, -17.38) * mm, "mid": v(58.45, -17.65) * mm, "end": v(58.57, -17.89) * mm});
            skArc(sketch, "E62.45.35.0", {"start": v(61.85, -15.9) * mm, "mid": v(61.76, -15.88) * mm, "end": v(61.67, -15.87) * mm});
            skArc(sketch, "E62.1.36.0", {"start": v(63.17, -8.01) * mm, "mid": v(61.97, -8.2) * mm, "end": v(60.78, -8.5) * mm});
            skLineSegment(sketch, "E62.5.36.0", {"start": v(62.47, -11.92) * mm, "end": v(64.37, -12.28) * mm});
            skArc(sketch, "E62.8.36.0", {"start": v(62.3, -11.85) * mm, "mid": v(61.3, -11.16) * mm, "end": v(60.35, -10.4) * mm});
            skPoint(sketch, "E62.9.36.0", {"position": v(65.48, -8.57) * mm});
            skLineSegment(sketch, "E62.12.36.0", {"start": v(63.36, -8.03) * mm, "end": v(64.92, -8.43) * mm});
            skPoint(sketch, "E62.15.36.0", {"position": v(60.49, -8.58) * mm});
            skPoint(sketch, "E62.16.36.0", {"position": v(62.38, -11.9) * mm});
            skPoint(sketch, "E62.17.36.0", {"position": v(60.12, -10.2) * mm});
            skPoint(sketch, "E62.18.36.0", {"position": v(64.87, -12.37) * mm});
            skLineSegment(sketch, "E62.19.36.0", {"start": v(60.18, -9.92) * mm, "end": v(60.3, -9.4) * mm});
            skLineSegment(sketch, "E62.22.36.0", {"start": v(60.42, -8.87) * mm, "end": v(60.3, -9.4) * mm});
            skArc(sketch, "E62.25.36.0", {"start": v(60.78, -8.5) * mm, "mid": v(60.55, -8.63) * mm, "end": v(60.42, -8.87) * mm});
            skArc(sketch, "E62.29.36.0", {"start": v(64.77, -12.88) * mm, "mid": v(64.7, -12.5) * mm, "end": v(64.37, -12.28) * mm});
            skArc(sketch, "E62.33.36.0", {"start": v(64.92, -8.43) * mm, "mid": v(65.34, -8.36) * mm, "end": v(65.55, -8) * mm});
            skArc(sketch, "E62.37.36.0", {"start": v(62.3, -11.85) * mm, "mid": v(62.38, -11.9) * mm, "end": v(62.47, -11.92) * mm});
            skArc(sketch, "E62.41.36.0", {"start": v(60.18, -9.92) * mm, "mid": v(60.2, -10.18) * mm, "end": v(60.35, -10.4) * mm});
            skArc(sketch, "E62.45.36.0", {"start": v(63.36, -8.03) * mm, "mid": v(63.27, -8.01) * mm, "end": v(63.17, -8.01) * mm});
            skArc(sketch, "E62.1.37.0", {"start": v(63.68, -0.03) * mm, "mid": v(62.5, -0.38) * mm, "end": v(61.36, -0.8) * mm});
            skLineSegment(sketch, "E62.5.37.0", {"start": v(63.47, -4) * mm, "end": v(65.4, -4.11) * mm});
            skArc(sketch, "E62.8.37.0", {"start": v(63.29, -3.95) * mm, "mid": v(62.2, -3.4) * mm, "end": v(61.18, -2.76) * mm});
            skPoint(sketch, "E62.9.37.0", {"position": v(66.04, -0.3) * mm});
            skLineSegment(sketch, "E62.12.37.0", {"start": v(63.87, -0.02) * mm, "end": v(65.47, -0.22) * mm});
            skPoint(sketch, "E62.15.37.0", {"position": v(61.09, -0.93) * mm});
            skPoint(sketch, "E62.16.37.0", {"position": v(63.37, -3.99) * mm});
            skPoint(sketch, "E62.17.37.0", {"position": v(60.93, -2.6) * mm});
            skPoint(sketch, "E62.18.37.0", {"position": v(65.9, -4.15) * mm});
            skLineSegment(sketch, "E62.19.37.0", {"start": v(60.95, -2.3) * mm, "end": v(61, -1.76) * mm});
            skLineSegment(sketch, "E62.22.37.0", {"start": v(61.05, -1.22) * mm, "end": v(61, -1.76) * mm});
            skArc(sketch, "E62.25.37.0", {"start": v(61.36, -0.8) * mm, "mid": v(61.15, -0.97) * mm, "end": v(61.05, -1.22) * mm});
            skArc(sketch, "E62.29.37.0", {"start": v(65.88, -4.66) * mm, "mid": v(65.75, -4.29) * mm, "end": v(65.4, -4.11) * mm});
            skArc(sketch, "E62.33.37.0", {"start": v(65.47, -0.22) * mm, "mid": v(65.87, -0.1) * mm, "end": v(66.04, 0.28) * mm});
            skArc(sketch, "E62.37.37.0", {"start": v(63.29, -3.95) * mm, "mid": v(63.38, -3.98) * mm, "end": v(63.47, -4) * mm});
            skArc(sketch, "E62.41.37.0", {"start": v(60.95, -2.3) * mm, "mid": v(61, -2.56) * mm, "end": v(61.18, -2.76) * mm});
            skArc(sketch, "E62.45.37.0", {"start": v(63.87, -0.02) * mm, "mid": v(63.77, -0.02) * mm, "end": v(63.68, -0.03) * mm});
            skArc(sketch, "E62.1.38.0", {"start": v(63.18, 7.95) * mm, "mid": v(62.06, 7.46) * mm, "end": v(60.98, 6.89) * mm});
            skLineSegment(sketch, "E62.5.38.0", {"start": v(63.47, 4) * mm, "end": v(65.4, 4.11) * mm});
            skArc(sketch, "E62.8.38.0", {"start": v(63.28, 4.02) * mm, "mid": v(62.14, 4.43) * mm, "end": v(61.04, 4.93) * mm});
            skPoint(sketch, "E62.9.38.0", {"position": v(65.56, 7.98) * mm});
            skLineSegment(sketch, "E62.12.38.0", {"start": v(63.37, 7.98) * mm, "end": v(64.98, 7.98) * mm});
            skPoint(sketch, "E62.15.38.0", {"position": v(60.72, 6.73) * mm});
            skPoint(sketch, "E62.16.38.0", {"position": v(63.37, 3.99) * mm});
            skPoint(sketch, "E62.17.38.0", {"position": v(60.77, 5.07) * mm});
            skPoint(sketch, "E62.18.38.0", {"position": v(65.9, 4.15) * mm});
            skLineSegment(sketch, "E62.19.38.0", {"start": v(60.76, 5.36) * mm, "end": v(60.74, 5.9) * mm});
            skLineSegment(sketch, "E62.22.38.0", {"start": v(60.73, 6.44) * mm, "end": v(60.74, 5.9) * mm});
            skArc(sketch, "E62.25.38.0", {"start": v(60.98, 6.89) * mm, "mid": v(60.8, 6.7) * mm, "end": v(60.73, 6.44) * mm});
            skArc(sketch, "E62.29.38.0", {"start": v(65.94, 3.64) * mm, "mid": v(65.77, 3.99) * mm, "end": v(65.4, 4.11) * mm});
            skArc(sketch, "E62.33.38.0", {"start": v(64.98, 7.98) * mm, "mid": v(65.36, 8.16) * mm, "end": v(65.48, 8.56) * mm});
            skArc(sketch, "E62.37.38.0", {"start": v(63.28, 4.02) * mm, "mid": v(63.37, 4) * mm, "end": v(63.47, 4) * mm});
            skArc(sketch, "E62.41.38.0", {"start": v(60.76, 5.36) * mm, "mid": v(60.84, 5.1) * mm, "end": v(61.04, 4.93) * mm});
            skArc(sketch, "E62.45.38.0", {"start": v(63.37, 7.98) * mm, "mid": v(63.27, 7.97) * mm, "end": v(63.18, 7.95) * mm});
            skArc(sketch, "E62.1.39.0", {"start": v(61.69, 15.8) * mm, "mid": v(60.64, 15.18) * mm, "end": v(59.64, 14.48) * mm});
            skLineSegment(sketch, "E62.5.39.0", {"start": v(62.47, 11.92) * mm, "end": v(64.37, 12.28) * mm});
            skArc(sketch, "E62.8.39.0", {"start": v(62.28, 11.92) * mm, "mid": v(61.1, 12.18) * mm, "end": v(59.94, 12.54) * mm});
            skPoint(sketch, "E62.9.39.0", {"position": v(64.04, 16.14) * mm});
            skLineSegment(sketch, "E62.12.39.0", {"start": v(61.86, 15.86) * mm, "end": v(63.47, 16.06) * mm});
            skPoint(sketch, "E62.15.39.0", {"position": v(59.4, 14.3) * mm});
            skPoint(sketch, "E62.16.39.0", {"position": v(62.38, 11.9) * mm});
            skPoint(sketch, "E62.17.39.0", {"position": v(59.66, 12.64) * mm});
            skPoint(sketch, "E62.18.39.0", {"position": v(64.87, 12.37) * mm});
            skLineSegment(sketch, "E62.19.39.0", {"start": v(59.6, 12.93) * mm, "end": v(59.52, 13.47) * mm});
            skLineSegment(sketch, "E62.22.39.0", {"start": v(59.44, 14) * mm, "end": v(59.52, 13.47) * mm});
            skArc(sketch, "E62.25.39.0", {"start": v(59.64, 14.48) * mm, "mid": v(59.47, 14.26) * mm, "end": v(59.44, 14) * mm});
            skArc(sketch, "E62.29.39.0", {"start": v(64.96, 11.87) * mm, "mid": v(64.75, 12.2) * mm, "end": v(64.37, 12.28) * mm});
            skArc(sketch, "E62.33.39.0", {"start": v(63.47, 16.06) * mm, "mid": v(63.82, 16.28) * mm, "end": v(63.9, 16.7) * mm});
            skArc(sketch, "E62.37.39.0", {"start": v(62.28, 11.92) * mm, "mid": v(62.37, 11.9) * mm, "end": v(62.47, 11.92) * mm});
            skArc(sketch, "E62.41.39.0", {"start": v(59.6, 12.93) * mm, "mid": v(59.72, 12.7) * mm, "end": v(59.94, 12.54) * mm});
            skArc(sketch, "E62.45.39.0", {"start": v(61.86, 15.86) * mm, "mid": v(61.77, 15.84) * mm, "end": v(61.69, 15.8) * mm});
            skArc(sketch, "E62.1.40.0", {"start": v(59.22, 23.41) * mm, "mid": v(58.25, 22.66) * mm, "end": v(57.35, 21.84) * mm});
            skLineSegment(sketch, "E62.5.40.0", {"start": v(60.48, 19.65) * mm, "end": v(62.32, 20.25) * mm});
            skArc(sketch, "E62.8.40.0", {"start": v(60.3, 19.63) * mm, "mid": v(59.1, 19.75) * mm, "end": v(57.9, 19.95) * mm});
            skPoint(sketch, "E62.9.40.0", {"position": v(61.51, 24.03) * mm});
            skLineSegment(sketch, "E62.12.40.0", {"start": v(59.39, 23.49) * mm, "end": v(60.95, 23.9) * mm});
            skPoint(sketch, "E62.15.40.0", {"position": v(57.14, 21.62) * mm});
            skPoint(sketch, "E62.16.40.0", {"position": v(60.4, 19.62) * mm});
            skPoint(sketch, "E62.17.40.0", {"position": v(57.6, 20.02) * mm});
            skPoint(sketch, "E62.18.40.0", {"position": v(62.8, 20.4) * mm});
            skLineSegment(sketch, "E62.19.40.0", {"start": v(57.52, 20.3) * mm, "end": v(57.36, 20.82) * mm});
            skLineSegment(sketch, "E62.22.40.0", {"start": v(57.22, 21.34) * mm, "end": v(57.36, 20.82) * mm});
            skArc(sketch, "E62.25.40.0", {"start": v(57.35, 21.84) * mm, "mid": v(57.22, 21.6) * mm, "end": v(57.22, 21.34) * mm});
            skArc(sketch, "E62.29.40.0", {"start": v(62.96, 19.92) * mm, "mid": v(62.71, 20.22) * mm, "end": v(62.32, 20.25) * mm});
            skArc(sketch, "E62.33.40.0", {"start": v(60.95, 23.9) * mm, "mid": v(61.28, 24.15) * mm, "end": v(61.3, 24.57) * mm});
            skArc(sketch, "E62.37.40.0", {"start": v(60.3, 19.63) * mm, "mid": v(60.4, 19.63) * mm, "end": v(60.48, 19.65) * mm});
            skArc(sketch, "E62.41.40.0", {"start": v(57.52, 20.3) * mm, "mid": v(57.66, 20.08) * mm, "end": v(57.9, 19.95) * mm});
            skArc(sketch, "E62.45.40.0", {"start": v(59.39, 23.49) * mm, "mid": v(59.3, 23.46) * mm, "end": v(59.22, 23.41) * mm});
            skArc(sketch, "E62.1.41.0", {"start": v(55.82, 30.65) * mm, "mid": v(54.96, 29.78) * mm, "end": v(54.16, 28.85) * mm});
            skLineSegment(sketch, "E62.5.41.0", {"start": v(57.54, 27.08) * mm, "end": v(59.3, 27.9) * mm});
            skArc(sketch, "E62.8.41.0", {"start": v(57.36, 27.03) * mm, "mid": v(56.15, 27) * mm, "end": v(54.94, 27.05) * mm});
            skPoint(sketch, "E62.9.41.0", {"position": v(58.01, 31.55) * mm});
            skLineSegment(sketch, "E62.12.41.0", {"start": v(55.98, 30.75) * mm, "end": v(57.48, 31.34) * mm});
            skPoint(sketch, "E62.15.41.0", {"position": v(53.98, 28.61) * mm});
            skPoint(sketch, "E62.16.41.0", {"position": v(57.46, 27.04) * mm});
            skPoint(sketch, "E62.17.41.0", {"position": v(54.64, 27.08) * mm});
            skPoint(sketch, "E62.18.41.0", {"position": v(59.75, 28.12) * mm});
            skLineSegment(sketch, "E62.19.41.0", {"start": v(54.52, 27.35) * mm, "end": v(54.3, 27.84) * mm});
            skLineSegment(sketch, "E62.22.41.0", {"start": v(54.1, 28.34) * mm, "end": v(54.3, 27.84) * mm});
            skArc(sketch, "E62.25.41.0", {"start": v(54.16, 28.85) * mm, "mid": v(54.06, 28.6) * mm, "end": v(54.1, 28.34) * mm});
            skArc(sketch, "E62.29.41.0", {"start": v(59.97, 27.65) * mm, "mid": v(59.68, 27.92) * mm, "end": v(59.3, 27.9) * mm});
            skArc(sketch, "E62.33.41.0", {"start": v(57.48, 31.34) * mm, "mid": v(57.77, 31.64) * mm, "end": v(57.74, 32.06) * mm});
            skArc(sketch, "E62.37.41.0", {"start": v(57.36, 27.03) * mm, "mid": v(57.45, 27.05) * mm, "end": v(57.54, 27.08) * mm});
            skArc(sketch, "E62.41.41.0", {"start": v(54.52, 27.35) * mm, "mid": v(54.69, 27.15) * mm, "end": v(54.94, 27.05) * mm});
            skArc(sketch, "E62.45.41.0", {"start": v(55.98, 30.75) * mm, "mid": v(55.9, 30.7) * mm, "end": v(55.82, 30.65) * mm});
            skArc(sketch, "E62.1.42.0", {"start": v(51.54, 37.4) * mm, "mid": v(50.79, 36.43) * mm, "end": v(50.12, 35.41) * mm});
            skLineSegment(sketch, "E62.5.42.0", {"start": v(53.7, 34.08) * mm, "end": v(55.33, 35.11) * mm});
            skArc(sketch, "E62.8.42.0", {"start": v(53.52, 34) * mm, "mid": v(52.32, 33.82) * mm, "end": v(51.12, 33.73) * mm});
            skPoint(sketch, "E62.9.42.0", {"position": v(53.6, 38.58) * mm});
            skLineSegment(sketch, "E62.12.42.0", {"start": v(51.68, 37.52) * mm, "end": v(53.1, 38.3) * mm});
            skPoint(sketch, "E62.15.42.0", {"position": v(49.97, 35.15) * mm});
            skPoint(sketch, "E62.16.42.0", {"position": v(53.61, 34.03) * mm});
            skPoint(sketch, "E62.17.42.0", {"position": v(50.82, 33.72) * mm});
            skPoint(sketch, "E62.18.42.0", {"position": v(55.76, 35.39) * mm});
            skLineSegment(sketch, "E62.19.42.0", {"start": v(50.66, 33.97) * mm, "end": v(50.38, 34.43) * mm});
            skLineSegment(sketch, "E62.22.42.0", {"start": v(50.11, 34.9) * mm, "end": v(50.38, 34.43) * mm});
            skArc(sketch, "E62.25.42.0", {"start": v(50.12, 35.41) * mm, "mid": v(50.05, 35.16) * mm, "end": v(50.11, 34.9) * mm});
            skArc(sketch, "E62.29.42.0", {"start": v(56.03, 34.95) * mm, "mid": v(55.71, 35.18) * mm, "end": v(55.33, 35.11) * mm});
            skArc(sketch, "E62.33.42.0", {"start": v(53.1, 38.3) * mm, "mid": v(53.35, 38.63) * mm, "end": v(53.26, 39.04) * mm});
            skArc(sketch, "E62.37.42.0", {"start": v(53.52, 34) * mm, "mid": v(53.61, 34.03) * mm, "end": v(53.7, 34.08) * mm});
            skArc(sketch, "E62.41.42.0", {"start": v(50.66, 33.97) * mm, "mid": v(50.86, 33.79) * mm, "end": v(51.12, 33.73) * mm});
            skArc(sketch, "E62.45.42.0", {"start": v(51.68, 37.52) * mm, "mid": v(51.6, 37.47) * mm, "end": v(51.54, 37.4) * mm});
            skArc(sketch, "E62.1.43.0", {"start": v(46.44, 43.57) * mm, "mid": v(45.82, 42.51) * mm, "end": v(45.28, 41.42) * mm});
            skLineSegment(sketch, "E62.5.43.0", {"start": v(49, 40.54) * mm, "end": v(50.5, 41.77) * mm});
            skArc(sketch, "E62.8.43.0", {"start": v(48.84, 40.45) * mm, "mid": v(47.67, 40.11) * mm, "end": v(46.49, 39.87) * mm});
            skPoint(sketch, "E62.9.43.0", {"position": v(48.34, 45) * mm});
            skLineSegment(sketch, "E62.12.43.0", {"start": v(46.57, 43.7) * mm, "end": v(47.88, 44.65) * mm});
            skPoint(sketch, "E62.15.43.0", {"position": v(45.17, 41.14) * mm});
            skPoint(sketch, "E62.16.43.0", {"position": v(48.93, 40.48) * mm});
            skPoint(sketch, "E62.17.43.0", {"position": v(46.19, 39.82) * mm});
            skPoint(sketch, "E62.18.43.0", {"position": v(50.88, 42.1) * mm});
            skLineSegment(sketch, "E62.19.43.0", {"start": v(46, 40.05) * mm, "end": v(45.67, 40.47) * mm});
            skLineSegment(sketch, "E62.22.43.0", {"start": v(45.34, 40.9) * mm, "end": v(45.67, 40.47) * mm});
            skArc(sketch, "E62.25.43.0", {"start": v(45.28, 41.42) * mm, "mid": v(45.24, 41.15) * mm, "end": v(45.34, 40.9) * mm});
            skArc(sketch, "E62.29.43.0", {"start": v(51.2, 41.7) * mm, "mid": v(50.87, 41.88) * mm, "end": v(50.5, 41.77) * mm});
            skArc(sketch, "E62.33.43.0", {"start": v(47.88, 44.65) * mm, "mid": v(48.08, 45.02) * mm, "end": v(47.95, 45.41) * mm});
            skArc(sketch, "E62.37.43.0", {"start": v(48.84, 40.45) * mm, "mid": v(48.92, 40.48) * mm, "end": v(49, 40.54) * mm});
            skArc(sketch, "E62.41.43.0", {"start": v(46, 40.05) * mm, "mid": v(46.22, 39.9) * mm, "end": v(46.49, 39.87) * mm});
            skArc(sketch, "E62.45.43.0", {"start": v(46.57, 43.7) * mm, "mid": v(46.5, 43.64) * mm, "end": v(46.44, 43.57) * mm});
            skArc(sketch, "E62.1.44.0", {"start": v(40.62, 49.04) * mm, "mid": v(40.13, 47.92) * mm, "end": v(39.74, 46.76) * mm});
            skLineSegment(sketch, "E62.5.44.0", {"start": v(43.53, 46.36) * mm, "end": v(44.86, 47.77) * mm});
            skArc(sketch, "E62.8.44.0", {"start": v(43.38, 46.25) * mm, "mid": v(42.27, 45.77) * mm, "end": v(41.12, 45.38) * mm});
            skPoint(sketch, "E62.9.44.0", {"position": v(42.32, 50.7) * mm});
            skLineSegment(sketch, "E62.12.44.0", {"start": v(40.73, 49.2) * mm, "end": v(41.9, 50.3) * mm});
            skPoint(sketch, "E62.15.44.0", {"position": v(39.65, 46.48) * mm});
            skPoint(sketch, "E62.16.44.0", {"position": v(43.47, 46.29) * mm});
            skPoint(sketch, "E62.17.44.0", {"position": v(40.83, 45.3) * mm});
            skPoint(sketch, "E62.18.44.0", {"position": v(45.2, 48.14) * mm});
            skLineSegment(sketch, "E62.19.44.0", {"start": v(40.62, 45.5) * mm, "end": v(40.24, 45.88) * mm});
            skLineSegment(sketch, "E62.22.44.0", {"start": v(39.86, 46.26) * mm, "end": v(40.24, 45.88) * mm});
            skArc(sketch, "E62.25.44.0", {"start": v(39.74, 46.76) * mm, "mid": v(39.73, 46.5) * mm, "end": v(39.86, 46.26) * mm});
            skArc(sketch, "E62.29.44.0", {"start": v(45.58, 47.79) * mm, "mid": v(45.21, 47.93) * mm, "end": v(44.86, 47.77) * mm});
            skArc(sketch, "E62.33.44.0", {"start": v(41.9, 50.3) * mm, "mid": v(42.06, 50.69) * mm, "end": v(41.88, 51.06) * mm});
            skArc(sketch, "E62.37.44.0", {"start": v(43.38, 46.25) * mm, "mid": v(43.46, 46.3) * mm, "end": v(43.53, 46.36) * mm});
            skArc(sketch, "E62.41.44.0", {"start": v(40.62, 45.5) * mm, "mid": v(40.86, 45.37) * mm, "end": v(41.12, 45.38) * mm});
            skArc(sketch, "E62.45.44.0", {"start": v(40.73, 49.2) * mm, "mid": v(40.66, 49.12) * mm, "end": v(40.62, 49.04) * mm});
            skArc(sketch, "E62.1.45.0", {"start": v(34.15, 53.75) * mm, "mid": v(33.81, 52.57) * mm, "end": v(33.56, 51.38) * mm});
            skLineSegment(sketch, "E62.5.45.0", {"start": v(37.38, 51.45) * mm, "end": v(38.52, 53.01) * mm});
            skArc(sketch, "E62.8.45.0", {"start": v(37.24, 51.32) * mm, "mid": v(36.2, 50.7) * mm, "end": v(35.11, 50.17) * mm});
            skPoint(sketch, "E62.9.45.0", {"position": v(35.64, 55.6) * mm});
            skLineSegment(sketch, "E62.12.45.0", {"start": v(34.24, 53.91) * mm, "end": v(35.27, 55.16) * mm});
            skPoint(sketch, "E62.15.45.0", {"position": v(33.52, 51.08) * mm});
            skPoint(sketch, "E62.16.45.0", {"position": v(37.32, 51.37) * mm});
            skPoint(sketch, "E62.17.45.0", {"position": v(34.84, 50.06) * mm});
            skPoint(sketch, "E62.18.45.0", {"position": v(38.82, 53.43) * mm});
            skLineSegment(sketch, "E62.19.45.0", {"start": v(34.6, 50.23) * mm, "end": v(34.17, 50.56) * mm});
            skLineSegment(sketch, "E62.22.45.0", {"start": v(33.75, 50.9) * mm, "end": v(34.17, 50.56) * mm});
            skArc(sketch, "E62.25.45.0", {"start": v(33.56, 51.38) * mm, "mid": v(33.59, 51.11) * mm, "end": v(33.75, 50.9) * mm});
            skArc(sketch, "E62.29.45.0", {"start": v(39.23, 53.12) * mm, "mid": v(38.85, 53.22) * mm, "end": v(38.52, 53.01) * mm});
            skArc(sketch, "E62.33.45.0", {"start": v(35.27, 55.16) * mm, "mid": v(35.38, 55.56) * mm, "end": v(35.15, 55.9) * mm});
            skArc(sketch, "E62.37.45.0", {"start": v(37.24, 51.32) * mm, "mid": v(37.32, 51.38) * mm, "end": v(37.38, 51.45) * mm});
            skArc(sketch, "E62.41.45.0", {"start": v(34.6, 50.23) * mm, "mid": v(34.85, 50.13) * mm, "end": v(35.11, 50.17) * mm});
            skArc(sketch, "E62.45.45.0", {"start": v(34.24, 53.91) * mm, "mid": v(34.19, 53.83) * mm, "end": v(34.15, 53.75) * mm});
            skArc(sketch, "E62.1.46.0", {"start": v(27.14, 57.6) * mm, "mid": v(26.95, 56.4) * mm, "end": v(26.86, 55.18) * mm});
            skLineSegment(sketch, "E62.5.46.0", {"start": v(30.64, 55.73) * mm, "end": v(31.57, 57.42) * mm});
            skArc(sketch, "E62.8.46.0", {"start": v(30.52, 55.58) * mm, "mid": v(29.56, 54.84) * mm, "end": v(28.55, 54.18) * mm});
            skPoint(sketch, "E62.9.46.0", {"position": v(28.39, 59.63) * mm});
            skLineSegment(sketch, "E62.12.46.0", {"start": v(27.21, 57.78) * mm, "end": v(28.08, 59.14) * mm});
            skPoint(sketch, "E62.15.46.0", {"position": v(26.85, 54.88) * mm});
            skPoint(sketch, "E62.16.46.0", {"position": v(30.6, 55.65) * mm});
            skPoint(sketch, "E62.17.46.0", {"position": v(28.29, 54.03) * mm});
            skPoint(sketch, "E62.18.46.0", {"position": v(31.82, 57.87) * mm});
            skLineSegment(sketch, "E62.19.46.0", {"start": v(28.03, 54.17) * mm, "end": v(27.56, 54.44) * mm});
            skLineSegment(sketch, "E62.22.46.0", {"start": v(27.1, 54.72) * mm, "end": v(27.56, 54.44) * mm});
            skArc(sketch, "E62.25.46.0", {"start": v(26.86, 55.18) * mm, "mid": v(26.92, 54.92) * mm, "end": v(27.1, 54.72) * mm});
            skArc(sketch, "E62.29.46.0", {"start": v(32.26, 57.62) * mm, "mid": v(31.87, 57.67) * mm, "end": v(31.57, 57.42) * mm});
            skArc(sketch, "E62.33.46.0", {"start": v(28.08, 59.14) * mm, "mid": v(28.14, 59.56) * mm, "end": v(27.86, 59.87) * mm});
            skArc(sketch, "E62.37.46.0", {"start": v(30.52, 55.58) * mm, "mid": v(30.58, 55.65) * mm, "end": v(30.64, 55.73) * mm});
            skArc(sketch, "E62.41.46.0", {"start": v(28.03, 54.17) * mm, "mid": v(28.29, 54.1) * mm, "end": v(28.55, 54.18) * mm});
            skArc(sketch, "E62.45.46.0", {"start": v(27.21, 57.78) * mm, "mid": v(27.17, 57.7) * mm, "end": v(27.14, 57.6) * mm});
            skArc(sketch, "E62.1.47.0", {"start": v(19.7, 60.55) * mm, "mid": v(19.67, 59.33) * mm, "end": v(19.73, 58.1) * mm});
            skLineSegment(sketch, "E62.5.47.0", {"start": v(23.41, 59.13) * mm, "end": v(24.12, 60.93) * mm});
            skArc(sketch, "E62.8.47.0", {"start": v(23.31, 58.97) * mm, "mid": v(22.45, 58.12) * mm, "end": v(21.53, 57.33) * mm});
            skPoint(sketch, "E62.9.47.0", {"position": v(20.69, 62.72) * mm});
            skLineSegment(sketch, "E62.12.47.0", {"start": v(19.76, 60.73) * mm, "end": v(20.44, 62.2) * mm});
            skPoint(sketch, "E62.15.47.0", {"position": v(19.76, 57.8) * mm});
            skPoint(sketch, "E62.16.47.0", {"position": v(23.38, 59.04) * mm});
            skPoint(sketch, "E62.17.47.0", {"position": v(21.3, 57.15) * mm});
            skPoint(sketch, "E62.18.47.0", {"position": v(24.31, 61.4) * mm});
            skLineSegment(sketch, "E62.19.47.0", {"start": v(21.02, 57.26) * mm, "end": v(20.52, 57.47) * mm});
            skLineSegment(sketch, "E62.22.47.0", {"start": v(20.03, 57.69) * mm, "end": v(20.52, 57.47) * mm});
            skArc(sketch, "E62.25.47.0", {"start": v(19.73, 58.1) * mm, "mid": v(19.82, 57.86) * mm, "end": v(20.03, 57.69) * mm});
            skArc(sketch, "E62.29.47.0", {"start": v(24.79, 61.21) * mm, "mid": v(24.4, 61.2) * mm, "end": v(24.12, 60.93) * mm});
            skArc(sketch, "E62.33.47.0", {"start": v(20.44, 62.2) * mm, "mid": v(20.45, 62.61) * mm, "end": v(20.14, 62.9) * mm});
            skArc(sketch, "E62.37.47.0", {"start": v(23.31, 58.97) * mm, "mid": v(23.37, 59.04) * mm, "end": v(23.41, 59.13) * mm});
            skArc(sketch, "E62.41.47.0", {"start": v(21.02, 57.26) * mm, "mid": v(21.28, 57.23) * mm, "end": v(21.53, 57.33) * mm});
            skArc(sketch, "E62.45.47.0", {"start": v(19.76, 60.73) * mm, "mid": v(19.72, 60.64) * mm, "end": v(19.7, 60.55) * mm});
            skArc(sketch, "E62.1.48.0", {"start": v(11.97, 62.54) * mm, "mid": v(12.08, 61.33) * mm, "end": v(12.3, 60.12) * mm});
            skLineSegment(sketch, "E62.5.48.0", {"start": v(15.82, 61.6) * mm, "end": v(16.3, 63.47) * mm});
            skArc(sketch, "E62.8.48.0", {"start": v(15.74, 61.43) * mm, "mid": v(15, 60.47) * mm, "end": v(14.17, 59.58) * mm});
            skPoint(sketch, "E62.9.48.0", {"position": v(12.67, 64.81) * mm});
            skLineSegment(sketch, "E62.12.48.0", {"start": v(11.99, 62.73) * mm, "end": v(12.49, 64.27) * mm});
            skPoint(sketch, "E62.15.48.0", {"position": v(12.36, 59.83) * mm});
            skPoint(sketch, "E62.16.48.0", {"position": v(15.8, 61.5) * mm});
            skPoint(sketch, "E62.17.48.0", {"position": v(13.96, 59.36) * mm});
            skPoint(sketch, "E62.18.48.0", {"position": v(16.42, 63.97) * mm});
            skLineSegment(sketch, "E62.19.48.0", {"start": v(13.68, 59.44) * mm, "end": v(13.16, 59.59) * mm});
            skLineSegment(sketch, "E62.22.48.0", {"start": v(12.64, 59.74) * mm, "end": v(13.16, 59.59) * mm});
            skArc(sketch, "E62.25.48.0", {"start": v(12.3, 60.12) * mm, "mid": v(12.42, 59.89) * mm, "end": v(12.64, 59.74) * mm});
            skArc(sketch, "E62.29.48.0", {"start": v(16.92, 63.84) * mm, "mid": v(16.53, 63.78) * mm, "end": v(16.3, 63.47) * mm});
            skArc(sketch, "E62.33.48.0", {"start": v(12.49, 64.27) * mm, "mid": v(12.44, 64.68) * mm, "end": v(12.1, 64.92) * mm});
            skArc(sketch, "E62.37.48.0", {"start": v(15.74, 61.43) * mm, "mid": v(15.78, 61.5) * mm, "end": v(15.82, 61.6) * mm});
            skArc(sketch, "E62.41.48.0", {"start": v(13.68, 59.44) * mm, "mid": v(13.94, 59.44) * mm, "end": v(14.17, 59.58) * mm});
            skArc(sketch, "E62.45.48.0", {"start": v(11.99, 62.73) * mm, "mid": v(11.97, 62.64) * mm, "end": v(11.97, 62.54) * mm});
            skArc(sketch, "E62.1.49.0", {"start": v(4.03, 63.55) * mm, "mid": v(4.3, 62.36) * mm, "end": v(4.66, 61.2) * mm});
            skLineSegment(sketch, "E62.5.49.0", {"start": v(7.97, 63.1) * mm, "end": v(8.21, 65.01) * mm});
            skArc(sketch, "E62.8.49.0", {"start": v(7.91, 62.91) * mm, "mid": v(7.3, 61.87) * mm, "end": v(6.6, 60.88) * mm});
            skPoint(sketch, "E62.9.49.0", {"position": v(4.44, 65.9) * mm});
            skLineSegment(sketch, "E62.12.49.0", {"start": v(4.03, 63.74) * mm, "end": v(4.33, 65.32) * mm});
            skPoint(sketch, "E62.15.49.0", {"position": v(4.76, 60.9) * mm});
            skPoint(sketch, "E62.16.49.0", {"position": v(7.96, 63) * mm});
            skPoint(sketch, "E62.17.49.0", {"position": v(6.41, 60.65) * mm});
            skPoint(sketch, "E62.18.49.0", {"position": v(8.28, 65.52) * mm});
            skLineSegment(sketch, "E62.19.49.0", {"start": v(6.12, 60.69) * mm, "end": v(5.59, 60.77) * mm});
            skLineSegment(sketch, "E62.22.49.0", {"start": v(5.05, 60.86) * mm, "end": v(5.59, 60.77) * mm});
            skArc(sketch, "E62.25.49.0", {"start": v(4.66, 61.2) * mm, "mid": v(4.81, 60.97) * mm, "end": v(5.05, 60.86) * mm});
            skArc(sketch, "E62.29.49.0", {"start": v(8.78, 65.45) * mm, "mid": v(8.4, 65.35) * mm, "end": v(8.21, 65.01) * mm});
            skArc(sketch, "E62.33.49.0", {"start": v(4.33, 65.32) * mm, "mid": v(4.24, 65.73) * mm, "end": v(3.87, 65.93) * mm});
            skArc(sketch, "E62.37.49.0", {"start": v(7.91, 62.91) * mm, "mid": v(7.95, 63) * mm, "end": v(7.97, 63.1) * mm});
            skArc(sketch, "E62.41.49.0", {"start": v(6.12, 60.69) * mm, "mid": v(6.38, 60.72) * mm, "end": v(6.6, 60.88) * mm});
            skArc(sketch, "E62.45.49.0", {"start": v(4.03, 63.74) * mm, "mid": v(4.02, 63.64) * mm, "end": v(4.03, 63.55) * mm});
            skArc(sketch, "E63.trimOffspring", {"start": v(-12.08, 64.93) * mm, "mid": v(6.07, -65.76) * mm, "end": v(0, 66.04) * mm});
            skSolve(sketch);
        }
        {
            var Q0;
            Q0=makeQuery(id+"F2.imprint","IMPRINT",FACE,{"disambiguationData":[TD([[makeQuery(id+"F2.imprint","IMPRINT",EDGE,{"derivedFrom":sQuery(id+"F2.wireOp",EDGE,"E48.MirrorCS")}),-1.0]])]});
            var Q1;
            Q1=makeQuery(id+"F2.imprint","IMPRINT",FACE,{"disambiguationData":[TD([[makeQuery(id+"F2.imprint","IMPRINT",EDGE,{"derivedFrom":sQuery(id+"F2.wireOp",EDGE,"E62.1.49.0")}),1.0]])]});
            var Q2;
            Q2=makeQuery(id+"F2.imprint","IMPRINT",FACE,{"disambiguationData":[TD([[makeQuery(id+"F2.imprint","IMPRINT",EDGE,{"derivedFrom":sQuery(id+"F2.wireOp",EDGE,"E62.1.48.0")}),1.0]])]});
            var Q3;
            Q3=makeQuery(id+"F2.imprint","IMPRINT",FACE,{"disambiguationData":[TD([[makeQuery(id+"F2.imprint","IMPRINT",EDGE,{"derivedFrom":sQuery(id+"F2.wireOp",EDGE,"E62.1.47.0")}),1.0]])]});
            var Q4;
            Q4=makeQuery(id+"F2.imprint","IMPRINT",FACE,{"disambiguationData":[TD([[makeQuery(id+"F2.imprint","IMPRINT",EDGE,{"derivedFrom":sQuery(id+"F2.wireOp",EDGE,"E62.1.46.0")}),1.0]])]});
            var Q5;
            Q5=makeQuery(id+"F2.imprint","IMPRINT",FACE,{"disambiguationData":[TD([[makeQuery(id+"F2.imprint","IMPRINT",EDGE,{"derivedFrom":sQuery(id+"F2.wireOp",EDGE,"E62.1.45.0")}),1.0]])]});
            var Q6;
            Q6=makeQuery(id+"F2.imprint","IMPRINT",FACE,{"disambiguationData":[TD([[makeQuery(id+"F2.imprint","IMPRINT",EDGE,{"derivedFrom":sQuery(id+"F2.wireOp",EDGE,"E62.1.44.0")}),1.0]])]});
            var Q7;
            Q7=makeQuery(id+"F2.imprint","IMPRINT",FACE,{"disambiguationData":[TD([[makeQuery(id+"F2.imprint","IMPRINT",EDGE,{"derivedFrom":sQuery(id+"F2.wireOp",EDGE,"E62.1.43.0")}),1.0]])]});
            var Q8;
            Q8=makeQuery(id+"F2.imprint","IMPRINT",FACE,{"disambiguationData":[TD([[makeQuery(id+"F2.imprint","IMPRINT",EDGE,{"derivedFrom":sQuery(id+"F2.wireOp",EDGE,"E62.1.42.0")}),1.0]])]});
            var Q9;
            Q9=makeQuery(id+"F2.imprint","IMPRINT",FACE,{"disambiguationData":[TD([[makeQuery(id+"F2.imprint","IMPRINT",EDGE,{"derivedFrom":sQuery(id+"F2.wireOp",EDGE,"E62.1.41.0")}),1.0]])]});
            var Q10;
            Q10=makeQuery(id+"F2.imprint","IMPRINT",FACE,{"disambiguationData":[TD([[makeQuery(id+"F2.imprint","IMPRINT",EDGE,{"derivedFrom":sQuery(id+"F2.wireOp",EDGE,"E62.1.40.0")}),1.0]])]});
            var Q11;
            Q11=makeQuery(id+"F2.imprint","IMPRINT",FACE,{"disambiguationData":[TD([[makeQuery(id+"F2.imprint","IMPRINT",EDGE,{"derivedFrom":sQuery(id+"F2.wireOp",EDGE,"E62.1.39.0")}),1.0]])]});
            var Q12;
            Q12=makeQuery(id+"F2.imprint","IMPRINT",FACE,{"disambiguationData":[TD([[makeQuery(id+"F2.imprint","IMPRINT",EDGE,{"derivedFrom":sQuery(id+"F2.wireOp",EDGE,"E62.1.38.0")}),1.0]])]});
            var Q13;
            Q13=makeQuery(id+"F2.imprint","IMPRINT",FACE,{"disambiguationData":[TD([[makeQuery(id+"F2.imprint","IMPRINT",EDGE,{"derivedFrom":sQuery(id+"F2.wireOp",EDGE,"E62.1.37.0")}),1.0]])]});
            var Q14;
            Q14=makeQuery(id+"F2.imprint","IMPRINT",FACE,{"disambiguationData":[TD([[makeQuery(id+"F2.imprint","IMPRINT",EDGE,{"derivedFrom":sQuery(id+"F2.wireOp",EDGE,"E62.1.36.0")}),1.0]])]});
            var Q15;
            Q15=makeQuery(id+"F2.imprint","IMPRINT",FACE,{"disambiguationData":[TD([[makeQuery(id+"F2.imprint","IMPRINT",EDGE,{"derivedFrom":sQuery(id+"F2.wireOp",EDGE,"E62.1.35.0")}),1.0]])]});
            var Q16;
            Q16=makeQuery(id+"F2.imprint","IMPRINT",FACE,{"disambiguationData":[TD([[makeQuery(id+"F2.imprint","IMPRINT",EDGE,{"derivedFrom":sQuery(id+"F2.wireOp",EDGE,"E62.1.34.0")}),1.0]])]});
            var Q17;
            Q17=makeQuery(id+"F2.imprint","IMPRINT",FACE,{"disambiguationData":[TD([[makeQuery(id+"F2.imprint","IMPRINT",EDGE,{"derivedFrom":sQuery(id+"F2.wireOp",EDGE,"E62.1.33.0")}),1.0]])]});
            var Q18;
            Q18=makeQuery(id+"F2.imprint","IMPRINT",FACE,{"disambiguationData":[TD([[makeQuery(id+"F2.imprint","IMPRINT",EDGE,{"derivedFrom":sQuery(id+"F2.wireOp",EDGE,"E62.1.32.0")}),1.0]])]});
            var Q19;
            Q19=makeQuery(id+"F2.imprint","IMPRINT",FACE,{"disambiguationData":[TD([[makeQuery(id+"F2.imprint","IMPRINT",EDGE,{"derivedFrom":sQuery(id+"F2.wireOp",EDGE,"E62.1.31.0")}),1.0]])]});
            var Q20;
            Q20=makeQuery(id+"F2.imprint","IMPRINT",FACE,{"disambiguationData":[TD([[makeQuery(id+"F2.imprint","IMPRINT",EDGE,{"derivedFrom":sQuery(id+"F2.wireOp",EDGE,"E62.1.30.0")}),1.0]])]});
            var Q21;
            Q21=makeQuery(id+"F2.imprint","IMPRINT",FACE,{"disambiguationData":[TD([[makeQuery(id+"F2.imprint","IMPRINT",EDGE,{"derivedFrom":sQuery(id+"F2.wireOp",EDGE,"E62.1.29.0")}),1.0]])]});
            var Q22;
            Q22=makeQuery(id+"F2.imprint","IMPRINT",FACE,{"disambiguationData":[TD([[makeQuery(id+"F2.imprint","IMPRINT",EDGE,{"derivedFrom":sQuery(id+"F2.wireOp",EDGE,"E62.1.28.0")}),1.0]])]});
            var Q23;
            Q23=makeQuery(id+"F2.imprint","IMPRINT",FACE,{"disambiguationData":[TD([[makeQuery(id+"F2.imprint","IMPRINT",EDGE,{"derivedFrom":sQuery(id+"F2.wireOp",EDGE,"E62.1.27.0")}),1.0]])]});
            var Q24;
            Q24=makeQuery(id+"F2.imprint","IMPRINT",FACE,{"disambiguationData":[TD([[makeQuery(id+"F2.imprint","IMPRINT",EDGE,{"derivedFrom":sQuery(id+"F2.wireOp",EDGE,"E62.1.26.0")}),1.0]])]});
            var Q25;
            Q25=makeQuery(id+"F2.imprint","IMPRINT",FACE,{"disambiguationData":[TD([[makeQuery(id+"F2.imprint","IMPRINT",EDGE,{"derivedFrom":sQuery(id+"F2.wireOp",EDGE,"E62.1.25.0")}),1.0]])]});
            var Q26;
            Q26=makeQuery(id+"F2.imprint","IMPRINT",FACE,{"disambiguationData":[TD([[makeQuery(id+"F2.imprint","IMPRINT",EDGE,{"derivedFrom":sQuery(id+"F2.wireOp",EDGE,"E62.1.24.0")}),1.0]])]});
            var Q27;
            Q27=makeQuery(id+"F2.imprint","IMPRINT",FACE,{"disambiguationData":[TD([[makeQuery(id+"F2.imprint","IMPRINT",EDGE,{"derivedFrom":sQuery(id+"F2.wireOp",EDGE,"E62.1.23.0")}),1.0]])]});
            var Q28;
            Q28=makeQuery(id+"F2.imprint","IMPRINT",FACE,{"disambiguationData":[TD([[makeQuery(id+"F2.imprint","IMPRINT",EDGE,{"derivedFrom":sQuery(id+"F2.wireOp",EDGE,"E62.1.22.0")}),1.0]])]});
            var Q29;
            Q29=makeQuery(id+"F2.imprint","IMPRINT",FACE,{"disambiguationData":[TD([[makeQuery(id+"F2.imprint","IMPRINT",EDGE,{"derivedFrom":sQuery(id+"F2.wireOp",EDGE,"E62.1.21.0")}),1.0]])]});
            var Q30;
            Q30=makeQuery(id+"F2.imprint","IMPRINT",FACE,{"disambiguationData":[TD([[makeQuery(id+"F2.imprint","IMPRINT",EDGE,{"derivedFrom":sQuery(id+"F2.wireOp",EDGE,"E62.1.20.0")}),1.0]])]});
            var Q31;
            Q31=makeQuery(id+"F2.imprint","IMPRINT",FACE,{"disambiguationData":[TD([[makeQuery(id+"F2.imprint","IMPRINT",EDGE,{"derivedFrom":sQuery(id+"F2.wireOp",EDGE,"E62.1.19.0")}),1.0]])]});
            var Q32;
            Q32=makeQuery(id+"F2.imprint","IMPRINT",FACE,{"disambiguationData":[TD([[makeQuery(id+"F2.imprint","IMPRINT",EDGE,{"derivedFrom":sQuery(id+"F2.wireOp",EDGE,"E62.1.18.0")}),1.0]])]});
            var Q33;
            Q33=makeQuery(id+"F2.imprint","IMPRINT",FACE,{"disambiguationData":[TD([[makeQuery(id+"F2.imprint","IMPRINT",EDGE,{"derivedFrom":sQuery(id+"F2.wireOp",EDGE,"E62.1.17.0")}),1.0]])]});
            var Q34;
            Q34=makeQuery(id+"F2.imprint","IMPRINT",FACE,{"disambiguationData":[TD([[makeQuery(id+"F2.imprint","IMPRINT",EDGE,{"derivedFrom":sQuery(id+"F2.wireOp",EDGE,"E62.1.16.0")}),1.0]])]});
            var Q35;
            Q35=makeQuery(id+"F2.imprint","IMPRINT",FACE,{"disambiguationData":[TD([[makeQuery(id+"F2.imprint","IMPRINT",EDGE,{"derivedFrom":sQuery(id+"F2.wireOp",EDGE,"E62.1.15.0")}),1.0]])]});
            var Q36;
            Q36=makeQuery(id+"F2.imprint","IMPRINT",FACE,{"disambiguationData":[TD([[makeQuery(id+"F2.imprint","IMPRINT",EDGE,{"derivedFrom":sQuery(id+"F2.wireOp",EDGE,"E62.1.14.0")}),1.0]])]});
            var Q37;
            Q37=makeQuery(id+"F2.imprint","IMPRINT",FACE,{"disambiguationData":[TD([[makeQuery(id+"F2.imprint","IMPRINT",EDGE,{"derivedFrom":sQuery(id+"F2.wireOp",EDGE,"E62.1.13.0")}),1.0]])]});
            var Q38;
            Q38=makeQuery(id+"F2.imprint","IMPRINT",FACE,{"disambiguationData":[TD([[makeQuery(id+"F2.imprint","IMPRINT",EDGE,{"derivedFrom":sQuery(id+"F2.wireOp",EDGE,"E62.1.12.0")}),1.0]])]});
            var Q39;
            Q39=makeQuery(id+"F2.imprint","IMPRINT",FACE,{"disambiguationData":[TD([[makeQuery(id+"F2.imprint","IMPRINT",EDGE,{"derivedFrom":sQuery(id+"F2.wireOp",EDGE,"E62.1.11.0")}),1.0]])]});
            var Q40;
            Q40=makeQuery(id+"F2.imprint","IMPRINT",FACE,{"disambiguationData":[TD([[makeQuery(id+"F2.imprint","IMPRINT",EDGE,{"derivedFrom":sQuery(id+"F2.wireOp",EDGE,"E62.1.10.0")}),1.0]])]});
            var Q41;
            Q41=makeQuery(id+"F2.imprint","IMPRINT",FACE,{"disambiguationData":[TD([[makeQuery(id+"F2.imprint","IMPRINT",EDGE,{"derivedFrom":sQuery(id+"F2.wireOp",EDGE,"E62.1.9.0")}),1.0]])]});
            var Q42;
            Q42=makeQuery(id+"F2.imprint","IMPRINT",FACE,{"disambiguationData":[TD([[makeQuery(id+"F2.imprint","IMPRINT",EDGE,{"derivedFrom":sQuery(id+"F2.wireOp",EDGE,"E62.1.8.0")}),1.0]])]});
            var Q43;
            Q43=makeQuery(id+"F2.imprint","IMPRINT",FACE,{"disambiguationData":[TD([[makeQuery(id+"F2.imprint","IMPRINT",EDGE,{"derivedFrom":sQuery(id+"F2.wireOp",EDGE,"E62.1.7.0")}),1.0]])]});
            var Q44;
            Q44=makeQuery(id+"F2.imprint","IMPRINT",FACE,{"disambiguationData":[TD([[makeQuery(id+"F2.imprint","IMPRINT",EDGE,{"derivedFrom":sQuery(id+"F2.wireOp",EDGE,"E62.1.6.0")}),1.0]])]});
            var Q45;
            Q45=makeQuery(id+"F2.imprint","IMPRINT",FACE,{"disambiguationData":[TD([[makeQuery(id+"F2.imprint","IMPRINT",EDGE,{"derivedFrom":sQuery(id+"F2.wireOp",EDGE,"E62.1.5.0")}),1.0]])]});
            var Q46;
            Q46=makeQuery(id+"F2.imprint","IMPRINT",FACE,{"disambiguationData":[TD([[makeQuery(id+"F2.imprint","IMPRINT",EDGE,{"derivedFrom":sQuery(id+"F2.wireOp",EDGE,"E62.1.4.0")}),1.0]])]});
            var Q47;
            Q47=makeQuery(id+"F2.imprint","IMPRINT",FACE,{"disambiguationData":[TD([[makeQuery(id+"F2.imprint","IMPRINT",EDGE,{"derivedFrom":sQuery(id+"F2.wireOp",EDGE,"E62.1.3.0")}),1.0]])]});
            var Q48;
            Q48=makeQuery(id+"F2.imprint","IMPRINT",FACE,{"disambiguationData":[TD([[makeQuery(id+"F2.imprint","IMPRINT",EDGE,{"derivedFrom":sQuery(id+"F2.wireOp",EDGE,"E61.2.1")}),1.0]])]});
            var Q49;
            Q49=makeQuery(id+"F2.imprint","IMPRINT",FACE,{"disambiguationData":[TD([[makeQuery(id+"F2.imprint","IMPRINT",EDGE,{"derivedFrom":sQuery(id+"F2.wireOp",EDGE,"E61.1.1")}),1.0]])]});
            extrude(context, id + "F3", {"entities" : qUnion([Q0, Q1, Q2, Q3, Q4, Q5, Q6, Q7, Q8, Q9, Q10, Q11, Q12, Q13, Q14, Q15, Q16, Q17, Q18, Q19, Q20, Q21, Q22, Q23, Q24, Q25, Q26, Q27, Q28, Q29, Q30, Q31, Q32, Q33, Q34, Q35, Q36, Q37, Q38, Q39, Q40, Q41, Q42, Q43, Q44, Q45, Q46, Q47, Q48, Q49]), "operationType" : NewBodyOperationType.ADD, "oppositeDirection" : true, "depth" : 127 * mm});
        }
    });
